FCSTD DOCUMENT  (FreeCAD 0.20R29177 (Git))
Label: assembly
Comment: LumenPnP
License: GPL-3.0 license
LicenseURL: https://github.com/opulo-inc/lumenpnp/blob/main/LICENSE
objects: Part::FeaturePython×378, App::FeaturePython×81, App::DocumentObjectGroup×34, Part::Feature×10, Part::Compound×2
note: 390 computed .brp shape members not serialized (recipe doc carries the construction recipe); baked Part::Feature solids carry a one-line shape summary decoded from their .brp

FEATURE [Part::FeaturePython] b_OTS_0009_20x20_v_slot_600mm1_001_003  label="vslot-extrusion-20mmx20mmx600mm005"  # a2plus imported part (geometry in sourceFile) (typed FeaturePython)
  Placement = pos=(-0.0573608,219.183,134.886) rot=(0.57735,-0.57735,-0.57735;2.0944rad)
  Visibility1 = true
  a2p_Version = V0.1
  fixedPosition = false
  objectType = a2pPart
  sourceFile = ./MISC/vslot-extrusion-20mmx20mmx600mm.step
  sourcePart = vslot-extrusion-20mmx20mmx600mm
  subassemblyImport = false
  timeLastImport = 1.66336e+09
  updateColors = true
FEATURE [Part::FeaturePython] Screw021  label="M5x40-Screw339"  # Fasteners workbench fastener (typed FeaturePython)
  Placement = pos=(634.23,194.1,163.97) rot=(0,0,1;1.5708rad)
  Visibility1 = true
  diameter = 6
  invert = false
  leftHanded = false
  length = 12
  lengthCustom = 40
  matchOuter = false
  offset = 0
  thread = false
  type = 33
FEATURE [Part::FeaturePython] Screw022  label="M5x10-Screw"  # Fasteners workbench fastener (typed FeaturePython)
  Placement = pos=(25.025,209.125,159.768) rot=(0,0,-1;1.5708rad)
  Visibility1 = true
  diameter = 6
  invert = false
  leftHanded = false
  length = 1
  lengthCustom = 10
  matchOuter = false
  offset = 0
  thread = false
  type = 33
FEATURE [Part::FeaturePython] b_M5_tslot_nut1_001_  label="M5-tslot-nut"  # a2plus imported part (geometry in sourceFile) (typed FeaturePython)
  Placement = pos=(25.0282,209.312,148.905) rot=(0,0,1;0rad)
  Visibility1 = true
  a2p_Version = V0.1
  fixedPosition = false
  objectType = a2pPart
  sourceFile = ./FST/M5-tslot-nut.step
  sourcePart = M5-tslot-nut
  subassemblyImport = false
  timeLastImport = 1.66336e+09
  updateColors = true
FEATURE [Part::FeaturePython] b_M5_tslot_nut1_001_001  label="M5-tslot-nut001"  # a2plus imported part (geometry in sourceFile) (typed FeaturePython)
  Placement = pos=(572.328,209.112,148.905) rot=(0,0,1;0rad)
  Visibility1 = true
  a2p_Version = V0.1
  fixedPosition = false
  objectType = a2pPart
  sourceFile = ./FST/M5-tslot-nut.step
  sourcePart = M5-tslot-nut
  subassemblyImport = false
  timeLastImport = 1.66336e+09
  updateColors = true
FEATURE [Part::FeaturePython] Screw023  label="M5x10-Screw321"  # Fasteners workbench fastener (typed FeaturePython)
  Placement = pos=(572.27,209.12,158.94) rot=(0,0,-1;1.5708rad)
  Visibility1 = true
  diameter = 6
  invert = false
  leftHanded = false
  length = 1
  lengthCustom = 10
  matchOuter = false
  offset = 0
  thread = false
  type = 33
FEATURE [Part::FeaturePython] b_FDM_0027_belt_clamp_001_  label="belt-clamp001"  # a2plus imported part (geometry in sourceFile) (typed FeaturePython)
  Placement = pos=(-11.975,236.125,99.7676) rot=(0.57735,-0.57735,-0.57735;2.0944rad)
  Visibility1 = true
  a2p_Version = V0.1
  fixedPosition = false
  objectType = a2pPart
  sourceFile = ./FDM/belt-clamp.FCStd
  sourcePart = Body
  subassemblyImport = false
  timeLastImport = 1.66336e+09
  updateColors = true
FEATURE [Part::FeaturePython] b_FDM_0027_belt_clamp_001_001  label="belt-clamp002"  # a2plus imported part (geometry in sourceFile) (typed FeaturePython)
  Placement = pos=(-11.975,182.125,99.7676) rot=(-0.57735,0.57735,0.57735;4.18879rad)
  Visibility1 = true
  a2p_Version = V0.1
  fixedPosition = false
  objectType = a2pPart
  sourceFile = ./FDM/belt-clamp.FCStd
  sourcePart = Body
  subassemblyImport = false
  timeLastImport = 1.66336e+09
  updateColors = true
FEATURE [Part::FeaturePython] Screw099  label="M3x8-Screw670"  # Fasteners workbench fastener (typed FeaturePython)
  Placement = pos=(-58.975,224.625,159.768) rot=(1,0,0;3.14159rad)
  Visibility1 = true
  diameter = 1
  invert = false
  leftHanded = false
  length = 1
  lengthCustom = 8
  matchOuter = false
  offset = 0
  thread = false
  type = 39
FEATURE [Part::FeaturePython] Screw097  label="M3x8-Screw671"  # Fasteners workbench fastener (typed FeaturePython)
  Placement = pos=(-27.975,224.625,159.768) rot=(1,0,0;3.14159rad)
  Visibility1 = true
  diameter = 1
  invert = false
  leftHanded = false
  length = 1
  lengthCustom = 8
  matchOuter = false
  offset = 0
  thread = false
  type = 39
FEATURE [Part::FeaturePython] Screw100  label="M3x8-Screw672"  # Fasteners workbench fastener (typed FeaturePython)
  Placement = pos=(-58.975,193.625,159.768) rot=(1,0,0;3.14159rad)
  Visibility1 = true
  diameter = 1
  invert = false
  leftHanded = false
  length = 1
  lengthCustom = 8
  matchOuter = false
  offset = 0
  thread = false
  type = 39
FEATURE [Part::FeaturePython] Screw098  label="M3x8-Screw673"  # Fasteners workbench fastener (typed FeaturePython)
  Placement = pos=(-27.975,193.625,159.768) rot=(1,0,0;3.14159rad)
  Visibility1 = true
  diameter = 1
  invert = false
  leftHanded = false
  length = 1
  lengthCustom = 8
  matchOuter = false
  offset = 0
  thread = false
  type = 39
FEATURE [Part::FeaturePython] Screw059  label="M5x25-Screw122"  # Fasteners workbench fastener (typed FeaturePython)
  Placement = pos=(634.17,209.27,154.08) rot=(0,0,1;1.5708rad)
  Visibility1 = true
  diameter = 6
  invert = false
  leftHanded = false
  length = 6
  lengthCustom = 25
  matchOuter = false
  offset = 0
  thread = false
  type = 33
FEATURE [Part::FeaturePython] Screw060  label="M3x16-Screw084"  # Fasteners workbench fastener (typed FeaturePython)
  Placement = pos=(638.25,224.21,144.08) rot=(0.57735,-0.57735,0.57735;4.18879rad)
  Visibility1 = true
  diameter = 4
  invert = false
  leftHanded = false
  length = 6
  lengthCustom = 16
  matchOuter = false
  offset = 0
  thread = false
  type = 33
FEATURE [Part::FeaturePython] Screw058  label="M5x10-Screw326"  # Fasteners workbench fastener (typed FeaturePython)
  Placement = pos=(615.37,236.11,106.53) rot=(0.57735,0.57735,0.57735;2.0944rad)
  Visibility1 = true
  diameter = 6
  invert = false
  leftHanded = false
  length = 1
  lengthCustom = 10
  matchOuter = false
  offset = 0
  thread = false
  type = 33
FEATURE [Part::FeaturePython] Screw057  label="M5x10-Screw366"  # Fasteners workbench fastener (typed FeaturePython)
  Placement = pos=(615.37,236.11,91.54) rot=(0.57735,0.57735,0.57735;2.0944rad)
  Visibility1 = true
  diameter = 6
  invert = false
  leftHanded = false
  length = 1
  lengthCustom = 10
  matchOuter = false
  offset = 0
  thread = false
  type = 33
FEATURE [Part::FeaturePython] Screw056  label="M5x10-Screw328"  # Fasteners workbench fastener (typed FeaturePython)
  Placement = pos=(615.37,182.19,91.54) rot=(0.57735,0.57735,0.57735;2.0944rad)
  Visibility1 = true
  diameter = 6
  invert = false
  leftHanded = false
  length = 1
  lengthCustom = 10
  matchOuter = false
  offset = 0
  thread = false
  type = 33
FEATURE [Part::FeaturePython] b_FDM_0027_belt_clamp_001_005  label="belt-clamp003"  # a2plus imported part (geometry in sourceFile) (typed FeaturePython)
  Placement = pos=(612.402,182.156,98.9408) rot=(0.57735,0.57735,0.57735;2.0944rad)
  Visibility1 = true
  a2p_Version = V0.1
  fixedPosition = false
  objectType = a2pPart
  sourceFile = ./FDM/belt-clamp.FCStd
  sourcePart = Body
  subassemblyImport = false
  timeLastImport = 1.66336e+09
  updateColors = true
FEATURE [Part::FeaturePython] b_FDM_0027_belt_clamp_001_004  label="belt-clamp004"  # a2plus imported part (geometry in sourceFile) (typed FeaturePython)
  Placement = pos=(612.402,236.126,99.0108) rot=(0.57735,0.57735,0.57735;2.0944rad)
  Visibility1 = true
  a2p_Version = V0.1
  fixedPosition = false
  objectType = a2pPart
  sourceFile = ./FDM/belt-clamp.FCStd
  sourcePart = Body
  subassemblyImport = false
  timeLastImport = 1.66336e+09
  updateColors = true
FEATURE [Part::FeaturePython] b_Nema_17_42A02C_v21_001_001  label="NEMA17-stepper"  # a2plus imported part (geometry in sourceFile) (typed FeaturePython)
  Placement = pos=(-43.475,209.125,154.768) rot=(1,0,0;3.14159rad)
  Visibility1 = true
  a2p_Version = V0.1
  fixedPosition = false
  objectType = a2pPart
  sourceFile = ./MISC/NEMA17-stepper.step 
  sourcePart = NEMA17-stepper
  subassemblyImport = false
  timeLastImport = 1.64563e+09
  updateColors = true
FEATURE [Part::FeaturePython] Nut043  label="M5-Nut604"  # Fasteners workbench fastener (typed FeaturePython)
  Placement = pos=(634.166,209.269,134.219) rot=(0.707107,-0.707107,0;3.14159rad)
  Visibility1 = true
  diameter = 3
  invert = false
  leftHanded = false
  matchOuter = false
  offset = 0
  thread = false
  type = 5
FEATURE [Part::FeaturePython] Nut042  label="M5-Nut605"  # Fasteners workbench fastener (typed FeaturePython)
  Placement = pos=(634.224,194.15,128.957) rot=(0.866025,0.5,0;3.14159rad)
  Visibility1 = true
  diameter = 3
  invert = false
  leftHanded = false
  matchOuter = false
  offset = 0
  thread = false
  type = 5
FEATURE [Part::FeaturePython] b_Gates_2GT_20T_Toothed_Pulley1_001_001  label="GT2-pulley"  # a2plus imported part (geometry in sourceFile) (typed FeaturePython)
  Placement = pos=(-43.475,209.125,156.168) rot=(0.57735,0.57735,-0.57735;4.18879rad)
  Visibility1 = true
  a2p_Version = V0.1
  fixedPosition = false
  objectType = a2pPart
  sourceFile = ./cad/MISC/GT2-pulley.STEP
  sourcePart = GT2-pulley
  subassemblyImport = false
  timeLastImport = 1.64563e+09
  updateColors = true
FEATURE [Part::FeaturePython] b_Gates_2GT_20T_Toothed_Idler1_001_002  label="GT2-idler"  # a2plus imported part (geometry in sourceFile) (typed FeaturePython)
  Placement = pos=(634.179,209.286,138.99) rot=(0.57735,-0.57735,-0.57735;2.0944rad)
  Visibility1 = true
  a2p_Version = V0.1
  fixedPosition = false
  objectType = a2pPart
  sourceFile = ./cad/MISC/GT2-idler.STEP
  sourcePart = GT2-idler
  subassemblyImport = false
  timeLastImport = 1.64563e+09
  updateColors = true
FEATURE [Part::FeaturePython] Screw055  label="M5x10-Screw329"  # Fasteners workbench fastener (typed FeaturePython)
  Placement = pos=(615.37,182.19,106.47) rot=(0.57735,0.57735,0.57735;2.0944rad)
  Visibility1 = true
  diameter = 6
  invert = false
  leftHanded = false
  length = 1
  lengthCustom = 10
  matchOuter = false
  offset = 0
  thread = false
  type = 33
FEATURE [Part::FeaturePython] Nut041  label="M5-Nut608"  # Fasteners workbench fastener (typed FeaturePython)
  Placement = pos=(605.676,236.093,106.547) rot=(0.447214,0.774597,0.447214;1.82348rad)
  Visibility1 = true
  diameter = 7
  invert = false
  leftHanded = false
  matchOuter = false
  offset = 0
  thread = false
  type = 7
FEATURE [Part::FeaturePython] Nut040  label="M5-Nut609"  # Fasteners workbench fastener (typed FeaturePython)
  Placement = pos=(605.676,236.072,91.571) rot=(0.447214,0.774597,0.447214;1.82348rad)
  Visibility1 = true
  diameter = 7
  invert = false
  leftHanded = false
  matchOuter = false
  offset = 0
  thread = false
  type = 7
FEATURE [Part::FeaturePython] Nut039  label="M5-Nut612"  # Fasteners workbench fastener (typed FeaturePython)
  Placement = pos=(605.676,182.149,106.514) rot=(0.447214,0.774597,0.447214;1.82348rad)
  Visibility1 = true
  diameter = 7
  invert = false
  leftHanded = false
  matchOuter = false
  offset = 0
  thread = false
  type = 7
FEATURE [Part::FeaturePython] Nut038  label="M5-Nut613"  # Fasteners workbench fastener (typed FeaturePython)
  Placement = pos=(605.676,182.168,91.527) rot=(0.447214,0.774597,0.447214;1.82348rad)
  Visibility1 = true
  diameter = 7
  invert = false
  leftHanded = false
  matchOuter = false
  offset = 0
  thread = false
  type = 7
FEATURE [Part::FeaturePython] Nut044  label="M3-Nut451"  # Fasteners workbench fastener (typed FeaturePython)
  Placement = pos=(632.154,224.209,144.071) rot=(0.447214,-0.774597,-0.447214;1.82348rad)
  Visibility1 = true
  diameter = 4
  invert = false
  leftHanded = false
  matchOuter = false
  offset = 0
  thread = false
  type = 7
FEATURE [Part::FeaturePython] b_OTS_0002_00_usb_webcam_001_  label="usb-camera"  # a2plus imported part (geometry in sourceFile) (typed FeaturePython)
  Placement = pos=(444.284,221.423,101.39) rot=(1,0,0;3.14159rad)
  Visibility1 = true
  a2p_Version = V0.1
  fixedPosition = false
  objectType = a2pPart
  sourceFile = ./MISC/usb-camera.FCStd
  sourcePart = Body
  subassemblyImport = false
  timeLastImport = 1.66336e+09
  updateColors = true
FEATURE [Part::FeaturePython] b_FDM_0011_x_gantry_front_001_  label="x-gantry-front"  # a2plus imported part (geometry in sourceFile) (typed FeaturePython)
  Placement = pos=(443.775,194.2,123.4) rot=(1,0,0;1.5708rad)
  Visibility1 = true
  a2p_Version = V0.1
  fixedPosition = false
  objectType = a2pPart
  sourceFile = ./FDM/x-gantry-front.FCStd
  sourcePart = Body
  subassemblyImport = false
  timeLastImport = 1.66336e+09
  updateColors = true
FEATURE [Part::FeaturePython] b_FDM_0014_down_camera_mount_001_  label="top-camera-mount"  # a2plus imported part (geometry in sourceFile) (typed FeaturePython)
  Placement = pos=(443.775,224.45,104.9) rot=(0,0,1;3.14159rad)
  Visibility1 = true
  a2p_Version = V0.1
  fixedPosition = false
  objectType = a2pPart
  sourceFile = ./FDM/top-camera-mount.FCStd
  sourcePart = Body
  subassemblyImport = false
  timeLastImport = 1.66336e+09
  updateColors = true
FEATURE [Part::FeaturePython] b_FDM_0015_down_light_mount_001_  label="top-light-mount"  # a2plus imported part (geometry in sourceFile) (typed FeaturePython)
  Placement = pos=(443.775,224.45,81.4) rot=(-0.223515,0.973178,-0.054468;0rad)
  Visibility1 = true
  a2p_Version = V0.1
  fixedPosition = false
  objectType = a2pPart
  sourceFile = ./FDM/top-light-mount.FCStd
  sourcePart = Body
  subassemblyImport = false
  timeLastImport = 1.66336e+09
  updateColors = true
FEATURE [Part::FeaturePython] b_FDM_0027_belt_clamp_001_002  label="belt-clamp005"  # a2plus imported part (geometry in sourceFile) (typed FeaturePython)
  Placement = pos=(422.775,234.2,144.9) rot=(-1,0,0;1.5708rad)
  Visibility1 = true
  a2p_Version = V0.1
  fixedPosition = false
  objectType = a2pPart
  sourceFile = ./FDM/belt-clamp.FCStd
  sourcePart = Body
  subassemblyImport = false
  timeLastImport = 1.66336e+09
  updateColors = true
FEATURE [Part::FeaturePython] Nut021  label="M5-Nut919"  # Fasteners workbench fastener (typed FeaturePython)
  Placement = pos=(464.775,228.2,152.4) rot=(-0.186157,0.694747,0.694747;2.77349rad)
  Visibility1 = true
  diameter = 7
  invert = false
  leftHanded = false
  matchOuter = false
  offset = 0
  thread = false
  type = 7
FEATURE [Part::FeaturePython] Nut022  label="M5-Nut920"  # Fasteners workbench fastener (typed FeaturePython)
  Placement = pos=(464.775,228.2,137.4) rot=(-0.186157,0.694747,0.694747;2.77349rad)
  Visibility1 = true
  diameter = 7
  invert = false
  leftHanded = false
  matchOuter = false
  offset = 0
  thread = false
  type = 7
FEATURE [Part::FeaturePython] Screw038  label="M5x10-Screw483"  # Fasteners workbench fastener (typed FeaturePython)
  Placement = pos=(464.775,237.2,137.4) rot=(0.57735,0.57735,0.57735;4.18879rad)
  Visibility1 = true
  diameter = 6
  invert = false
  leftHanded = false
  length = 1
  lengthCustom = 10
  matchOuter = false
  offset = 0
  thread = false
  type = 33
FEATURE [Part::FeaturePython] Screw039  label="M5x10-Screw484"  # Fasteners workbench fastener (typed FeaturePython)
  Placement = pos=(464.775,237.2,152.4) rot=(-0.57735,-0.57735,-0.57735;2.0944rad)
  Visibility1 = true
  diameter = 6
  invert = false
  leftHanded = false
  length = 1
  lengthCustom = 10
  matchOuter = false
  offset = 0
  thread = false
  type = 33
FEATURE [Part::FeaturePython] Nut023  label="M5-Nut921"  # Fasteners workbench fastener (typed FeaturePython)
  Placement = pos=(422.775,228.417,137.4) rot=(-0.186157,0.694747,0.694747;2.77349rad)
  Visibility1 = true
  diameter = 7
  invert = false
  leftHanded = false
  matchOuter = false
  offset = 0
  thread = false
  type = 7
FEATURE [Part::FeaturePython] Nut024  label="M5-Nut922"  # Fasteners workbench fastener (typed FeaturePython)
  Placement = pos=(422.775,228.2,152.4) rot=(-0.186157,0.694747,0.694747;2.77349rad)
  Visibility1 = true
  diameter = 7
  invert = false
  leftHanded = false
  matchOuter = false
  offset = 0
  thread = false
  type = 7
FEATURE [Part::FeaturePython] Screw040  label="M5x10-Screw485"  # Fasteners workbench fastener (typed FeaturePython)
  Placement = pos=(422.775,237.2,152.4) rot=(0.57735,0.57735,0.57735;4.18879rad)
  Visibility1 = true
  diameter = 6
  invert = false
  leftHanded = false
  length = 1
  lengthCustom = 10
  matchOuter = false
  offset = 0
  thread = false
  type = 33
FEATURE [Part::FeaturePython] b_FDM_0027_belt_clamp_001_003  label="belt-clamp006"  # a2plus imported part (geometry in sourceFile) (typed FeaturePython)
  Placement = pos=(464.775,234.2,144.9) rot=(0,0.707107,0.707107;3.14159rad)
  Visibility1 = true
  a2p_Version = V0.1
  fixedPosition = false
  objectType = a2pPart
  sourceFile = ./FDM/belt-clamp.FCStd
  sourcePart = Body
  subassemblyImport = false
  timeLastImport = 1.66336e+09
  updateColors = true
FEATURE [Part::FeaturePython] b_Nema_17_42A02C_v21_001_  label="NEMA17-stepper001"  # a2plus imported part (geometry in sourceFile) (typed FeaturePython)
  Placement = pos=(443.776,187.252,212.248) rot=(-0.268444,0.681153,-0.681153;3.66612rad)
  Visibility1 = true
  a2p_Version = V0.1
  fixedPosition = false
  objectType = a2pPart
  sourceFile = ./MISC/NEMA17-stepper.step 
  sourcePart = NEMA17-stepper
  subassemblyImport = false
  timeLastImport = 1.64563e+09
  updateColors = true
FEATURE [Part::FeaturePython] b_Gates_2GT_20T_Toothed_Idler1_001_  label="GT2-idler001"  # a2plus imported part (geometry in sourceFile) (typed FeaturePython)
  Placement = pos=(443.78,185.1,99.0503) rot=(-0.707107,0,0.707107;3.14159rad)
  Visibility1 = true
  a2p_Version = V0.1
  fixedPosition = false
  objectType = a2pPart
  sourceFile = ./cad/MISC/GT2-idler.STEP
  sourcePart = GT2-idler
  subassemblyImport = false
  timeLastImport = 1.64563e+09
  updateColors = true
FEATURE [Part::FeaturePython] Screw086  label="M3x8-Screw507"  # Fasteners workbench fastener (typed FeaturePython)
  Placement = pos=(443.74,191.38,190.34) rot=(1,0,0;1.5708rad)
  Visibility1 = true
  diameter = 1
  invert = false
  leftHanded = false
  length = 1
  lengthCustom = 8
  matchOuter = false
  offset = 0
  thread = false
  type = 39
FEATURE [Part::FeaturePython] Screw087  label="M3x8-Screw508"  # Fasteners workbench fastener (typed FeaturePython)
  Placement = pos=(465.75,191.38,212.29) rot=(1,0,0;1.5708rad)
  Visibility1 = true
  diameter = 1
  invert = false
  leftHanded = false
  length = 1
  lengthCustom = 8
  matchOuter = false
  offset = 0
  thread = false
  type = 39
FEATURE [Part::FeaturePython] Screw088  label="M3x8-Screw509"  # Fasteners workbench fastener (typed FeaturePython)
  Placement = pos=(421.83,191.38,212.25) rot=(1,0,0;1.5708rad)
  Visibility1 = true
  diameter = 1
  invert = false
  leftHanded = false
  length = 1
  lengthCustom = 8
  matchOuter = false
  offset = 0
  thread = false
  type = 39
FEATURE [Part::FeaturePython] Nut032  label="M3-Nut520"  # Fasteners workbench fastener (typed FeaturePython)
  Placement = pos=(423.74,196.87,104.003) rot=(0.935113,0.250563,-0.250563;1.63783rad)
  Visibility1 = true
  diameter = 4
  invert = false
  leftHanded = false
  matchOuter = false
  offset = 0
  thread = false
  type = 7
FEATURE [Part::FeaturePython] Nut028  label="M3-Nut521"  # Fasteners workbench fastener (typed FeaturePython)
  Placement = pos=(423.738,196.87,143.899) rot=(0.935113,0.250563,-0.250563;1.63783rad)
  Visibility1 = true
  diameter = 4
  invert = false
  leftHanded = false
  matchOuter = false
  offset = 0
  thread = false
  type = 7
FEATURE [Part::FeaturePython] Nut027  label="M3-Nut522"  # Fasteners workbench fastener (typed FeaturePython)
  Placement = pos=(423.75,196.87,183.96) rot=(0.935113,0.250563,-0.250563;1.63783rad)
  Visibility1 = true
  diameter = 4
  invert = false
  leftHanded = false
  matchOuter = false
  offset = 0
  thread = false
  type = 7
FEATURE [Part::FeaturePython] Nut031  label="M3-Nut523"  # Fasteners workbench fastener (typed FeaturePython)
  Placement = pos=(463.628,196.87,184.111) rot=(0.935113,0.250563,-0.250563;1.63783rad)
  Visibility1 = true
  diameter = 4
  invert = false
  leftHanded = false
  matchOuter = false
  offset = 0
  thread = false
  type = 7
FEATURE [Part::FeaturePython] Nut029  label="M3-Nut524"  # Fasteners workbench fastener (typed FeaturePython)
  Placement = pos=(463.702,196.87,104.059) rot=(0.935113,0.250563,-0.250563;1.63783rad)
  Visibility1 = true
  diameter = 4
  invert = false
  leftHanded = false
  matchOuter = false
  offset = 0
  thread = false
  type = 7
FEATURE [Part::FeaturePython] Nut030  label="M3-Nut525"  # Fasteners workbench fastener (typed FeaturePython)
  Placement = pos=(463.67,196.87,144.204) rot=(0.935113,0.250563,-0.250563;1.63783rad)
  Visibility1 = true
  diameter = 4
  invert = false
  leftHanded = false
  matchOuter = false
  offset = 0
  thread = false
  type = 7
FEATURE [Part::FeaturePython] Screw044  label="M5x25-Screw135"  # Fasteners workbench fastener (typed FeaturePython)
  Placement = pos=(443.743,175.103,98.994) rot=(0,0.707107,-0.707107;3.14159rad)
  Visibility1 = true
  diameter = 6
  invert = false
  leftHanded = false
  length = 6
  lengthCustom = 25
  matchOuter = false
  offset = 10.5
  thread = false
  type = 33
FEATURE [Part::FeaturePython] Screw041  label="M5x10-Screw486"  # Fasteners workbench fastener (typed FeaturePython)
  Placement = pos=(422.775,237.2,137.4) rot=(0.57735,0.57735,0.57735;4.18879rad)
  Visibility1 = true
  diameter = 6
  invert = false
  leftHanded = false
  length = 1
  lengthCustom = 10
  matchOuter = false
  offset = 0
  thread = false
  type = 33
FEATURE [Part::FeaturePython] b_Gates_2GT_20T_Toothed_Pulley1_001_  label="GT2-pulley001"  # a2plus imported part (geometry in sourceFile) (typed FeaturePython)
  Placement = pos=(443.79,192,212.28) rot=(-0.707107,0,0.707107;3.14159rad)
  Visibility1 = true
  a2p_Version = V0.1
  fixedPosition = false
  objectType = a2pPart
  sourceFile = ./cad/MISC/GT2-pulley.STEP
  sourcePart = GT2-pulley
  subassemblyImport = false
  timeLastImport = 1.64563e+09
  updateColors = true
FEATURE [Part::FeaturePython] b_FDM_0040_z_gantry_backplate_left_001_  label="z-gantry-backplate-left"  # a2plus imported part (geometry in sourceFile) (typed FeaturePython)
  Placement = pos=(405.5,177.8,112.56) rot=(1,0,0;1.5708rad)
  a2p_Version = V0.1
  fixedPosition = false
  objectType = a2pPart
  sourceFile = .\FDM\z-gantry-backplate-left.FCStd
  subassemblyImport = false
  timeLastImport = 1.65531e+09
  updateColors = true
FEATURE [Part::FeaturePython] Screw144  label="M3x8-Screw531"  # Fasteners workbench fastener (typed FeaturePython)
  Placement = pos=(416.22,171.94,150.64) rot=(1,0,0;1.5708rad)
  Visibility1 = true
  diameter = 1
  invert = false
  leftHanded = false
  length = 1
  lengthCustom = 8
  matchOuter = false
  offset = 0
  thread = false
  type = 39
FEATURE [Part::FeaturePython] Screw146  label="M3x8-Screw532"  # Fasteners workbench fastener (typed FeaturePython)
  Placement = pos=(431.25,171.94,150.53) rot=(1,0,0;1.5708rad)
  Visibility1 = true
  diameter = 1
  invert = false
  leftHanded = false
  length = 1
  lengthCustom = 8
  matchOuter = false
  offset = 0
  thread = false
  type = 39
FEATURE [Part::FeaturePython] b_OTS_0001_00_CP40_nozzle_holder_001_  label="CP40-holder"  # a2plus imported part (geometry in sourceFile) (typed FeaturePython)
  Placement = pos=(420.048,155.79,87.7845) rot=(0.57735,-0.57735,-0.57735;2.0944rad)
  Visibility1 = true
  a2p_Version = V0.1
  fixedPosition = false
  objectType = a2pPart
  sourceFile = ./MISC/cp40-holder.FCStd
  sourcePart = Body
  subassemblyImport = false
  timeLastImport = 1.65531e+09
  updateColors = true
FEATURE [Part::FeaturePython] b_MS4M_M51_001_  label="pneumatic-adapter-MS4M-M5"  # a2plus imported part (geometry in sourceFile) (typed FeaturePython)
  Placement = pos=(420.152,155.83,162.512) rot=(0.57735,-0.57735,-0.57735;2.0944rad)
  Visibility1 = true
  a2p_Version = V0.1
  fixedPosition = false
  objectType = a2pPart
  sourceFile = ./MISC/pneumatic-adapter-MS4M-M5.STEP
  sourcePart = MS4M-M5
  subassemblyImport = false
  timeLastImport = 1.65531e+09
  updateColors = true
FEATURE [Part::FeaturePython] Screw148  label="M3x8-Screw523"  # Fasteners workbench fastener (typed FeaturePython)
  Placement = pos=(456.42,171.94,150.5) rot=(1,0,0;1.5708rad)
  Visibility1 = true
  diameter = 1
  invert = false
  leftHanded = false
  length = 1
  lengthCustom = 8
  matchOuter = false
  offset = 0
  thread = false
  type = 39
FEATURE [Part::FeaturePython] Screw149  label="M3x8-Screw524"  # Fasteners workbench fastener (typed FeaturePython)
  Placement = pos=(471.41,171.94,150.5) rot=(1,0,0;1.5708rad)
  Visibility1 = true
  diameter = 1
  invert = false
  leftHanded = false
  length = 1
  lengthCustom = 8
  matchOuter = false
  offset = 0
  thread = false
  type = 39
FEATURE [Part::FeaturePython] b_FDM_0041_z_gantry_backplate_right_001_  label="z-gantry-backplate-right"  # a2plus imported part (geometry in sourceFile) (typed FeaturePython)
  Placement = pos=(482.233,178.019,112.536) rot=(1,0,0;1.5708rad)
  a2p_Version = V0.1
  fixedPosition = false
  objectType = a2pPart
  sourceFile = ./FDM/z-gantry-backplate-right.FCStd
  sourcePart = Body
  subassemblyImport = false
  timeLastImport = 1.65531e+09
  updateColors = true
FEATURE [Part::FeaturePython] Screw085  label="M3x8-Screw518"  # Fasteners workbench fastener (typed FeaturePython)
  Placement = pos=(443.74,191.38,234.2) rot=(1,0,0;1.5708rad)
  Visibility1 = true
  diameter = 1
  invert = false
  leftHanded = false
  length = 1
  lengthCustom = 8
  matchOuter = false
  offset = 0
  thread = false
  type = 39
FEATURE [Part::FeaturePython] Screw171  label="M3x14-Screw191"  # Fasteners workbench fastener (typed FeaturePython)
  Placement = pos=(466.574,236.252,118.069) rot=(0,0.707107,0.707107;3.14159rad)
  baseObject = -> b_FDM_0014_down_camera_mount_001_ [Edge38]
  diameter = 1
  invert = false
  leftHanded = false
  length = 9
  lengthCustom = 14
  matchOuter = false
  offset = 0
  thread = false
  type = 39
FEATURE [Part::FeaturePython] Nut077  label="M3-Nut"  # Fasteners workbench fastener (typed FeaturePython)
  Placement = pos=(421.275,229.3,118.4) rot=(0,0.707107,0.707107;3.14159rad)
  diameter = 4
  invert = false
  leftHanded = false
  matchOuter = false
  offset = 0
  thread = false
  type = 7
FEATURE [Part::FeaturePython] Nut079  label="M3-Nut543"  # Fasteners workbench fastener (typed FeaturePython)
  Placement = pos=(466.275,229.3,118.4) rot=(0.186157,0.694747,0.694747;3.50969rad)
  diameter = 4
  invert = false
  leftHanded = false
  matchOuter = false
  offset = 0
  thread = false
  type = 7
FEATURE [Part::FeaturePython] b_M5_tslot_nut1_001_008  label="M5-tslot-nut002"  # a2plus imported part (geometry in sourceFile) (typed FeaturePython)
  Placement = pos=(9.94821,-70.1584,105.165) rot=(0,0,1;1.5708rad)
  Visibility1 = true
  a2p_Version = V0.1
  fixedPosition = false
  objectType = a2pPart
  sourceFile = ./FST/M5-tslot-nut.step
  sourcePart = M5-tslot-nut
  subassemblyImport = false
  timeLastImport = 1.66336e+09
  updateColors = true
FEATURE [Part::FeaturePython] Nut048  label="M3-Nut464"  # Fasteners workbench fastener (typed FeaturePython)
  Placement = pos=(24.9656,-93.169,99.99) rot=(0.57735,-0.57735,0.57735;2.0944rad)
  Visibility1 = true
  diameter = 4
  invert = false
  leftHanded = false
  matchOuter = false
  offset = 0
  thread = false
  type = 7
FEATURE [Part::FeaturePython] Nut045  label="M5-Nut625"  # Fasteners workbench fastener (typed FeaturePython)
  Placement = pos=(-5.03877,-97.4915,83.9035) rot=(0.866025,0.5,0;3.14159rad)
  Visibility1 = true
  diameter = 3
  invert = false
  leftHanded = false
  matchOuter = false
  offset = 0
  thread = false
  type = 5
FEATURE [Part::FeaturePython] b_Gates_2GT_20T_Toothed_Idler1_001_001  label="GT2-idler002"  # a2plus imported part (geometry in sourceFile) (typed FeaturePython)
  Placement = pos=(10.0586,-97.7236,95.0003) rot=(0.57735,-0.57735,-0.57735;2.0944rad)
  Visibility1 = true
  a2p_Version = V0.1
  fixedPosition = false
  objectType = a2pPart
  sourceFile = ./cad/MISC/GT2-idler.STEP
  sourcePart = GT2-idler
  subassemblyImport = false
  timeLastImport = 1.64563e+09
  updateColors = true
FEATURE [Part::FeaturePython] Nut033  label="M5-Nut626"  # Fasteners workbench fastener (typed FeaturePython)
  Placement = pos=(9.97594,-97.5692,89.9635) rot=(0.707107,0.707107,0;3.14159rad)
  Visibility1 = true
  diameter = 3
  invert = false
  leftHanded = false
  matchOuter = false
  offset = 0
  thread = false
  type = 5
FEATURE [Part::FeaturePython] Screw052  label="M3x16-Screw085"  # Fasteners workbench fastener (typed FeaturePython)
  Placement = pos=(24.99,-102.16,100) rot=(0.57735,-0.57735,0.57735;2.0944rad)
  Visibility1 = true
  diameter = 4
  invert = false
  leftHanded = false
  length = 6
  lengthCustom = 16
  matchOuter = false
  offset = 0
  thread = false
  type = 33
FEATURE [Part::FeaturePython] Screw053  label="M5x10-Screw334"  # Fasteners workbench fastener (typed FeaturePython)
  Placement = pos=(9.89,-70.16,114.96) rot=(0,0,-1;1.5708rad)
  Visibility1 = true
  diameter = 6
  invert = false
  leftHanded = false
  length = 1
  lengthCustom = 10
  matchOuter = false
  offset = 0
  thread = false
  type = 33
FEATURE [Part::FeaturePython] Screw054  label="M5x25-Screw127"  # Fasteners workbench fastener (typed FeaturePython)
  Placement = pos=(9.99,-97.57,109.98) rot=(0,0,-1;1.5708rad)
  Visibility1 = true
  diameter = 6
  invert = false
  leftHanded = false
  length = 6
  lengthCustom = 25
  matchOuter = false
  offset = 0
  thread = false
  type = 33
FEATURE [Part::FeaturePython] Screw035  label="M5x10-Screw335"  # Fasteners workbench fastener (typed FeaturePython)
  Placement = pos=(-4.92,-45.15,30.1) rot=(0.57735,-0.57735,-0.57735;2.0944rad)
  Visibility1 = true
  diameter = 6
  invert = false
  leftHanded = false
  length = 1
  lengthCustom = 10
  matchOuter = false
  offset = 0
  thread = false
  type = 33
FEATURE [Part::FeaturePython] Screw036  label="M5x10-Screw336"  # Fasteners workbench fastener (typed FeaturePython)
  Placement = pos=(-4.92,-70.14,30.1) rot=(0.57735,-0.57735,-0.57735;2.0944rad)
  Visibility1 = true
  diameter = 6
  invert = false
  leftHanded = false
  length = 1
  lengthCustom = 10
  matchOuter = false
  offset = 0
  thread = false
  type = 33
FEATURE [Part::FeaturePython] Screw037  label="M5x10-Screw337"  # Fasteners workbench fastener (typed FeaturePython)
  Placement = pos=(9.96,-25.33,9.99) rot=(1,0,0;1.5708rad)
  Visibility1 = true
  diameter = 6
  invert = false
  leftHanded = false
  length = 1
  lengthCustom = 10
  matchOuter = false
  offset = 0
  thread = false
  type = 33
FEATURE [Part::FeaturePython] Screw051  label="M5x40-Screw344"  # Fasteners workbench fastener (typed FeaturePython)
  Placement = pos=(-4.98,-97.58,119.74) rot=(0,0,-1;1.5708rad)
  Visibility1 = true
  diameter = 6
  invert = false
  leftHanded = false
  length = 12
  lengthCustom = 40
  matchOuter = false
  offset = 0
  thread = false
  type = 33
FEATURE [Part::FeaturePython] b_M5_tslot_nut1_001_009  label="M5-tslot-nut003"  # a2plus imported part (geometry in sourceFile) (typed FeaturePython)
  Placement = pos=(4.76821,-70.1584,30.1746) rot=(0.57735,0.57735,-0.57735;4.18879rad)
  Visibility1 = true
  a2p_Version = V0.1
  fixedPosition = false
  objectType = a2pPart
  sourceFile = ./FST/M5-tslot-nut.step
  sourcePart = M5-tslot-nut
  subassemblyImport = false
  timeLastImport = 1.66336e+09
  updateColors = true
FEATURE [Part::FeaturePython] b_M5_tslot_nut1_001_010  label="M5-tslot-nut004"  # a2plus imported part (geometry in sourceFile) (typed FeaturePython)
  Placement = pos=(4.76821,-45.2084,30.1746) rot=(0.57735,0.57735,-0.57735;4.18879rad)
  Visibility1 = true
  a2p_Version = V0.1
  fixedPosition = false
  objectType = a2pPart
  sourceFile = ./FST/M5-tslot-nut.step
  sourcePart = M5-tslot-nut
  subassemblyImport = false
  timeLastImport = 1.66336e+09
  updateColors = true
FEATURE [Part::FeaturePython] b_M5_tslot_nut1_001_011  label="M5-tslot-nut005"  # a2plus imported part (geometry in sourceFile) (typed FeaturePython)
  Placement = pos=(9.85821,-15.0384,9.95457) rot=(0,0.707107,-0.707107;3.14159rad)
  Visibility1 = true
  a2p_Version = V0.1
  fixedPosition = false
  objectType = a2pPart
  sourceFile = ./FST/M5-tslot-nut.step
  sourcePart = M5-tslot-nut
  subassemblyImport = false
  timeLastImport = 1.66336e+09
  updateColors = true
FEATURE [Part::FeaturePython] b_FDM_0001_front_left_leg_001_  label="front-left-leg"  # a2plus imported part (geometry in sourceFile) (typed FeaturePython)
  Placement = pos=(19.9755,-0.0519684,19.9889) rot=(0.57735,-0.57735,-0.57735;2.0944rad)
  Visibility1 = true
  a2p_Version = V0.1
  fixedPosition = false
  objectType = a2pPart
  sourceFile = ./FDM/front-left-leg.FCStd
  sourcePart = Body
  subassemblyImport = false
  timeLastImport = 1.66336e+09
  updateColors = true
FEATURE [Part::FeaturePython] Screw061  label="M5x40-Screw345"  # Fasteners workbench fastener (typed FeaturePython)
  Placement = pos=(605.12,-97.58,119.74) rot=(0,0,-1;1.5708rad)
  Visibility1 = true
  diameter = 6
  invert = false
  leftHanded = false
  length = 12
  lengthCustom = 40
  matchOuter = false
  offset = 0
  thread = false
  type = 33
FEATURE [Part::FeaturePython] b_Gates_2GT_20T_Toothed_Idler1_001_003  label="GT2-idler003"  # a2plus imported part (geometry in sourceFile) (typed FeaturePython)
  Placement = pos=(590.059,-97.7236,95.0003) rot=(0.57735,-0.57735,-0.57735;2.0944rad)
  Visibility1 = true
  a2p_Version = V0.1
  fixedPosition = false
  objectType = a2pPart
  sourceFile = ./cad/MISC/GT2-idler.STEP
  sourcePart = GT2-idler
  subassemblyImport = false
  timeLastImport = 1.64563e+09
  updateColors = true
FEATURE [Part::FeaturePython] Nut046  label="M5-Nut627"  # Fasteners workbench fastener (typed FeaturePython)
  Placement = pos=(605.043,-97.4581,83.9035) rot=(0.866025,0.5,0;3.14159rad)
  Visibility1 = true
  diameter = 3
  invert = false
  leftHanded = false
  matchOuter = false
  offset = 0
  thread = false
  type = 5
FEATURE [Part::FeaturePython] Screw062  label="M5x25-Screw128"  # Fasteners workbench fastener (typed FeaturePython)
  Placement = pos=(590.06,-97.57,109.98) rot=(0,0,-1;1.5708rad)
  Visibility1 = true
  diameter = 6
  invert = false
  leftHanded = false
  length = 6
  lengthCustom = 25
  matchOuter = false
  offset = 0
  thread = false
  type = 33
FEATURE [Part::FeaturePython] Nut047  label="M5-Nut628"  # Fasteners workbench fastener (typed FeaturePython)
  Placement = pos=(590.046,-97.5092,89.9635) rot=(0.707107,0.707107,0;3.14159rad)
  Visibility1 = true
  diameter = 3
  invert = false
  leftHanded = false
  matchOuter = false
  offset = 0
  thread = false
  type = 5
FEATURE [Part::FeaturePython] Screw063  label="M3x16-Screw086"  # Fasteners workbench fastener (typed FeaturePython)
  Placement = pos=(574.97,-101,100) rot=(0.57735,-0.57735,0.57735;2.0944rad)
  Visibility1 = true
  diameter = 4
  invert = false
  leftHanded = false
  length = 6
  lengthCustom = 16
  matchOuter = false
  offset = 0
  thread = false
  type = 33
FEATURE [Part::FeaturePython] Nut049  label="M3-Nut465"  # Fasteners workbench fastener (typed FeaturePython)
  Placement = pos=(575.026,-93.169,99.99) rot=(0.57735,-0.57735,0.57735;2.0944rad)
  Visibility1 = true
  diameter = 4
  invert = false
  leftHanded = false
  matchOuter = false
  offset = 0
  thread = false
  type = 7
FEATURE [Part::FeaturePython] Screw064  label="M5x10-Screw338"  # Fasteners workbench fastener (typed FeaturePython)
  Placement = pos=(590.19,-70.16,114.96) rot=(0,0,-1;1.5708rad)
  Visibility1 = true
  diameter = 6
  invert = false
  leftHanded = false
  length = 1
  lengthCustom = 10
  matchOuter = false
  offset = 0
  thread = false
  type = 33
FEATURE [Part::FeaturePython] Screw070  label="M5x10-Screw339"  # Fasteners workbench fastener (typed FeaturePython)
  Placement = pos=(605,-70,29.99) rot=(0.57735,-0.57735,0.57735;4.18879rad)
  Visibility1 = true
  diameter = 6
  invert = false
  leftHanded = false
  length = 1
  lengthCustom = 10
  matchOuter = false
  offset = 0
  thread = false
  type = 33
FEATURE [Part::FeaturePython] Screw071  label="M5x10-Screw340"  # Fasteners workbench fastener (typed FeaturePython)
  Placement = pos=(605,-44.99,29.99) rot=(0.57735,-0.57735,0.57735;4.18879rad)
  Visibility1 = true
  diameter = 6
  invert = false
  leftHanded = false
  length = 1
  lengthCustom = 10
  matchOuter = false
  offset = 0
  thread = false
  type = 33
FEATURE [Part::FeaturePython] Screw072  label="M5x10-Screw341"  # Fasteners workbench fastener (typed FeaturePython)
  Placement = pos=(589.91,-24.98,10.2) rot=(0,0.707107,-0.707107;3.14159rad)
  Visibility1 = true
  diameter = 6
  invert = false
  leftHanded = false
  length = 1
  lengthCustom = 10
  matchOuter = false
  offset = 0
  thread = false
  type = 33
FEATURE [Part::FeaturePython] b_M5_tslot_nut1_001_012  label="M5-tslot-nut006"  # a2plus imported part (geometry in sourceFile) (typed FeaturePython)
  Placement = pos=(590.068,-15.0384,10.1446) rot=(0,0.707107,-0.707107;3.14159rad)
  Visibility1 = true
  a2p_Version = V0.1
  fixedPosition = false
  objectType = a2pPart
  sourceFile = ./FST/M5-tslot-nut.step
  sourcePart = M5-tslot-nut
  subassemblyImport = false
  timeLastImport = 1.66336e+09
  updateColors = true
FEATURE [Part::FeaturePython] b_M5_tslot_nut1_001_013  label="M5-tslot-nut007"  # a2plus imported part (geometry in sourceFile) (typed FeaturePython)
  Placement = pos=(595.208,-70.0184,30.1846) rot=(0.57735,-0.57735,0.57735;4.18879rad)
  Visibility1 = true
  a2p_Version = V0.1
  fixedPosition = false
  objectType = a2pPart
  sourceFile = ./FST/M5-tslot-nut.step
  sourcePart = M5-tslot-nut
  subassemblyImport = false
  timeLastImport = 1.66336e+09
  updateColors = true
FEATURE [Part::FeaturePython] b_M5_tslot_nut1_001_014  label="M5-tslot-nut008"  # a2plus imported part (geometry in sourceFile) (typed FeaturePython)
  Placement = pos=(595.208,-44.9784,30.1846) rot=(0.57735,-0.57735,0.57735;4.18879rad)
  Visibility1 = true
  a2p_Version = V0.1
  fixedPosition = false
  objectType = a2pPart
  sourceFile = ./FST/M5-tslot-nut.step
  sourcePart = M5-tslot-nut
  subassemblyImport = false
  timeLastImport = 1.66336e+09
  updateColors = true
FEATURE [Part::FeaturePython] b_M5_tslot_nut1_001_015  label="M5-tslot-nut009"  # a2plus imported part (geometry in sourceFile) (typed FeaturePython)
  Placement = pos=(589.988,-70.0484,105.085) rot=(0,0,-1;1.5708rad)
  Visibility1 = true
  a2p_Version = V0.1
  fixedPosition = false
  objectType = a2pPart
  sourceFile = ./FST/M5-tslot-nut.step
  sourcePart = M5-tslot-nut
  subassemblyImport = false
  timeLastImport = 1.66336e+09
  updateColors = true
FEATURE [Part::FeaturePython] Screw089  label="M3x8-Screw462"  # Fasteners workbench fastener (typed FeaturePython)
  Placement = pos=(-5.54,531.08,85.24) rot=(0,0,-1;1.5708rad)
  Visibility1 = true
  diameter = 1
  invert = false
  leftHanded = false
  length = 1
  lengthCustom = 8
  matchOuter = false
  offset = 0
  thread = false
  type = 39
FEATURE [Part::FeaturePython] Screw090  label="M3x8-Screw463"  # Fasteners workbench fastener (typed FeaturePython)
  Placement = pos=(-5.54,562.08,85.24) rot=(0,0,1;0rad)
  Visibility1 = true
  diameter = 1
  invert = false
  leftHanded = false
  length = 1
  lengthCustom = 8
  matchOuter = false
  offset = 0
  thread = false
  type = 39
FEATURE [Part::FeaturePython] Screw091  label="M3x8-Screw464"  # Fasteners workbench fastener (typed FeaturePython)
  Placement = pos=(25.34,562.08,85.14) rot=(0,0,1;3.14159rad)
  Visibility1 = true
  diameter = 1
  invert = false
  leftHanded = false
  length = 1
  lengthCustom = 8
  matchOuter = false
  offset = 0
  thread = false
  type = 39
FEATURE [Part::FeaturePython] Screw092  label="M3x8-Screw465"  # Fasteners workbench fastener (typed FeaturePython)
  Placement = pos=(25.34,531.13,85.19) rot=(0,0,-1;1.5708rad)
  Visibility1 = true
  diameter = 1
  invert = false
  leftHanded = false
  length = 1
  lengthCustom = 8
  matchOuter = false
  offset = 0
  thread = false
  type = 39
FEATURE [Part::FeaturePython] b_Nema_17_42A02C_v21_001_002  label="NEMA17-stepper003"  # a2plus imported part (geometry in sourceFile) (typed FeaturePython)
  Placement = pos=(9.84,546.54,90.25) rot=(0,0,1;0rad)
  Visibility1 = true
  a2p_Version = V0.1
  fixedPosition = false
  objectType = a2pPart
  sourceFile = ./MISC/NEMA17-stepper.step 
  sourcePart = NEMA17-stepper
  subassemblyImport = false
  timeLastImport = 1.64563e+09
  updateColors = true
FEATURE [Part::FeaturePython] b_Gates_2GT_20T_Toothed_Pulley1_001_002  label="GT2-pulley002"  # a2plus imported part (geometry in sourceFile) (typed FeaturePython)
  Placement = pos=(9.82,546.52,88.82) rot=(0.57735,0.57735,0.57735;2.0944rad)
  Visibility1 = true
  a2p_Version = V0.1
  fixedPosition = false
  objectType = a2pPart
  sourceFile = ./cad/MISC/GT2-pulley.STEP
  sourcePart = GT2-pulley
  subassemblyImport = false
  timeLastImport = 1.64563e+09
  updateColors = true
FEATURE [Part::FeaturePython] Screw029  label="M5x10-Screw342"  # Fasteners workbench fastener (typed FeaturePython)
  Placement = pos=(9.89,510.06,115.05) rot=(0,0,-1;1.5708rad)
  Visibility1 = true
  diameter = 6
  invert = false
  leftHanded = false
  length = 1
  lengthCustom = 10
  matchOuter = false
  offset = 0
  thread = false
  type = 33
FEATURE [Part::FeaturePython] Screw030  label="M5x10-Screw343"  # Fasteners workbench fastener (typed FeaturePython)
  Placement = pos=(-6.57,510.06,30.11) rot=(0.57735,-0.57735,-0.57735;2.0944rad)
  Visibility1 = true
  diameter = 6
  invert = false
  leftHanded = false
  length = 1
  lengthCustom = 10
  matchOuter = false
  offset = 0
  thread = false
  type = 33
FEATURE [Part::FeaturePython] Screw031  label="M5x10-Screw344"  # Fasteners workbench fastener (typed FeaturePython)
  Placement = pos=(26.33,510.06,30.11) rot=(0.57735,-0.57735,0.57735;4.18879rad)
  Visibility1 = true
  diameter = 6
  invert = false
  leftHanded = false
  length = 1
  lengthCustom = 10
  matchOuter = false
  offset = 0
  thread = false
  type = 33
FEATURE [Part::FeaturePython] b_M5_tslot_nut1_001_002  label="M5-tslot-nut010"  # a2plus imported part (geometry in sourceFile) (typed FeaturePython)
  Placement = pos=(9.95821,510.062,105.175) rot=(0,0,-1;1.5708rad)
  Visibility1 = true
  a2p_Version = V0.1
  fixedPosition = false
  objectType = a2pPart
  sourceFile = ./FST/M5-tslot-nut.step
  sourcePart = M5-tslot-nut
  subassemblyImport = false
  timeLastImport = 1.66336e+09
  updateColors = true
FEATURE [Part::FeaturePython] b_M5_tslot_nut1_001_003  label="M5-tslot-nut011"  # a2plus imported part (geometry in sourceFile) (typed FeaturePython)
  Placement = pos=(4.86821,510.062,30.0846) rot=(0.57735,-0.57735,-0.57735;2.0944rad)
  Visibility1 = true
  a2p_Version = V0.1
  fixedPosition = false
  objectType = a2pPart
  sourceFile = ./FST/M5-tslot-nut.step
  sourcePart = M5-tslot-nut
  subassemblyImport = false
  timeLastImport = 1.66336e+09
  updateColors = true
FEATURE [Part::FeaturePython] b_M5_tslot_nut1_001_004  label="M5-tslot-nut012"  # a2plus imported part (geometry in sourceFile) (typed FeaturePython)
  Placement = pos=(14.8982,510.062,30.0846) rot=(0.57735,-0.57735,0.57735;4.18879rad)
  Visibility1 = true
  a2p_Version = V0.1
  fixedPosition = false
  objectType = a2pPart
  sourceFile = ./FST/M5-tslot-nut.step
  sourcePart = M5-tslot-nut
  subassemblyImport = false
  timeLastImport = 1.66336e+09
  updateColors = true
FEATURE [Part::FeaturePython] b_Gates_2GT_20T_Toothed_Pulley1_001_003  label="GT2-pulley003"  # a2plus imported part (geometry in sourceFile) (typed FeaturePython)
  Placement = pos=(590.02,546.519,111.281) rot=(0.57735,0.57735,-0.57735;4.18879rad)
  Visibility1 = true
  a2p_Version = V0.1
  fixedPosition = false
  objectType = a2pPart
  sourceFile = ./cad/MISC/GT2-pulley.STEP
  sourcePart = GT2-pulley
  subassemblyImport = false
  timeLastImport = 1.64563e+09
  updateColors = true
FEATURE [Part::FeaturePython] Screw096  label="M3x8-Screw466"  # Fasteners workbench fastener (typed FeaturePython)
  Placement = pos=(574.58,531.04,85.25) rot=(0,0,-1;1.5708rad)
  Visibility1 = true
  diameter = 1
  invert = false
  leftHanded = false
  length = 1
  lengthCustom = 8
  matchOuter = false
  offset = 0
  thread = false
  type = 39
FEATURE [Part::FeaturePython] Screw093  label="M3x8-Screw467"  # Fasteners workbench fastener (typed FeaturePython)
  Placement = pos=(574.58,562.04,85.25) rot=(0,0,-1;1.5708rad)
  Visibility1 = true
  diameter = 1
  invert = false
  leftHanded = false
  length = 1
  lengthCustom = 8
  matchOuter = false
  offset = 0
  thread = false
  type = 39
FEATURE [Part::FeaturePython] Screw094  label="M3x8-Screw468"  # Fasteners workbench fastener (typed FeaturePython)
  Placement = pos=(605.58,562.04,85.25) rot=(0,0,-1;1.5708rad)
  Visibility1 = true
  diameter = 1
  invert = false
  leftHanded = false
  length = 1
  lengthCustom = 8
  matchOuter = false
  offset = 0
  thread = false
  type = 39
FEATURE [Part::FeaturePython] Screw095  label="M3x8-Screw469"  # Fasteners workbench fastener (typed FeaturePython)
  Placement = pos=(605.58,531.04,85.25) rot=(0,0,-1;1.5708rad)
  Visibility1 = true
  diameter = 1
  invert = false
  leftHanded = false
  length = 1
  lengthCustom = 8
  matchOuter = false
  offset = 0
  thread = false
  type = 39
FEATURE [Part::FeaturePython] Screw032  label="M5x10-Screw345"  # Fasteners workbench fastener (typed FeaturePython)
  Placement = pos=(606.44,510.06,30.11) rot=(0.57735,-0.57735,0.57735;4.18879rad)
  Visibility1 = true
  diameter = 6
  invert = false
  leftHanded = false
  length = 1
  lengthCustom = 10
  matchOuter = false
  offset = 0
  thread = false
  type = 33
FEATURE [Part::FeaturePython] Screw033  label="M5x10-Screw346"  # Fasteners workbench fastener (typed FeaturePython)
  Placement = pos=(573.54,510.06,30.11) rot=(0.57735,-0.57735,-0.57735;2.0944rad)
  Visibility1 = true
  diameter = 6
  invert = false
  leftHanded = false
  length = 1
  lengthCustom = 10
  matchOuter = false
  offset = 0
  thread = false
  type = 33
FEATURE [Part::FeaturePython] Screw034  label="M5x10-Screw347"  # Fasteners workbench fastener (typed FeaturePython)
  Placement = pos=(589.94,510.06,115.05) rot=(0,0,-1;1.5708rad)
  Visibility1 = true
  diameter = 6
  invert = false
  leftHanded = false
  length = 1
  lengthCustom = 10
  matchOuter = false
  offset = 0
  thread = false
  type = 33
FEATURE [Part::FeaturePython] b_M5_tslot_nut1_001_007  label="M5-tslot-nut013"  # a2plus imported part (geometry in sourceFile) (typed FeaturePython)
  Placement = pos=(595.338,510.062,30.0846) rot=(0.57735,-0.57735,0.57735;4.18879rad)
  Visibility1 = true
  a2p_Version = V0.1
  fixedPosition = false
  objectType = a2pPart
  sourceFile = ./FST/M5-tslot-nut.step
  sourcePart = M5-tslot-nut
  subassemblyImport = false
  timeLastImport = 1.66336e+09
  updateColors = true
FEATURE [Part::FeaturePython] b_M5_tslot_nut1_001_006  label="M5-tslot-nut014"  # a2plus imported part (geometry in sourceFile) (typed FeaturePython)
  Placement = pos=(585.028,510.062,30.0846) rot=(0.57735,-0.57735,-0.57735;2.0944rad)
  Visibility1 = true
  a2p_Version = V0.1
  fixedPosition = false
  objectType = a2pPart
  sourceFile = ./FST/M5-tslot-nut.step
  sourcePart = M5-tslot-nut
  subassemblyImport = false
  timeLastImport = 1.66336e+09
  updateColors = true
FEATURE [Part::FeaturePython] b_M5_tslot_nut1_001_005  label="M5-tslot-nut015"  # a2plus imported part (geometry in sourceFile) (typed FeaturePython)
  Placement = pos=(590.098,510.062,105.175) rot=(0,0,-1;1.5708rad)
  Visibility1 = true
  a2p_Version = V0.1
  fixedPosition = false
  objectType = a2pPart
  sourceFile = ./FST/M5-tslot-nut.step
  sourcePart = M5-tslot-nut
  subassemblyImport = false
  timeLastImport = 1.66336e+09
  updateColors = true
FEATURE [Part::FeaturePython] b_M5_tslot_nut1_001_024  label="M5-tslot-nut018"  # a2plus imported part (geometry in sourceFile) (typed FeaturePython)
  Placement = pos=(589.918,441.862,24.9746) rot=(0.707107,-0.707107,0;3.14159rad)
  Visibility1 = true
  a2p_Version = V0.1
  fixedPosition = false
  objectType = a2pPart
  sourceFile = ./FST/M5-tslot-nut.step
  sourcePart = M5-tslot-nut
  subassemblyImport = false
  timeLastImport = 1.66336e+09
  updateColors = true
FEATURE [Part::FeaturePython] b_M5_tslot_nut1_001_025  label="M5-tslot-nut019"  # a2plus imported part (geometry in sourceFile) (typed FeaturePython)
  Placement = pos=(589.918,456.992,9.95457) rot=(0,0.707107,-0.707107;3.14159rad)
  Visibility1 = true
  a2p_Version = V0.1
  fixedPosition = false
  objectType = a2pPart
  sourceFile = ./FST/M5-tslot-nut.step
  sourcePart = M5-tslot-nut
  subassemblyImport = false
  timeLastImport = 1.66336e+09
  updateColors = true
FEATURE [Part::FeaturePython] b_M5_tslot_nut1_001_026  label="M5-tslot-nut020"  # a2plus imported part (geometry in sourceFile) (typed FeaturePython)
  Placement = pos=(589.918,466.842,9.95457) rot=(0,0.707107,0.707107;3.14159rad)
  Visibility1 = true
  a2p_Version = V0.1
  fixedPosition = false
  objectType = a2pPart
  sourceFile = ./FST/M5-tslot-nut.step
  sourcePart = M5-tslot-nut
  subassemblyImport = false
  timeLastImport = 1.66336e+09
  updateColors = true
FEATURE [Part::FeaturePython] b_M5_tslot_nut1_001_027  label="M5-tslot-nut021"  # a2plus imported part (geometry in sourceFile) (typed FeaturePython)
  Placement = pos=(589.918,481.962,25.0246) rot=(0.707107,0.707107,0;3.14159rad)
  Visibility1 = true
  a2p_Version = V0.1
  fixedPosition = false
  objectType = a2pPart
  sourceFile = ./FST/M5-tslot-nut.step
  sourcePart = M5-tslot-nut
  subassemblyImport = false
  timeLastImport = 1.66336e+09
  updateColors = true
FEATURE [Part::FeaturePython] Screw081  label="M5x8-Screw177"  # Fasteners workbench fastener (typed FeaturePython)
  Placement = pos=(589.97,474.99,9.91) rot=(0,0.707107,0.707107;3.14159rad)
  Visibility1 = true
  diameter = 3
  invert = false
  leftHanded = false
  length = 0
  lengthCustom = 8
  matchOuter = false
  offset = 0
  thread = false
  type = 39
FEATURE [Part::FeaturePython] Screw082  label="M5x8-Screw178"  # Fasteners workbench fastener (typed FeaturePython)
  Placement = pos=(589.97,448.83,9.91) rot=(0,0.707107,-0.707107;3.14159rad)
  Visibility1 = true
  diameter = 3
  invert = false
  leftHanded = false
  length = 0
  lengthCustom = 8
  matchOuter = false
  offset = 0
  thread = false
  type = 39
FEATURE [Part::FeaturePython] Screw083  label="M5x8-Screw179"  # Fasteners workbench fastener (typed FeaturePython)
  Placement = pos=(589.88,441.8,16.93) rot=(0,1,0;3.14159rad)
  Visibility1 = true
  diameter = 3
  invert = false
  leftHanded = false
  length = 0
  lengthCustom = 8
  matchOuter = false
  offset = 0
  thread = false
  type = 39
FEATURE [Part::FeaturePython] Screw084  label="M5x8-Screw180"  # Fasteners workbench fastener (typed FeaturePython)
  Placement = pos=(589.88,481.98,16.93) rot=(0,1,0;3.14159rad)
  Visibility1 = true
  diameter = 3
  invert = false
  leftHanded = false
  length = 0
  lengthCustom = 8
  matchOuter = false
  offset = 0
  thread = false
  type = 39
FEATURE [Part::FeaturePython] Screw077  label="M5x8-Screw181"  # Fasteners workbench fastener (typed FeaturePython)
  Placement = pos=(10.02,474.99,9.97) rot=(0,0.707107,0.707107;3.14159rad)
  Visibility1 = true
  diameter = 3
  invert = false
  leftHanded = false
  length = 0
  lengthCustom = 8
  matchOuter = false
  offset = 0
  thread = false
  type = 39
FEATURE [Part::FeaturePython] Screw078  label="M5x8-Screw182"  # Fasteners workbench fastener (typed FeaturePython)
  Placement = pos=(10.02,482.04,16.85) rot=(0,1,0;3.14159rad)
  Visibility1 = true
  diameter = 3
  invert = false
  leftHanded = false
  length = 0
  lengthCustom = 8
  matchOuter = false
  offset = 0
  thread = false
  type = 39
FEATURE [Part::FeaturePython] Screw079  label="M5x8-Screw183"  # Fasteners workbench fastener (typed FeaturePython)
  Placement = pos=(10.02,442,16.85) rot=(0,1,0;3.14159rad)
  Visibility1 = true
  diameter = 3
  invert = false
  leftHanded = false
  length = 0
  lengthCustom = 8
  matchOuter = false
  offset = 0
  thread = false
  type = 39
FEATURE [Part::FeaturePython] Screw080  label="M5x8-Screw184"  # Fasteners workbench fastener (typed FeaturePython)
  Placement = pos=(10.02,448.9,9.98) rot=(0,0.707107,-0.707107;3.14159rad)
  Visibility1 = true
  diameter = 3
  invert = false
  leftHanded = false
  length = 0
  lengthCustom = 8
  matchOuter = false
  offset = 0
  thread = false
  type = 39
FEATURE [Part::FeaturePython] b_M5_tslot_nut1_001_020  label="M5-tslot-nut022"  # a2plus imported part (geometry in sourceFile) (typed FeaturePython)
  Placement = pos=(9.70821,456.952,9.95457) rot=(1,0,0;1.5708rad)
  Visibility1 = true
  a2p_Version = V0.1
  fixedPosition = false
  objectType = a2pPart
  sourceFile = ./FST/M5-tslot-nut.step
  sourcePart = M5-tslot-nut
  subassemblyImport = false
  timeLastImport = 1.66336e+09
  updateColors = true
FEATURE [Part::FeaturePython] b_M5_tslot_nut1_001_021  label="M5-tslot-nut023"  # a2plus imported part (geometry in sourceFile) (typed FeaturePython)
  Placement = pos=(9.70821,466.872,9.95457) rot=(-1,0,0;1.5708rad)
  Visibility1 = true
  a2p_Version = V0.1
  fixedPosition = false
  objectType = a2pPart
  sourceFile = ./FST/M5-tslot-nut.step
  sourcePart = M5-tslot-nut
  subassemblyImport = false
  timeLastImport = 1.66336e+09
  updateColors = true
FEATURE [Part::FeaturePython] b_M5_tslot_nut1_001_022  label="M5-tslot-nut024"  # a2plus imported part (geometry in sourceFile) (typed FeaturePython)
  Placement = pos=(9.70821,482.042,25.1246) rot=(0.707107,-0.707107,0;3.14159rad)
  Visibility1 = true
  a2p_Version = V0.1
  fixedPosition = false
  objectType = a2pPart
  sourceFile = ./FST/M5-tslot-nut.step
  sourcePart = M5-tslot-nut
  subassemblyImport = false
  timeLastImport = 1.66336e+09
  updateColors = true
FEATURE [Part::FeaturePython] b_M5_tslot_nut1_001_023  label="M5-tslot-nut025"  # a2plus imported part (geometry in sourceFile) (typed FeaturePython)
  Placement = pos=(9.70821,441.942,25.1246) rot=(0.707107,-0.707107,0;3.14159rad)
  Visibility1 = true
  a2p_Version = V0.1
  fixedPosition = false
  objectType = a2pPart
  sourceFile = ./FST/M5-tslot-nut.step
  sourcePart = M5-tslot-nut
  subassemblyImport = false
  timeLastImport = 1.66336e+09
  updateColors = true
FEATURE [Part::FeaturePython] b_2020CornerBracket1_001_002  label="corner-bracket"  # a2plus imported part (geometry in sourceFile) (typed FeaturePython)
  Placement = pos=(580.008,472.055,19.9154) rot=(0,1,0;3.14159rad)
  Visibility1 = true
  a2p_Version = V0.1
  fixedPosition = false
  objectType = a2pPart
  sourceFile = ./MISC/corner-bracket.step
  sourcePart = corner-bracket
  subassemblyImport = false
  timeLastImport = 1.66336e+09
  updateColors = true
FEATURE [Part::FeaturePython] b_2020CornerBracket1_001_003  label="corner-bracket001"  # a2plus imported part (geometry in sourceFile) (typed FeaturePython)
  Placement = pos=(599.918,451.845,19.9154) rot=(1,0,0;3.14159rad)
  Visibility1 = true
  a2p_Version = V0.1
  fixedPosition = false
  objectType = a2pPart
  sourceFile = ./MISC/corner-bracket.step
  sourcePart = corner-bracket
  subassemblyImport = false
  timeLastImport = 1.66336e+09
  updateColors = true
FEATURE [Part::FeaturePython] b_2020CornerBracket1_001_004  label="corner-bracket002"  # a2plus imported part (geometry in sourceFile) (typed FeaturePython)
  Placement = pos=(20.0179,451.845,19.9154) rot=(1,0,0;3.14159rad)
  Visibility1 = true
  a2p_Version = V0.1
  fixedPosition = false
  objectType = a2pPart
  sourceFile = ./MISC/corner-bracket.step
  sourcePart = corner-bracket
  subassemblyImport = false
  timeLastImport = 1.66336e+09
  updateColors = true
FEATURE [Part::FeaturePython] b_2020CornerBracket1_001_005  label="corner-bracket003"  # a2plus imported part (geometry in sourceFile) (typed FeaturePython)
  Placement = pos=(0.00786224,472.055,19.9154) rot=(0,1,0;3.14159rad)
  Visibility1 = true
  a2p_Version = V0.1
  fixedPosition = false
  objectType = a2pPart
  sourceFile = ./MISC/corner-bracket.step
  sourcePart = corner-bracket
  subassemblyImport = false
  timeLastImport = 1.66336e+09
  updateColors = true
FEATURE [Part::FeaturePython] b_OTS_0009_20x20_v_slot_600mm1_001_006  label="vslot-extrusion-20mmx20mmx600mm006"  # a2plus imported part (geometry in sourceFile) (typed FeaturePython)
  Placement = pos=(1.05e-13,471.91,0) rot=(0.57735,-0.57735,-0.57735;2.0944rad)
  Visibility1 = true
  a2p_Version = V0.1
  fixedPosition = true
  objectType = a2pPart
  sourceFile = ./MISC/vslot-extrusion-20mmx20mmx600mm.step
  sourcePart = vslot-extrusion-20mmx20mmx600mm
  subassemblyImport = false
  timeLastImport = 1.66336e+09
  updateColors = true
FEATURE [Part::FeaturePython] b_2020CornerBracket1_001_001  label="corner-bracket004"  # a2plus imported part (geometry in sourceFile) (typed FeaturePython)
  Placement = pos=(580.008,0.0247107,19.9154) rot=(0,1,0;3.14159rad)
  Visibility1 = true
  a2p_Version = V0.1
  fixedPosition = false
  objectType = a2pPart
  sourceFile = ./MISC/corner-bracket.step
  sourcePart = corner-bracket
  subassemblyImport = false
  timeLastImport = 1.66336e+09
  updateColors = true
FEATURE [Part::FeaturePython] Screw073  label="M5x8-Screw185"  # Fasteners workbench fastener (typed FeaturePython)
  Placement = pos=(10.02,3.07,9.97) rot=(0,0.707107,0.707107;3.14159rad)
  Visibility1 = true
  diameter = 3
  invert = false
  leftHanded = false
  length = 0
  lengthCustom = 8
  matchOuter = false
  offset = 0
  thread = false
  type = 39
FEATURE [Part::FeaturePython] Screw074  label="M5x8-Screw"  # Fasteners workbench fastener (typed FeaturePython)
  Placement = pos=(10.02,10.13,17.05) rot=(0,1,0;3.14159rad)
  Visibility1 = true
  diameter = 3
  invert = false
  leftHanded = false
  length = 0
  lengthCustom = 8
  matchOuter = false
  offset = 0
  thread = false
  type = 39
FEATURE [Part::FeaturePython] b_2020CornerBracket1_001_  label="corner-bracket005"  # a2plus imported part (geometry in sourceFile) (typed FeaturePython)
  Placement = pos=(-0.0521378,0.0247107,20.0654) rot=(0,1,0;3.14159rad)
  Visibility1 = true
  a2p_Version = V0.1
  fixedPosition = false
  objectType = a2pPart
  sourceFile = ./MISC/corner-bracket.step
  sourcePart = corner-bracket
  subassemblyImport = false
  timeLastImport = 1.66336e+09
  updateColors = true
FEATURE [Part::FeaturePython] b_M5_tslot_nut1_001_016  label="M5-tslot-nut026"  # a2plus imported part (geometry in sourceFile) (typed FeaturePython)
  Placement = pos=(9.85821,-4.9684,9.95457) rot=(-1,0,0;1.5708rad)
  Visibility1 = true
  a2p_Version = V0.1
  fixedPosition = false
  objectType = a2pPart
  sourceFile = ./FST/M5-tslot-nut.step
  sourcePart = M5-tslot-nut
  subassemblyImport = false
  timeLastImport = 1.66336e+09
  updateColors = true
FEATURE [Part::FeaturePython] b_M5_tslot_nut1_001_017  label="M5-tslot-nut027"  # a2plus imported part (geometry in sourceFile) (typed FeaturePython)
  Placement = pos=(10.0282,10.1416,24.9946) rot=(0.707107,0.707107,0;3.14159rad)
  Visibility1 = true
  a2p_Version = V0.1
  fixedPosition = false
  objectType = a2pPart
  sourceFile = ./FST/M5-tslot-nut.step
  sourcePart = M5-tslot-nut
  subassemblyImport = false
  timeLastImport = 1.66336e+09
  updateColors = true
FEATURE [Part::FeaturePython] Screw075  label="M5x8-Screw186"  # Fasteners workbench fastener (typed FeaturePython)
  Placement = pos=(589.77,3.07,9.97) rot=(0,0.707107,0.707107;3.14159rad)
  Visibility1 = true
  diameter = 3
  invert = false
  leftHanded = false
  length = 0
  lengthCustom = 8
  matchOuter = false
  offset = 0
  thread = false
  type = 39
FEATURE [Part::FeaturePython] Screw076  label="M5x8-Screw187"  # Fasteners workbench fastener (typed FeaturePython)
  Placement = pos=(589.89,9.87,16.9) rot=(0,1,0;3.14159rad)
  Visibility1 = true
  diameter = 3
  invert = false
  leftHanded = false
  length = 0
  lengthCustom = 8
  matchOuter = false
  offset = 0
  thread = false
  type = 39
FEATURE [Part::FeaturePython] b_M5_tslot_nut1_001_018  label="M5-tslot-nut028"  # a2plus imported part (geometry in sourceFile) (typed FeaturePython)
  Placement = pos=(589.718,-4.9684,9.95457) rot=(-1,0,0;1.5708rad)
  Visibility1 = true
  a2p_Version = V0.1
  fixedPosition = false
  objectType = a2pPart
  sourceFile = ./FST/M5-tslot-nut.step
  sourcePart = M5-tslot-nut
  subassemblyImport = false
  timeLastImport = 1.66336e+09
  updateColors = true
FEATURE [Part::FeaturePython] b_M5_tslot_nut1_001_019  label="M5-tslot-nut029"  # a2plus imported part (geometry in sourceFile) (typed FeaturePython)
  Placement = pos=(589.718,10.0016,24.5446) rot=(0.707107,0.707107,0;3.14159rad)
  Visibility1 = true
  a2p_Version = V0.1
  fixedPosition = false
  objectType = a2pPart
  sourceFile = ./FST/M5-tslot-nut.step
  sourcePart = M5-tslot-nut
  subassemblyImport = false
  timeLastImport = 1.66336e+09
  updateColors = true
FEATURE [Part::FeaturePython] b_OTS_0009_20x20_v_slot_600mm1_001_002  label="vslot-extrusion-20mmx20mmx600mm"  # a2plus imported part (geometry in sourceFile) (typed FeaturePython)
  Placement = pos=(-0.00959473,-79.9716,90.0176) rot=(1,0,0;1.5708rad)
  Visibility1 = true
  a2p_Version = V0.1
  fixedPosition = true
  objectType = a2pPart
  sourceFile = ./MISC/vslot-extrusion-20mmx20mmx600mm.step
  sourcePart = vslot-extrusion-20mmx20mmx600mm
  subassemblyImport = false
  timeLastImport = 1.66336e+09
  updateColors = true
FEATURE [Part::FeaturePython] b_OTS_0009_20x20_v_slot_600mm1_001_004  label="vslot-extrusion-20mmx20mmx600mm001"  # a2plus imported part (geometry in sourceFile) (typed FeaturePython)
  Placement = pos=(580.068,-79.9849,20.0043) rot=(1,0,0;1.5708rad)
  Visibility1 = true
  a2p_Version = V0.1
  fixedPosition = false
  objectType = a2pPart
  sourceFile = ./MISC/vslot-extrusion-20mmx20mmx600mm.step
  sourcePart = vslot-extrusion-20mmx20mmx600mm
  subassemblyImport = false
  timeLastImport = 1.66336e+09
  updateColors = true
FEATURE [Part::FeaturePython] b_OTS_0009_20x20_v_slot_600mm1_001_005  label="vslot-extrusion-20mmx20mmx600mm002"  # a2plus imported part (geometry in sourceFile) (typed FeaturePython)
  Placement = pos=(580.088,-79.9481,90.0477) rot=(1,0,0;1.5708rad)
  Visibility1 = true
  a2p_Version = V0.1
  fixedPosition = false
  objectType = a2pPart
  sourceFile = ./MISC/vslot-extrusion-20mmx20mmx600mm.step
  sourcePart = vslot-extrusion-20mmx20mmx600mm
  subassemblyImport = false
  timeLastImport = 1.66336e+09
  updateColors = true
FEATURE [Part::FeaturePython] b_OTS_0009_20x20_v_slot_600mm1_001_001  label="vslot-extrusion-20mmx20mmx600mm003"  # a2plus imported part (geometry in sourceFile) (typed FeaturePython)
  Placement = pos=(-0.0637482,-80.0926,20.0674) rot=(1,0,0;1.5708rad)
  Visibility1 = true
  a2p_Version = V0.1
  fixedPosition = false
  objectType = a2pPart
  sourceFile = ./MISC/vslot-extrusion-20mmx20mmx600mm.step
  sourcePart = vslot-extrusion-20mmx20mmx600mm
  subassemblyImport = false
  timeLastImport = 1.66336e+09
  updateColors = true
FEATURE [Part::FeaturePython] b_OTS_0009_20x20_v_slot_600mm1_001_  label="vslot-extrusion-20mmx20mmx600mm004"  # a2plus imported part (geometry in sourceFile) (typed FeaturePython)
  Placement = pos=(0,0,0) rot=(0.57735,-0.57735,-0.57735;2.0944rad)
  Visibility1 = true
  a2p_Version = V0.1
  fixedPosition = true
  objectType = a2pPart
  sourceFile = ./MISC/vslot-extrusion-20mmx20mmx600mm.step
  sourcePart = vslot-extrusion-20mmx20mmx600mm
  subassemblyImport = false
  timeLastImport = 1.66336e+09
  updateColors = true
FEATURE [Part::FeaturePython] Screw174  label="M3x16-Screw091"  # Fasteners workbench fastener (typed FeaturePython)
  Placement = pos=(300.41,74.04,43.1) rot=(0,0,-1;1.5708rad)
  Visibility1 = true
  diameter = 4
  invert = false
  leftHanded = false
  length = 10
  lengthCustom = 16
  matchOuter = false
  offset = 0
  thread = false
  type = 33
FEATURE [Part::FeaturePython] Screw175  label="M3x16-Screw092"  # Fasteners workbench fastener (typed FeaturePython)
  Placement = pos=(300.41,134.05,43.1) rot=(0,0,-1;1.5708rad)
  Visibility1 = true
  diameter = 4
  invert = false
  leftHanded = false
  length = 10
  lengthCustom = 16
  matchOuter = false
  offset = 0
  thread = false
  type = 33
FEATURE [Part::FeaturePython] Screw176  label="M3x16-Screw093"  # Fasteners workbench fastener (typed FeaturePython)
  Placement = pos=(330.33,104.04,43.1) rot=(0,0,-1;1.5708rad)
  Visibility1 = true
  diameter = 4
  invert = false
  leftHanded = false
  length = 10
  lengthCustom = 16
  matchOuter = false
  offset = 0
  thread = false
  type = 33
FEATURE [Part::FeaturePython] Screw177  label="M3x16-Screw094"  # Fasteners workbench fastener (typed FeaturePython)
  Placement = pos=(270.39,104,43.1) rot=(0,0,-1;1.5708rad)
  Visibility1 = true
  diameter = 4
  invert = false
  leftHanded = false
  length = 10
  lengthCustom = 16
  matchOuter = false
  offset = 0
  thread = false
  type = 33
FEATURE [Part::FeaturePython] Nut052  label="M3-Nut497"  # Fasteners workbench fastener (typed FeaturePython)
  Placement = pos=(300.387,74.0612,29.47) rot=(0.707107,-0.707107,0;3.14159rad)
  Visibility1 = true
  diameter = 4
  invert = false
  leftHanded = false
  matchOuter = false
  offset = 0
  thread = false
  type = 7
FEATURE [Part::FeaturePython] Nut053  label="M3-Nut498"  # Fasteners workbench fastener (typed FeaturePython)
  Placement = pos=(270.417,104.031,29.77) rot=(1,0,0;3.14159rad)
  Visibility1 = true
  diameter = 4
  invert = false
  leftHanded = false
  matchOuter = false
  offset = 0
  thread = false
  type = 7
FEATURE [Part::FeaturePython] Nut054  label="M3-Nut499"  # Fasteners workbench fastener (typed FeaturePython)
  Placement = pos=(330.287,104.031,29.7) rot=(1,0,0;3.14159rad)
  Visibility1 = true
  diameter = 4
  invert = false
  leftHanded = false
  matchOuter = false
  offset = 0
  thread = false
  type = 7
FEATURE [Part::FeaturePython] Nut055  label="M3-Nut500"  # Fasteners workbench fastener (typed FeaturePython)
  Placement = pos=(300.387,134.051,29.55) rot=(0.707107,-0.707107,0;3.14159rad)
  Visibility1 = true
  diameter = 4
  invert = false
  leftHanded = false
  matchOuter = false
  offset = 0
  thread = false
  type = 7
FEATURE [Part::FeaturePython] Screw139  label="M3x10-Screw"  # Fasteners workbench fastener (typed FeaturePython)
  Placement = pos=(465.5,148.95,42.98) rot=(0,0,1;0rad)
  Visibility1 = true
  diameter = 1
  invert = false
  leftHanded = false
  length = 2
  lengthCustom = 10
  matchOuter = false
  offset = 0
  thread = false
  type = 39
FEATURE [Part::FeaturePython] Screw142  label="M3x10-Screw092"  # Fasteners workbench fastener (typed FeaturePython)
  Placement = pos=(495.4,148.95,42.98) rot=(0,0,1;0rad)
  Visibility1 = true
  diameter = 1
  invert = false
  leftHanded = false
  length = 2
  lengthCustom = 10
  matchOuter = false
  offset = 0
  thread = false
  type = 39
FEATURE [Part::FeaturePython] Nut057  label="M3-Nut470"  # Fasteners workbench fastener (typed FeaturePython)
  Placement = pos=(495.5,148.95,35.75) rot=(1,0,0;3.14159rad)
  Visibility1 = true
  diameter = 4
  invert = false
  leftHanded = false
  matchOuter = false
  offset = 0
  thread = false
  type = 7
FEATURE [Part::FeaturePython] Nut058  label="M3-Nut471"  # Fasteners workbench fastener (typed FeaturePython)
  Placement = pos=(465.6,148.95,35.75) rot=(1,0,0;3.14159rad)
  Visibility1 = true
  diameter = 4
  invert = false
  leftHanded = false
  matchOuter = false
  offset = 0
  thread = false
  type = 7
FEATURE [Part::FeaturePython] Screw178  label="M5x8-Screw188"  # Fasteners workbench fastener (typed FeaturePython)
  Placement = pos=(10.02,54.33,43.32) rot=(0,0,1;3.14159rad)
  Visibility1 = true
  diameter = 3
  invert = false
  leftHanded = false
  length = 0
  lengthCustom = 8
  matchOuter = false
  offset = 0
  thread = false
  type = 39
FEATURE [Part::FeaturePython] Screw179  label="M5x8-Screw189"  # Fasteners workbench fastener (typed FeaturePython)
  Placement = pos=(10.14,153.93,43.19) rot=(0,0,1;3.14159rad)
  Visibility1 = true
  diameter = 3
  invert = false
  leftHanded = false
  length = 0
  lengthCustom = 8
  matchOuter = false
  offset = 0
  thread = false
  type = 39
FEATURE [Part::FeaturePython] Screw180  label="M5x8-Screw190"  # Fasteners workbench fastener (typed FeaturePython)
  Placement = pos=(590.11,153.93,43.19) rot=(0,0,1;3.14159rad)
  Visibility1 = true
  diameter = 3
  invert = false
  leftHanded = false
  length = 0
  lengthCustom = 8
  matchOuter = false
  offset = 0
  thread = false
  type = 39
FEATURE [Part::FeaturePython] Screw134  label="M5x8-Screw191"  # Fasteners workbench fastener (typed FeaturePython)
  Placement = pos=(590.11,54.35,43.19) rot=(0,0,1;3.14159rad)
  Visibility1 = true
  diameter = 3
  invert = false
  leftHanded = false
  length = 0
  lengthCustom = 8
  matchOuter = false
  offset = 0
  thread = false
  type = 39
FEATURE [Part::FeaturePython] b_FDM_0024_nozzle_holder_001_  label="nozzle-rack"  # a2plus imported part (geometry in sourceFile) (typed FeaturePython)
  Placement = pos=(115.152,141.953,42.9477) rot=(1,0,0;1.5708rad)
  a2p_Version = V0.1
  fixedPosition = false
  objectType = a2pPart
  sourceFile = ./FDM/nozzle-rack.FCStd
  sourcePart = Body
  subassemblyImport = false
  timeLastImport = 1.66336e+09
  updateColors = true
FEATURE [Part::FeaturePython] Nut064  label="M3-Nut541"  # Fasteners workbench fastener (typed FeaturePython)
  Placement = pos=(120.424,73.9492,47.93) rot=(1,0,0;3.14159rad)
  Visibility1 = true
  diameter = 4
  invert = false
  leftHanded = false
  matchOuter = false
  offset = 0
  thread = false
  type = 7
FEATURE [Part::FeaturePython] Nut066  label="M3-Nut542"  # Fasteners workbench fastener (typed FeaturePython)
  Placement = pos=(120.424,133.989,47.93) rot=(1,0,0;3.14159rad)
  Visibility1 = true
  diameter = 4
  invert = false
  leftHanded = false
  matchOuter = false
  offset = 0
  thread = false
  type = 7
FEATURE [Part::FeaturePython] Screw156  label="M3x8-Screw537"  # Fasteners workbench fastener (typed FeaturePython)
  Placement = pos=(120.424,73.958,39.94) rot=(0,1,0;3.14159rad)
  Visibility1 = true
  diameter = 1
  invert = false
  leftHanded = false
  length = 1
  lengthCustom = 8
  matchOuter = false
  offset = 0
  thread = false
  type = 39
FEATURE [Part::FeaturePython] Screw158  label="M3x8-Screw538"  # Fasteners workbench fastener (typed FeaturePython)
  Placement = pos=(120.424,133.998,39.94) rot=(0,1,0;3.14159rad)
  Visibility1 = true
  diameter = 1
  invert = false
  leftHanded = false
  length = 1
  lengthCustom = 8
  matchOuter = false
  offset = 0
  thread = false
  type = 39
FEATURE [Part::FeaturePython] Screw159  label="M2.5x8-Screw152"  # Fasteners workbench fastener (typed FeaturePython)
  Placement = pos=(314.37,118.05,-11.44) rot=(0.707107,0.707107,0;3.14159rad)
  Visibility1 = true
  diameter = 3
  invert = false
  leftHanded = false
  length = 3
  lengthCustom = 8
  matchOuter = false
  offset = 0
  thread = false
  type = 33
FEATURE [Part::FeaturePython] Screw160  label="M2.5x8-Screw153"  # Fasteners workbench fastener (typed FeaturePython)
  Placement = pos=(286.39,118.05,-11.44) rot=(0.707107,0.707107,0;3.14159rad)
  Visibility1 = true
  diameter = 3
  invert = false
  leftHanded = false
  length = 3
  lengthCustom = 8
  matchOuter = false
  offset = 0
  thread = false
  type = 33
FEATURE [Part::FeaturePython] Screw161  label="M2.5x8-Screw154"  # Fasteners workbench fastener (typed FeaturePython)
  Placement = pos=(286.39,90.04,-11.44) rot=(0.707107,0.707107,0;3.14159rad)
  Visibility1 = true
  diameter = 3
  invert = false
  leftHanded = false
  length = 3
  lengthCustom = 8
  matchOuter = false
  offset = 0
  thread = false
  type = 33
FEATURE [Part::FeaturePython] Screw162  label="M2.5x8-Screw155"  # Fasteners workbench fastener (typed FeaturePython)
  Placement = pos=(314.37,90.04,-11.44) rot=(0.707107,0.707107,0;3.14159rad)
  Visibility1 = true
  diameter = 3
  invert = false
  leftHanded = false
  length = 3
  lengthCustom = 8
  matchOuter = false
  offset = 0
  thread = false
  type = 33
FEATURE [Part::FeaturePython] b_CSM_0001_staging_plate_001_  label="staging-plate"  # a2plus imported part (geometry in sourceFile) (typed FeaturePython)
  Placement = pos=(0.410743,163.951,42.9729) rot=(1,0,0;3.14159rad)
  Visibility1 = true
  a2p_Version = V0.1
  fixedPosition = false
  objectType = a2pPart
  sourceFile = ./cad/PCB/staging-plate.FCStd
  sourcePart = Body
  subassemblyImport = false
  timeLastImport = 1.65531e+09
  updateColors = true
FEATURE [Part::FeaturePython] b_M5_tslot_nut1_001_030  label="M5-tslot-nut030"  # a2plus imported part (geometry in sourceFile) (typed FeaturePython)
  Placement = pos=(589.718,54.2216,34.9746) rot=(0,0,1;1.5708rad)
  Visibility1 = true
  a2p_Version = V0.1
  fixedPosition = false
  objectType = a2pPart
  sourceFile = ./FST/M5-tslot-nut.step
  sourcePart = M5-tslot-nut
  subassemblyImport = false
  timeLastImport = 1.66336e+09
  updateColors = true
FEATURE [Part::FeaturePython] b_M5_tslot_nut1_001_031  label="M5-tslot-nut031"  # a2plus imported part (geometry in sourceFile) (typed FeaturePython)
  Placement = pos=(589.718,153.872,34.9746) rot=(0,0,1;1.5708rad)
  Visibility1 = true
  a2p_Version = V0.1
  fixedPosition = false
  objectType = a2pPart
  sourceFile = ./FST/M5-tslot-nut.step
  sourcePart = M5-tslot-nut
  subassemblyImport = false
  timeLastImport = 1.66336e+09
  updateColors = true
FEATURE [Part::FeaturePython] b_M5_tslot_nut1_001_032  label="M5-tslot-nut032"  # a2plus imported part (geometry in sourceFile) (typed FeaturePython)
  Placement = pos=(9.85821,153.872,34.9746) rot=(0,0,1;1.5708rad)
  Visibility1 = true
  a2p_Version = V0.1
  fixedPosition = false
  objectType = a2pPart
  sourceFile = ./FST/M5-tslot-nut.step
  sourcePart = M5-tslot-nut
  subassemblyImport = false
  timeLastImport = 1.66336e+09
  updateColors = true
FEATURE [Part::FeaturePython] b_M5_tslot_nut1_001_033  label="M5-tslot-nut033"  # a2plus imported part (geometry in sourceFile) (typed FeaturePython)
  Placement = pos=(9.85821,54.2716,34.9746) rot=(0,0,1;1.5708rad)
  Visibility1 = true
  a2p_Version = V0.1
  fixedPosition = false
  objectType = a2pPart
  sourceFile = ./FST/M5-tslot-nut.step
  sourcePart = M5-tslot-nut
  subassemblyImport = false
  timeLastImport = 1.66336e+09
  updateColors = true
FEATURE [Part::FeaturePython] b_OTS_0003_00_vacuum_pump_001_001  label="vacuum-pump"  # a2plus imported part (geometry in sourceFile) (typed FeaturePython)
  Placement = pos=(481.281,133.936,10.2256) rot=(-0.707107,0,0.707107;3.14159rad)
  Visibility1 = true
  a2p_Version = V0.1
  fixedPosition = false
  objectType = a2pPart
  sourceFile = ./MISC/vacuum-pump.FCStd
  sourcePart = Body
  subassemblyImport = false
  timeLastImport = 1.65531e+09
  updateColors = true
FEATURE [Part::FeaturePython] b_FDM_0025_pump_mount_001_001  label="pump-mount"  # a2plus imported part (geometry in sourceFile) (typed FeaturePython)
  Placement = pos=(452.615,163.524,-15.2591) rot=(0,0,-1;1.5708rad)
  Visibility1 = true
  a2p_Version = V0.1
  fixedPosition = false
  objectType = a2pPart
  sourceFile = ./FDM/pump-mount.FCStd
  sourcePart = Body
  subassemblyImport = false
  timeLastImport = 1.66336e+09
  updateColors = true
FEATURE [Part::FeaturePython] Nut  label="M5-Nut687"  # Fasteners workbench fastener (typed FeaturePython)
  Placement = pos=(443.743,194.103,98.994) rot=(-1,0,0;1.5708rad)
  baseObject = -> Screw044 [Edge16]
  diameter = 3
  invert = true
  leftHanded = false
  matchOuter = false
  offset = -6
  thread = false
  type = 5
FEATURE [Part::FeaturePython] Screw185  label="M2.5x20-Screw"  # Fasteners workbench fastener (typed FeaturePython)
  Placement = pos=(427.074,238.502,103.069) rot=(0,0,-1;1.5708rad)
  baseObject = -> b_FDM_0014_down_camera_mount_001_ [Edge333]
  diameter = 3
  invert = false
  leftHanded = false
  length = 8
  lengthCustom = 20
  matchOuter = true
  offset = 2
  thread = false
  type = 34
FEATURE [Part::FeaturePython] Screw186  label="M2.5x20-Screw076"  # Fasteners workbench fastener (typed FeaturePython)
  Placement = pos=(461.074,238.502,103.069) rot=(0,0,-1;1.5708rad)
  baseObject = -> b_FDM_0014_down_camera_mount_001_ [Edge337]
  diameter = 3
  invert = false
  leftHanded = false
  length = 8
  lengthCustom = 20
  matchOuter = true
  offset = 2
  thread = false
  type = 34
FEATURE [Part::FeaturePython] Screw187  label="M2.5x20-Screw077"  # Fasteners workbench fastener (typed FeaturePython)
  Placement = pos=(461.074,204.502,103.069) rot=(0,0,-1;1.5708rad)
  baseObject = -> b_FDM_0014_down_camera_mount_001_ [Edge107]
  diameter = 3
  invert = false
  leftHanded = false
  length = 8
  lengthCustom = 20
  matchOuter = true
  offset = 2
  thread = false
  type = 34
FEATURE [Part::FeaturePython] Screw188  label="M2.5x20-Screw078"  # Fasteners workbench fastener (typed FeaturePython)
  Placement = pos=(427.074,204.502,103.069) rot=(0,0,-1;1.5708rad)
  baseObject = -> b_FDM_0014_down_camera_mount_001_ [Edge343]
  diameter = 3
  invert = false
  leftHanded = false
  length = 8
  lengthCustom = 20
  matchOuter = true
  offset = 2
  thread = false
  type = 34
FEATURE [Part::FeaturePython] Screw189  label="M3x14-Screw192"  # Fasteners workbench fastener (typed FeaturePython)
  Placement = pos=(421.574,236.252,118.069) rot=(0,0.707107,0.707107;3.14159rad)
  baseObject = -> b_FDM_0014_down_camera_mount_001_ [Edge355]
  diameter = 1
  invert = false
  leftHanded = false
  length = 4
  lengthCustom = 14
  matchOuter = true
  offset = 0
  thread = false
  type = 40
FEATURE [App::DocumentObjectGroup] Group013  label="GT2BeltClamp"
  Group = -> [b_FDM_0027_belt_clamp_001_003,b_FDM_0027_belt_clamp_001_002,Screw040,Screw041,Screw038,Screw039,Nut023,Nut024,Nut022,Nut021]
FEATURE [App::DocumentObjectGroup] Group014  label="Z-Motor"
  Group = -> [b_Nema_17_42A02C_v21_001_,b_Gates_2GT_20T_Toothed_Pulley1_001_,Screw085,Screw086,Screw087,Screw088]
FEATURE [Part::FeaturePython] Screw155  label="M3x10-Screw096"  # Fasteners workbench fastener (typed FeaturePython)
  Placement = pos=(135.31,58.83,42.98) rot=(0,0,1;0rad)
  Visibility1 = true
  diameter = 1
  invert = false
  leftHanded = false
  length = 9
  lengthCustom = 10
  matchOuter = false
  offset = 0
  thread = false
  type = 39
FEATURE [Part::FeaturePython] Screw154  label="M3x10-Screw095"  # Fasteners workbench fastener (typed FeaturePython)
  Placement = pos=(135.31,148.75,42.98) rot=(0,0,1;0rad)
  Visibility1 = true
  diameter = 1
  invert = false
  leftHanded = false
  length = 9
  lengthCustom = 10
  matchOuter = false
  offset = 0
  thread = false
  type = 39
FEATURE [Part::FeaturePython] Screw153  label="M3x10-Screw094"  # Fasteners workbench fastener (typed FeaturePython)
  Placement = pos=(45.39,148.75,42.98) rot=(0,0,1;0rad)
  Visibility1 = true
  diameter = 1
  invert = false
  leftHanded = false
  length = 9
  lengthCustom = 10
  matchOuter = false
  offset = 0
  thread = false
  type = 39
FEATURE [Part::FeaturePython] Screw152  label="M3x10-Screw093"  # Fasteners workbench fastener (typed FeaturePython)
  Placement = pos=(45.39,58.83,42.98) rot=(0,0,1;0rad)
  Visibility1 = true
  diameter = 1
  invert = false
  leftHanded = false
  length = 9
  lengthCustom = 10
  matchOuter = false
  offset = 0
  thread = false
  type = 39
FEATURE [Part::FeaturePython] Screw191  label="M3x30-Screw164"  # Fasteners workbench fastener (typed FeaturePython)
  Placement = pos=(45.39,58.97,-8.5) rot=(0.707107,-0.707107,0;3.14159rad)
  diameter = 4
  invert = false
  leftHanded = false
  length = 9
  lengthCustom = 30
  matchOuter = false
  offset = 0
  thread = false
  type = 34
FEATURE [Part::FeaturePython] Screw192  label="M3x10-Screw109"  # Fasteners workbench fastener (typed FeaturePython)
  Placement = pos=(45.39,148.6,9.5) rot=(0.707107,-0.707107,0;3.14159rad)
  diameter = 1
  invert = false
  leftHanded = false
  length = 2
  lengthCustom = 10
  matchOuter = false
  offset = 0
  thread = false
  type = 40
  expr: .Placement.Base.y = 148.6
FEATURE [Part::FeaturePython] Screw193  label="M3x30-Screw165"  # Fasteners workbench fastener (typed FeaturePython)
  Placement = pos=(135.29,148.62,-8.5) rot=(0.707107,-0.707107,0;3.14159rad)
  diameter = 4
  invert = false
  leftHanded = false
  length = 9
  lengthCustom = 30
  matchOuter = false
  offset = 0
  thread = false
  type = 34
FEATURE [Part::FeaturePython] Screw194  label="M3x10-Screw111"  # Fasteners workbench fastener (typed FeaturePython)
  Placement = pos=(135.29,58.77,9.5) rot=(0.707107,-0.707107,0;3.14159rad)
  diameter = 1
  invert = false
  leftHanded = false
  length = 2
  lengthCustom = 10
  matchOuter = false
  offset = 0
  thread = false
  type = 40
FEATURE [Part::FeaturePython] PcbSpacer  label="M3x5.5x25-Spacer"  # Fasteners workbench fastener (typed FeaturePython)
  Placement = pos=(45.39,148.92,40) rot=(0.707107,-0.707107,0;3.14159rad)
  diameter = 2
  invert = false
  leftHanded = false
  length = 19
  lengthCustom = 5
  matchOuter = false
  offset = 0
  thread = false
  type = 0
  width = 1
FEATURE [Part::FeaturePython] PcbSpacer001  label="M3x5.5x25-Spacer001"  # Fasteners workbench fastener (typed FeaturePython)
  Placement = pos=(135.34,148.92,40) rot=(0.707107,-0.707107,0;3.14159rad)
  diameter = 2
  invert = false
  leftHanded = false
  length = 19
  lengthCustom = 5
  matchOuter = false
  offset = 0
  thread = false
  type = 0
  width = 1
FEATURE [Part::FeaturePython] PcbSpacer002  label="M3x5.5x25-Spacer002"  # Fasteners workbench fastener (typed FeaturePython)
  Placement = pos=(45.39,58.97,40) rot=(0.707107,-0.707107,0;3.14159rad)
  diameter = 2
  invert = false
  leftHanded = false
  length = 19
  lengthCustom = 5
  matchOuter = false
  offset = 0
  thread = false
  type = 0
  width = 1
FEATURE [Part::FeaturePython] PcbSpacer003  label="M3x5.5x25-Spacer003"  # Fasteners workbench fastener (typed FeaturePython)
  Placement = pos=(135.34,58.77,40) rot=(0.707107,-0.707107,0;3.14159rad)
  diameter = 2
  invert = false
  leftHanded = false
  length = 19
  lengthCustom = 5
  matchOuter = false
  offset = 0
  thread = false
  type = 0
  width = 1
FEATURE [Part::FeaturePython] b_FDM_0055_datum_board_mount_001_  label="datum-board-mount"  # a2plus imported part (geometry in sourceFile) (typed FeaturePython)
  Placement = pos=(270.391,133.979,42.9044) rot=(0,0,1;0rad)
  a2p_Version = V0.1
  fixedPosition = false
  objectType = a2pPart
  sourceFile = ./FDM/datum-board-mount.FCStd
  sourcePart = Body
  subassemblyImport = false
  timeLastImport = 1.65531e+09
  updateColors = true
FEATURE [Part::FeaturePython] Screw195  label="M3x16-Screw087"  # Fasteners workbench fastener (typed FeaturePython)
  Placement = pos=(330.39,133.94,52.9) rot=(0,0,1;1.5708rad)
  Visibility1 = true
  diameter = 4
  invert = false
  leftHanded = false
  length = 6
  lengthCustom = 16
  matchOuter = false
  offset = 0
  thread = false
  type = 33
FEATURE [Part::FeaturePython] Nut088  label="M3-Nut475"  # Fasteners workbench fastener (typed FeaturePython)
  Placement = pos=(330.41,133.951,37.57) rot=(0,0,-1;1.5708rad)
  diameter = 4
  invert = false
  leftHanded = false
  matchOuter = false
  offset = -2
  thread = false
  type = 7
FEATURE [Part::FeaturePython] Screw196  label="M3x16-Screw088"  # Fasteners workbench fastener (typed FeaturePython)
  Placement = pos=(270.39,133.94,52.9) rot=(0,0,1;1.5708rad)
  Visibility1 = true
  diameter = 4
  invert = false
  leftHanded = false
  length = 6
  lengthCustom = 16
  matchOuter = false
  offset = 0
  thread = false
  type = 33
FEATURE [Part::FeaturePython] Screw197  label="M3x16-Screw089"  # Fasteners workbench fastener (typed FeaturePython)
  Placement = pos=(315.39,148.94,52.9) rot=(0,0,1;1.5708rad)
  Visibility1 = true
  diameter = 4
  invert = false
  leftHanded = false
  length = 6
  lengthCustom = 16
  matchOuter = false
  offset = 0
  thread = false
  type = 33
FEATURE [Part::FeaturePython] Screw198  label="M3x16-Screw090"  # Fasteners workbench fastener (typed FeaturePython)
  Placement = pos=(285.39,148.94,52.9) rot=(0,0,1;1.5708rad)
  Visibility1 = true
  diameter = 4
  invert = false
  leftHanded = false
  length = 6
  lengthCustom = 16
  matchOuter = false
  offset = 0
  thread = false
  type = 33
FEATURE [Part::FeaturePython] Nut089  label="M3-Nut476"  # Fasteners workbench fastener (typed FeaturePython)
  Placement = pos=(270.41,133.951,37.57) rot=(0,0,-1;1.5708rad)
  diameter = 4
  invert = false
  leftHanded = false
  matchOuter = false
  offset = -2
  thread = false
  type = 7
FEATURE [Part::FeaturePython] Nut090  label="M3-Nut477"  # Fasteners workbench fastener (typed FeaturePython)
  Placement = pos=(315.41,148.951,37.57) rot=(0,0,-1;1.5708rad)
  diameter = 4
  invert = false
  leftHanded = false
  matchOuter = false
  offset = -2
  thread = false
  type = 7
FEATURE [Part::FeaturePython] Nut091  label="M3-Nut478"  # Fasteners workbench fastener (typed FeaturePython)
  Placement = pos=(285.41,148.951,37.57) rot=(0,0,-1;1.5708rad)
  diameter = 4
  invert = false
  leftHanded = false
  matchOuter = false
  offset = -2
  thread = false
  type = 7
FEATURE [Part::FeaturePython] Screw199  label="M3x8-Screw525"  # Fasteners workbench fastener (typed FeaturePython)
  Placement = pos=(456.42,171.94,140.5) rot=(1,0,0;1.5708rad)
  Visibility1 = true
  diameter = 1
  invert = false
  leftHanded = false
  length = 1
  lengthCustom = 8
  matchOuter = false
  offset = 0
  thread = false
  type = 39
FEATURE [Part::FeaturePython] Screw200  label="M3x8-Screw526"  # Fasteners workbench fastener (typed FeaturePython)
  Placement = pos=(471.41,171.94,140.5) rot=(1,0,0;1.5708rad)
  Visibility1 = true
  diameter = 1
  invert = false
  leftHanded = false
  length = 1
  lengthCustom = 8
  matchOuter = false
  offset = 0
  thread = false
  type = 39
FEATURE [Part::FeaturePython] Screw201  label="M3x8-Screw533"  # Fasteners workbench fastener (typed FeaturePython)
  Placement = pos=(431.25,171.94,140.83) rot=(1,0,0;1.5708rad)
  Visibility1 = true
  diameter = 1
  invert = false
  leftHanded = false
  length = 1
  lengthCustom = 8
  matchOuter = false
  offset = 0
  thread = false
  type = 39
FEATURE [Part::FeaturePython] Screw202  label="M3x8-Screw534"  # Fasteners workbench fastener (typed FeaturePython)
  Placement = pos=(416.15,171.94,140.83) rot=(1,0,0;1.5708rad)
  Visibility1 = true
  diameter = 1
  invert = false
  leftHanded = false
  length = 1
  lengthCustom = 8
  matchOuter = false
  offset = 0
  thread = false
  type = 39
FEATURE [Part::FeaturePython] Screw203  label="M3x8-Screw481"  # Fasteners workbench fastener (typed FeaturePython)
  Placement = pos=(347.7,142.59,29.84) rot=(-1,0,0;1.5708rad)
  Visibility1 = true
  diameter = 1
  invert = false
  leftHanded = false
  length = 1
  lengthCustom = 8
  matchOuter = false
  offset = 0
  thread = false
  type = 39
FEATURE [Part::FeaturePython] Screw204  label="M3x8-Screw482"  # Fasteners workbench fastener (typed FeaturePython)
  Placement = pos=(362.4,142.79,19.44) rot=(-1,0,0;1.5708rad)
  Visibility1 = true
  diameter = 1
  invert = false
  leftHanded = false
  length = 1
  lengthCustom = 8
  matchOuter = false
  offset = 0
  thread = false
  type = 39
FEATURE [Part::FeaturePython] Screw205  label="M3x8-Screw475"  # Fasteners workbench fastener (typed FeaturePython)
  Placement = pos=(375.7,148.49,43.04) rot=(0,0,1;3.14159rad)
  Visibility1 = true
  diameter = 1
  invert = false
  leftHanded = false
  length = 1
  lengthCustom = 8
  matchOuter = false
  offset = 0
  thread = false
  type = 39
FEATURE [Part::FeaturePython] Nut092  label="M3-Nut479"  # Fasteners workbench fastener (typed FeaturePython)
  Placement = pos=(375.61,148.551,35.97) rot=(0,0,-1;1.5708rad)
  diameter = 4
  invert = false
  leftHanded = false
  matchOuter = false
  offset = -2
  thread = false
  type = 7
FEATURE [Part::FeaturePython] Screw207  label="M3x10-Screw112"  # Fasteners workbench fastener (typed FeaturePython)
  Placement = pos=(180.31,74.04,43.1) rot=(0,0,-1;1.5708rad)
  Visibility1 = true
  diameter = 1
  invert = false
  leftHanded = false
  length = 2
  lengthCustom = 10
  matchOuter = false
  offset = 0
  thread = false
  type = 39
FEATURE [Part::FeaturePython] Screw208  label="M3x8-Screw477"  # Fasteners workbench fastener (typed FeaturePython)
  Placement = pos=(345.6,148.49,43.04) rot=(0,0,1;3.14159rad)
  Visibility1 = true
  diameter = 1
  invert = false
  leftHanded = false
  length = 1
  lengthCustom = 8
  matchOuter = false
  offset = 0
  thread = false
  type = 39
FEATURE [Part::FeaturePython] Nut094  label="M3-Nut481"  # Fasteners workbench fastener (typed FeaturePython)
  Placement = pos=(345.51,148.351,35.97) rot=(0,0,-1;1.5708rad)
  diameter = 4
  invert = false
  leftHanded = false
  matchOuter = false
  offset = -2
  thread = false
  type = 7
FEATURE [Part::FeaturePython] Nut096  label="M3-Nut536"  # Fasteners workbench fastener (typed FeaturePython)
  Placement = pos=(180.317,74.0312,39.07) rot=(0.965926,-0.258819,0;3.14159rad)
  Visibility1 = true
  diameter = 4
  invert = false
  leftHanded = false
  matchOuter = false
  offset = 0
  thread = false
  type = 7
FEATURE [Part::FeaturePython] b_FDM_0023_peek_cable_guide_001_  label="peek-cable-clamp"  # a2plus imported part (geometry in sourceFile) (typed FeaturePython)
  Placement = pos=(555.348,58.8938,36.6196) rot=(0.57735,-0.57735,0.57735;4.18879rad)
  a2p_Version = V0.1
  fixedPosition = false
  objectType = a2pPart
  sourceFile = ./FDM/peek-cable-clamp.FCStd
  subassemblyImport = false
  timeLastImport = 1.66336e+09
  updateColors = true
FEATURE [Part::FeaturePython] b_FDM_0023_peek_cable_guide_001_001  label="peek-cable-clamp001"  # a2plus imported part (geometry in sourceFile) (typed FeaturePython)
  Placement = pos=(435.248,58.8938,36.6196) rot=(0.57735,-0.57735,0.57735;4.18879rad)
  a2p_Version = V0.1
  fixedPosition = false
  objectType = a2pPart
  sourceFile = ./FDM/peek-cable-clamp.FCStd
  subassemblyImport = false
  timeLastImport = 1.66336e+09
  updateColors = true
FEATURE [Part::FeaturePython] b_FDM_0023_peek_cable_guide_001_002  label="peek-cable-clamp002"  # a2plus imported part (geometry in sourceFile) (typed FeaturePython)
  Placement = pos=(255.048,58.8938,36.6196) rot=(0.57735,-0.57735,0.57735;4.18879rad)
  a2p_Version = V0.1
  fixedPosition = false
  objectType = a2pPart
  sourceFile = ./FDM/peek-cable-clamp.FCStd
  subassemblyImport = false
  timeLastImport = 1.66336e+09
  updateColors = true
FEATURE [Part::FeaturePython] b_FDM_0023_peek_cable_guide_001_003  label="peek-cable-clamp003"  # a2plus imported part (geometry in sourceFile) (typed FeaturePython)
  Placement = pos=(405.948,148.894,36.6196) rot=(0.57735,0.57735,-0.57735;4.18879rad)
  a2p_Version = V0.1
  fixedPosition = false
  objectType = a2pPart
  sourceFile = ./FDM/peek-cable-clamp.FCStd
  subassemblyImport = false
  timeLastImport = 1.66336e+09
  updateColors = true
FEATURE [Part::FeaturePython] b_FDM_0023_peek_cable_guide_001_004  label="peek-cable-clamp004"  # a2plus imported part (geometry in sourceFile) (typed FeaturePython)
  Placement = pos=(195.448,148.894,36.6196) rot=(0.57735,0.57735,-0.57735;4.18879rad)
  a2p_Version = V0.1
  fixedPosition = false
  objectType = a2pPart
  sourceFile = ./FDM/peek-cable-clamp.FCStd
  subassemblyImport = false
  timeLastImport = 1.66336e+09
  updateColors = true
FEATURE [Part::FeaturePython] b_FDM_0023_peek_cable_guide_001_005  label="peek-cable-clamp005"  # a2plus imported part (geometry in sourceFile) (typed FeaturePython)
  Placement = pos=(435.348,118.894,36.6196) rot=(0.57735,0.57735,-0.57735;4.18879rad)
  a2p_Version = V0.1
  fixedPosition = false
  objectType = a2pPart
  sourceFile = ./FDM/peek-cable-clamp.FCStd
  subassemblyImport = false
  timeLastImport = 1.66336e+09
  updateColors = true
FEATURE [Part::FeaturePython] Nut101  label="M3-Nut484"  # Fasteners workbench fastener (typed FeaturePython)
  Placement = pos=(195.487,148.651,32.8) rot=(0.707107,-0.707107,0;3.14159rad)
  Visibility1 = true
  diameter = 4
  invert = false
  leftHanded = false
  matchOuter = false
  offset = 0
  thread = false
  type = 7
FEATURE [Part::FeaturePython] Screw210  label="M3x14-Screw159"  # Fasteners workbench fastener (typed FeaturePython)
  Placement = pos=(195.39,148.94,42.8) rot=(0,0,1;1.5708rad)
  Visibility1 = true
  diameter = 1
  invert = false
  leftHanded = false
  length = 4
  lengthCustom = 14
  matchOuter = false
  offset = 0
  thread = false
  type = 39
FEATURE [Part::FeaturePython] Screw211  label="M3x14-Screw160"  # Fasteners workbench fastener (typed FeaturePython)
  Placement = pos=(406.19,148.94,42.8) rot=(0,0,1;1.5708rad)
  Visibility1 = true
  diameter = 1
  invert = false
  leftHanded = false
  length = 4
  lengthCustom = 14
  matchOuter = false
  offset = 0
  thread = false
  type = 39
FEATURE [Part::FeaturePython] Screw212  label="M3x14-Screw161"  # Fasteners workbench fastener (typed FeaturePython)
  Placement = pos=(255.39,58.64,42.8) rot=(0,0,1;1.5708rad)
  Visibility1 = true
  diameter = 1
  invert = false
  leftHanded = false
  length = 4
  lengthCustom = 14
  matchOuter = false
  offset = 0
  thread = false
  type = 39
FEATURE [Part::FeaturePython] Screw213  label="M3x14-Screw162"  # Fasteners workbench fastener (typed FeaturePython)
  Placement = pos=(435.39,118.74,42.8) rot=(0,0,1;1.5708rad)
  Visibility1 = true
  diameter = 1
  invert = false
  leftHanded = false
  length = 4
  lengthCustom = 14
  matchOuter = false
  offset = 0
  thread = false
  type = 39
FEATURE [Part::FeaturePython] Screw214  label="M3x14-Screw163"  # Fasteners workbench fastener (typed FeaturePython)
  Placement = pos=(555.39,58.84,42.8) rot=(0,0,1;1.5708rad)
  Visibility1 = true
  diameter = 1
  invert = false
  leftHanded = false
  length = 4
  lengthCustom = 14
  matchOuter = false
  offset = 0
  thread = false
  type = 39
FEATURE [Part::FeaturePython] Screw215  label="M3x14-Screw164"  # Fasteners workbench fastener (typed FeaturePython)
  Placement = pos=(435.19,58.84,42.8) rot=(0,0,1;1.5708rad)
  Visibility1 = true
  diameter = 1
  invert = false
  leftHanded = false
  length = 4
  lengthCustom = 14
  matchOuter = false
  offset = 0
  thread = false
  type = 39
FEATURE [Part::FeaturePython] Nut102  label="M3-Nut485"  # Fasteners workbench fastener (typed FeaturePython)
  Placement = pos=(406.087,148.651,32.8) rot=(0.707107,-0.707107,0;3.14159rad)
  Visibility1 = true
  diameter = 4
  invert = false
  leftHanded = false
  matchOuter = false
  offset = 0
  thread = false
  type = 7
FEATURE [Part::FeaturePython] Nut103  label="M3-Nut489"  # Fasteners workbench fastener (typed FeaturePython)
  Placement = pos=(255.347,58.65,32.8) rot=(0.707107,-0.707107,0;3.14159rad)
  Visibility1 = true
  diameter = 4
  invert = false
  leftHanded = false
  matchOuter = false
  offset = 0
  thread = false
  type = 7
FEATURE [Part::FeaturePython] Nut104  label="M3-Nut486"  # Fasteners workbench fastener (typed FeaturePython)
  Placement = pos=(435.487,118.851,32.8) rot=(0.707107,-0.707107,0;3.14159rad)
  Visibility1 = true
  diameter = 4
  invert = false
  leftHanded = false
  matchOuter = false
  offset = 0
  thread = false
  type = 7
FEATURE [Part::FeaturePython] Nut105  label="M3-Nut488"  # Fasteners workbench fastener (typed FeaturePython)
  Placement = pos=(435.187,58.8512,32.8) rot=(0.707107,-0.707107,0;3.14159rad)
  Visibility1 = true
  diameter = 4
  invert = false
  leftHanded = false
  matchOuter = false
  offset = 0
  thread = false
  type = 7
FEATURE [Part::FeaturePython] Nut106  label="M3-Nut487"  # Fasteners workbench fastener (typed FeaturePython)
  Placement = pos=(555.387,58.8512,31.45) rot=(0.707107,-0.707107,0;3.14159rad)
  Visibility1 = true
  diameter = 4
  invert = false
  leftHanded = false
  matchOuter = false
  offset = 0
  thread = false
  type = 7
FEATURE [Part::FeaturePython] b_PCB_0002_00_Datum_OpenPNPcalibration1_001_  label="datum-board"  # a2plus imported part (geometry in sourceFile) (typed FeaturePython)
  Placement = pos=(260.466,124.331,51.3924) rot=(0,0,1;0rad)
  a2p_Version = V0.1
  fixedPosition = false
  objectType = a2pPart
  sourceFile = ./PCB/datum-board.step
  subassemblyImport = false
  timeLastImport = 1.65531e+09
  updateColors = true
FEATURE [Part::FeaturePython] b_PCB_0003_00_RingLight1_001_  label="bottom-ring-light"  # a2plus imported part (geometry in sourceFile) (typed FeaturePython)
  Placement = pos=(300.339,104.466,32.5) rot=(0,0,1;0.802851rad)
  a2p_Version = V0.1
  fixedPosition = false
  objectType = a2pPart
  sourceFile = ./PCB/bottom-ring-light.FCStd
  subassemblyImport = false
  timeLastImport = 1.66336e+09
  updateColors = true
FEATURE [Part::FeaturePython] b_PCB_0003_00_RingLight1_001_001  label="top-ring-light"  # a2plus imported part (geometry in sourceFile) (typed FeaturePython)
  Placement = pos=(444.287,221.73,90.9615) rot=(0,1,0;3.14159rad)
  a2p_Version = V0.1
  fixedPosition = false
  objectType = a2pPart
  sourceFile = ./PCB/top-ring-light.FCStd
  subassemblyImport = false
  timeLastImport = 1.66336e+09
  updateColors = true
FEATURE [App::DocumentObjectGroup] Group012  label="CameraAndLight"
  Group = -> [b_FDM_0014_down_camera_mount_001_,b_FDM_0015_down_light_mount_001_,Screw171,Screw185,Screw186,Screw187,Screw188,Screw189,b_OTS_0002_00_usb_webcam_001_,b_PCB_0003_00_RingLight1_001_001]
FEATURE [Part::FeaturePython] Screw216  label="M2.5x8-Screw194"  # Fasteners workbench fastener (typed FeaturePython)
  Placement = pos=(408.6,144.4,120.66) rot=(0.707107,-0.707107,0;3.14159rad)
  diameter = 3
  invert = false
  leftHanded = false
  length = 3
  lengthCustom = 8
  matchOuter = false
  offset = 0
  thread = false
  type = 34
FEATURE [Part::FeaturePython] Screw217  label="M2.5x8-Screw195"  # Fasteners workbench fastener (typed FeaturePython)
  Placement = pos=(431.5,144.4,120.66) rot=(0.707107,-0.707107,0;3.14159rad)
  diameter = 3
  invert = false
  leftHanded = false
  length = 3
  lengthCustom = 8
  matchOuter = false
  offset = 0
  thread = false
  type = 34
FEATURE [Part::FeaturePython] Screw218  label="M2.5x8-Screw"  # Fasteners workbench fastener (typed FeaturePython)
  Placement = pos=(408.5,167.3,120.66) rot=(0.707107,-0.707107,0;3.14159rad)
  diameter = 3
  invert = false
  leftHanded = false
  length = 3
  lengthCustom = 8
  matchOuter = false
  offset = 0
  thread = false
  type = 34
FEATURE [Part::FeaturePython] Screw219  label="M2.5x8-Screw196"  # Fasteners workbench fastener (typed FeaturePython)
  Placement = pos=(431.5,167.3,120.66) rot=(0.707107,-0.707107,0;3.14159rad)
  diameter = 3
  invert = false
  leftHanded = false
  length = 3
  lengthCustom = 8
  matchOuter = false
  offset = 0
  thread = false
  type = 34
FEATURE [Part::FeaturePython] b_FST_0017_M3_cap_nut1_001_  label="M3-cap-nut"  # a2plus imported part (geometry in sourceFile) (typed FeaturePython)
  Placement = pos=(575.135,-89.5237,100.422) rot=(1,0,0;1.5708rad)
  a2p_Version = V0.1
  fixedPosition = false
  objectType = a2pPart
  sourceFile = ./FST/M3-cap-nut.STEP
  subassemblyImport = false
  timeLastImport = 1.65531e+09
  updateColors = true
FEATURE [Part::FeaturePython] b_FST_0017_M3_cap_nut1_001_001  label="M3-cap-nut001"  # a2plus imported part (geometry in sourceFile) (typed FeaturePython)
  Placement = pos=(626.288,224.192,144.277) rot=(0.57735,0.57735,0.57735;2.0944rad)
  a2p_Version = V0.1
  fixedPosition = false
  objectType = a2pPart
  sourceFile = ./FST/M3-cap-nut.STEP
  subassemblyImport = false
  timeLastImport = 1.65531e+09
  updateColors = true
FEATURE [Part::FeaturePython] b_FST_0017_M3_cap_nut1_001_002  label="M3-cap-nut002"  # a2plus imported part (geometry in sourceFile) (typed FeaturePython)
  Placement = pos=(25.0268,-89.3507,100.008) rot=(1,0,0;1.5708rad)
  a2p_Version = V0.1
  fixedPosition = false
  objectType = a2pPart
  sourceFile = ./FST/M3-cap-nut.STEP
  subassemblyImport = false
  timeLastImport = 1.65531e+09
  updateColors = true
FEATURE [Part::FeaturePython] b_NEMA11_hollow_shaft_stepper1_001_  label="NEMA11-hollow-shaft-stepper"  # a2plus imported part (geometry in sourceFile) (typed FeaturePython)
  Placement = pos=(420.01,155.83,142.55) rot=(0.707107,-0.707107,0;3.14159rad)
  a2p_Version = V0.1
  fixedPosition = false
  objectType = a2pPart
  sourceFile = ./MISC/NEMA11-hollow-shaft-stepper.step
  subassemblyImport = false
  timeLastImport = 1.66336e+09
  updateColors = true
FEATURE [Part::FeaturePython] b_x_idler_mount_001_  label="x-idler-mount_001"  # a2plus imported part (geometry in sourceFile) (typed FeaturePython)
  Placement = pos=(622.24,209.11,124.04) rot=(0.57735,-0.57735,-0.57735;2.0944rad)
  a2p_Version = V0.1
  fixedPosition = false
  objectType = a2pPart
  sourceFile = ./FDM/x-idler-mount.FCStd
  subassemblyImport = false
  timeLastImport = 1.66336e+09
  updateColors = true
FEATURE [Part::FeaturePython] b_x_motor_mount_001_  label="x-motor-mount"  # a2plus imported part (geometry in sourceFile) (typed FeaturePython)
  Placement = pos=(-21.975,209.125,134.768) rot=(0.57735,0.57735,0.57735;2.0944rad)
  a2p_Version = V0.1
  fixedPosition = false
  objectType = a2pPart
  sourceFile = ./FDM/x-motor-mount.FCStd
  subassemblyImport = false
  timeLastImport = 1.66336e+09
  updateColors = true
FEATURE [Part::FeaturePython] b_M5_tslot_nut1_001_034  label="M5-tslot-nut034"  # a2plus imported part (geometry in sourceFile) (typed FeaturePython)
  Placement = pos=(594.328,209.112,148.905) rot=(0,0,1;0rad)
  Visibility1 = true
  a2p_Version = V0.1
  fixedPosition = false
  objectType = a2pPart
  sourceFile = ./FST/M5-tslot-nut.step
  sourcePart = M5-tslot-nut
  subassemblyImport = false
  timeLastImport = 1.66336e+09
  updateColors = true
FEATURE [Part::FeaturePython] Screw220  label="M5x10-Screw350"  # Fasteners workbench fastener (typed FeaturePython)
  Placement = pos=(594.27,209.12,158.94) rot=(0,0,-1;1.5708rad)
  Visibility1 = true
  diameter = 6
  invert = false
  leftHanded = false
  length = 1
  lengthCustom = 10
  matchOuter = false
  offset = 0
  thread = false
  type = 33
FEATURE [Part::FeaturePython] b_M5_tslot_nut1_001_035  label="M5-tslot-nut035"  # a2plus imported part (geometry in sourceFile) (typed FeaturePython)
  Placement = pos=(6.12821,209.212,148.905) rot=(0,0,1;0rad)
  Visibility1 = true
  a2p_Version = V0.1
  fixedPosition = false
  objectType = a2pPart
  sourceFile = ./FST/M5-tslot-nut.step
  sourcePart = M5-tslot-nut
  subassemblyImport = false
  timeLastImport = 1.66336e+09
  updateColors = true
FEATURE [Part::FeaturePython] Screw221  label="M5x10-Screw487"  # Fasteners workbench fastener (typed FeaturePython)
  Placement = pos=(6.025,209.125,159.768) rot=(0,0,-1;1.5708rad)
  Visibility1 = true
  diameter = 6
  invert = false
  leftHanded = false
  length = 1
  lengthCustom = 10
  matchOuter = false
  offset = 0
  thread = false
  type = 33
FEATURE [Part::FeaturePython] Nut107  label="M5-Nut924"  # Fasteners workbench fastener (typed FeaturePython)
  Placement = pos=(473.049,216.7,195.65) rot=(0.654654,0.377965,0.654654;2.41886rad)
  Visibility1 = true
  diameter = 7
  invert = false
  leftHanded = false
  matchOuter = false
  offset = 0
  thread = false
  type = 7
FEATURE [Part::FeaturePython] Nut108  label="M5-Nut923"  # Fasteners workbench fastener (typed FeaturePython)
  Placement = pos=(473.049,216.7,210.65) rot=(0.654654,0.377965,0.654654;2.41886rad)
  Visibility1 = true
  diameter = 7
  invert = false
  leftHanded = false
  matchOuter = false
  offset = 0
  thread = false
  type = 7
FEATURE [Part::FeaturePython] Screw222  label="M5x16-Screw179"  # Fasteners workbench fastener (typed FeaturePython)
  Placement = pos=(488.775,216.7,210.65) rot=(0.654654,0.377964,0.654654;2.41886rad)
  Visibility1 = true
  diameter = 6
  invert = false
  leftHanded = false
  length = 12
  lengthCustom = 16
  matchOuter = false
  offset = 0
  thread = false
  type = 33
FEATURE [Part::FeaturePython] Screw223  label="M5x16-Screw178"  # Fasteners workbench fastener (typed FeaturePython)
  Placement = pos=(488.775,216.7,195.65) rot=(0.654654,0.377964,0.654654;2.41886rad)
  Visibility1 = true
  diameter = 6
  invert = false
  leftHanded = false
  length = 12
  lengthCustom = 16
  matchOuter = false
  offset = 0
  thread = false
  type = 33
FEATURE [Part::FeaturePython] Nut015  label="M5-Nut675"  # Fasteners workbench fastener (typed FeaturePython)
  Placement = pos=(603.67,209.1,98.11) rot=(0.57735,0.57735,0.57735;2.0944rad)
  Visibility1 = true
  diameter = 7
  invert = false
  leftHanded = false
  matchOuter = false
  offset = 0
  thread = false
  type = 7
FEATURE [Part::FeaturePython] Screw013  label="M5x25-Screw142"  # Fasteners workbench fastener (typed FeaturePython)
  Placement = pos=(625.18,209.1,98.11) rot=(0.57735,0.57735,0.57735;2.0944rad)
  Visibility1 = true
  diameter = 6
  invert = false
  leftHanded = false
  length = 12
  lengthCustom = 25
  matchOuter = false
  offset = 0
  thread = false
  type = 33
FEATURE [Part::FeaturePython] Nut014  label="M5-Nut674"  # Fasteners workbench fastener (typed FeaturePython)
  Placement = pos=(603.67,209.66,121.52) rot=(0.447214,0.774597,0.447214;1.82348rad)
  Visibility1 = true
  diameter = 7
  invert = false
  leftHanded = false
  matchOuter = false
  offset = 0
  thread = false
  type = 7
FEATURE [Part::FeaturePython] Screw012  label="M5x25-Screw143"  # Fasteners workbench fastener (typed FeaturePython)
  Placement = pos=(625.24,209.5,122.25) rot=(0.57735,0.57735,0.57735;2.0944rad)
  Visibility1 = true
  diameter = 6
  invert = false
  leftHanded = false
  length = 12
  lengthCustom = 25
  matchOuter = false
  offset = 0
  thread = false
  type = 33
FEATURE [App::DocumentObjectGroup] X_Motor  label="X-Motor"
  Group = -> [b_Gates_2GT_20T_Toothed_Pulley1_001_001,b_Nema_17_42A02C_v21_001_001,Screw098,Screw099,Screw097,Screw100]
FEATURE [App::DocumentObjectGroup] Y_Gantry_Slider_Right  label="Y-Gantry-Slider-Right"
  Group = -> [Screw057,Nut039,b_FDM_0027_belt_clamp_001_004,Nut040,Nut041,Nut038,Screw055,Screw056,b_FDM_0027_belt_clamp_001_005,Screw058,Nut014,Nut015]
FEATURE [App::DocumentObjectGroup] Front_Feeder_Rail  label="Front-Feeder-Rail"
  Group = -> [b_M5_tslot_nut1_001_018,b_OTS_0009_20x20_v_slot_600mm1_001_,Screw075,b_M5_tslot_nut1_001_016,Screw074,Screw073,b_2020CornerBracket1_001_001,b_2020CornerBracket1_001_,Screw076,b_M5_tslot_nut1_001_017,b_M5_tslot_nut1_001_019,b_M5_tslot_nut1_001_012,b_M5_tslot_nut1_001_011,Screw037,Screw072]
FEATURE [App::DocumentObjectGroup] Rear_Feeder_Rail  label="Rear-Feeder-Rail"
  Group = -> [Screw080,Screw084,b_M5_tslot_nut1_001_025,Screw078,b_2020CornerBracket1_001_005,b_2020CornerBracket1_001_003,b_2020CornerBracket1_001_002,b_M5_tslot_nut1_001_022,b_M5_tslot_nut1_001_020,Screw079,Screw083,Screw082,b_M5_tslot_nut1_001_023,b_M5_tslot_nut1_001_026,b_M5_tslot_nut1_001_024,b_2020CornerBracket1_001_004,Screw077,Screw081,b_M5_tslot_nut1_001_027,b_M5_tslot_nut1_001_021,+1 more]
FEATURE [App::DocumentObjectGroup] Group  label="Feeder-Rails"
  Group = -> [Rear_Feeder_Rail,Front_Feeder_Rail]
FEATURE [App::DocumentObjectGroup] Extrusion  label="Y-Left-Extrusion"
  Group = -> [b_OTS_0009_20x20_v_slot_600mm1_001_002,b_OTS_0009_20x20_v_slot_600mm1_001_001]
FEATURE [App::DocumentObjectGroup] Extrusion001  label="Y-Right-Extrusion"
  Group = -> [b_OTS_0009_20x20_v_slot_600mm1_001_004,b_OTS_0009_20x20_v_slot_600mm1_001_005]
FEATURE [Part::FeaturePython] b_belt_tension_arm_001_  label="x-belt-tension-arm"  # a2plus imported part (geometry in sourceFile) (typed FeaturePython)
  Placement = pos=(627.16,189.23,134.07) rot=(0.57735,0.57735,0.57735;2.0944rad)
  a2p_Version = V0.1
  fixedPosition = false
  objectType = a2pPart
  sourceFile = ./FDM/belt-tension-arm.FCStd
  subassemblyImport = false
  timeLastImport = 1.66336e+09
  updateColors = true
FEATURE [Part::FeaturePython] b_belt_tension_arm_001_001  label="y2-belt-tension-arm"  # a2plus imported part (geometry in sourceFile) (typed FeaturePython)
  Placement = pos=(610.04,-90.5,110.07) rot=(0,0.707107,-0.707107;3.14159rad)
  a2p_Version = V0.1
  fixedPosition = false
  objectType = a2pPart
  sourceFile = ./FDM/belt-tension-arm.FCStd
  subassemblyImport = false
  timeLastImport = 1.66336e+09
  updateColors = true
FEATURE [Part::FeaturePython] b_belt_tension_arm_001_002  label="y1-belt-tension-arm"  # a2plus imported part (geometry in sourceFile) (typed FeaturePython)
  Placement = pos=(-10.04,-90.59,89.98) rot=(1,0,0;1.5708rad)
  a2p_Version = V0.1
  fixedPosition = false
  objectType = a2pPart
  sourceFile = ./FDM/belt-tension-arm.FCStd
  subassemblyImport = false
  timeLastImport = 1.66336e+09
  updateColors = true
FEATURE [Part::FeaturePython] Screw228  label="M5x10-Screw364"  # Fasteners workbench fastener (typed FeaturePython)
  Placement = pos=(-6.72,-85.5,195.3) rot=(0.654654,0.377964,0.654654;2.41886rad)
  Visibility1 = true
  diameter = 6
  invert = false
  leftHanded = false
  length = 12
  lengthCustom = 10
  matchOuter = false
  offset = 0
  thread = false
  type = 33
FEATURE [Part::FeaturePython] Nut111  label="M5-Nut660"  # Fasteners workbench fastener (typed FeaturePython)
  Placement = pos=(-17.52,-86.865,210.3) rot=(0.654654,0.377964,0.654654;2.41886rad)
  Visibility1 = true
  diameter = 7
  invert = false
  leftHanded = false
  matchOuter = false
  offset = 0
  thread = false
  type = 7
FEATURE [Part::FeaturePython] Screw229  label="M5x10-Screw365"  # Fasteners workbench fastener (typed FeaturePython)
  Placement = pos=(-6.72,-86.865,210.3) rot=(0.654654,0.377964,0.654654;2.41886rad)
  Visibility1 = true
  diameter = 6
  invert = false
  leftHanded = false
  length = 12
  lengthCustom = 10
  matchOuter = false
  offset = 0
  thread = false
  type = 33
FEATURE [Part::FeaturePython] Nut112  label="M5-Nut661"  # Fasteners workbench fastener (typed FeaturePython)
  Placement = pos=(-17.52,-85.5,195.3) rot=(0.654654,0.377964,0.654654;2.41886rad)
  Visibility1 = true
  diameter = 7
  invert = false
  leftHanded = false
  matchOuter = false
  offset = 0
  thread = false
  type = 7
FEATURE [App::DocumentObjectGroup] Drag_Chain_Bolts  label="Drag_Chain_to_Drag_Chain_Mount_Attachment_Hardware"
  Group = -> [Screw228,Nut111,Screw229,Nut112]
FEATURE [Part::FeaturePython] b_NEMA11_hollow_shaft_stepper1_001_001  label="NEMA11-hollow-shaft-stepper001"  # a2plus imported part (geometry in sourceFile) (typed FeaturePython)
  Placement = pos=(467.62,155.88,142.54) rot=(0.707107,-0.707107,0;3.14159rad)
  a2p_Version = V0.1
  fixedPosition = false
  objectType = a2pPart
  sourceFile = ./MISC/NEMA11-hollow-shaft-stepper.step
  subassemblyImport = false
  timeLastImport = 1.66336e+09
  updateColors = true
FEATURE [Part::FeaturePython] b_OTS_0001_00_CP40_nozzle_holder_001_001  label="CP40-holder001"  # a2plus imported part (geometry in sourceFile) (typed FeaturePython)
  Placement = pos=(467.658,155.84,87.7745) rot=(0.57735,-0.57735,-0.57735;2.0944rad)
  Visibility1 = true
  a2p_Version = V0.1
  fixedPosition = false
  objectType = a2pPart
  sourceFile = ./MISC/cp40-holder.FCStd
  sourcePart = Body
  subassemblyImport = false
  timeLastImport = 1.65531e+09
  updateColors = true
FEATURE [Part::FeaturePython] b_MS4M_M51_001_001  label="pneumatic-adapter-MS4M-M006"  # a2plus imported part (geometry in sourceFile) (typed FeaturePython)
  Placement = pos=(467.662,155.88,162.502) rot=(0.57735,-0.57735,-0.57735;2.0944rad)
  Visibility1 = true
  a2p_Version = V0.1
  fixedPosition = false
  objectType = a2pPart
  sourceFile = ./MISC/pneumatic-adapter-MS4M-M5.STEP
  sourcePart = MS4M-M5
  subassemblyImport = false
  timeLastImport = 1.65531e+09
  updateColors = true
FEATURE [Part::FeaturePython] b_OTS_0009_pneumatic_splitter_URY6M_4M1_001_001  label="pneumatic-y-adapter001"  # a2plus imported part (geometry in sourceFile) (typed FeaturePython)
  Placement = pos=(202.73,95.5937,24.3499) rot=(0.57735,-0.57735,0.57735;2.0944rad)
  a2p_Version = V0.1
  fixedPosition = false
  objectType = a2pPart
  sourceFile = ./MISC/pneumatic-y-adapter.STEP
  subassemblyImport = false
  timeLastImport = 1.65531e+09
  updateColors = true
FEATURE [Part::FeaturePython] Nut113  label="M3-Nut537"  # Fasteners workbench fastener (typed FeaturePython)
  Placement = pos=(180.317,104.031,38.57) rot=(0.965926,0.258819,0;3.14159rad)
  Visibility1 = true
  diameter = 4
  invert = false
  leftHanded = false
  matchOuter = false
  offset = 0
  thread = false
  type = 7
FEATURE [Part::FeaturePython] Screw232  label="M3x30-Screw166"  # Fasteners workbench fastener (typed FeaturePython)
  Placement = pos=(180.56,102.04,24.35) rot=(0.57735,0.57735,0.57735;4.18879rad)
  Visibility1 = true
  diameter = 4
  invert = false
  leftHanded = false
  length = 9
  lengthCustom = 30
  matchOuter = false
  offset = 0
  thread = false
  type = 33
FEATURE [Part::FeaturePython] b_OTS_0003_00_vacuum_pump_001_002  label="vacuum-pump001"  # a2plus imported part (geometry in sourceFile) (typed FeaturePython)
  Placement = pos=(481.281,73.9358,10.2256) rot=(-0.707107,0,0.707107;3.14159rad)
  Visibility1 = true
  a2p_Version = V0.1
  fixedPosition = false
  objectType = a2pPart
  sourceFile = ./MISC/vacuum-pump.FCStd
  sourcePart = Body
  subassemblyImport = false
  timeLastImport = 1.65531e+09
  updateColors = true
FEATURE [Part::FeaturePython] b_FDM_0025_pump_mount_001_002  label="pump-mount001"  # a2plus imported part (geometry in sourceFile) (typed FeaturePython)
  Placement = pos=(452.615,103.524,-15.2591) rot=(0,0,-1;1.5708rad)
  Visibility1 = true
  a2p_Version = V0.1
  fixedPosition = false
  objectType = a2pPart
  sourceFile = ./FDM/pump-mount.FCStd
  sourcePart = Body
  subassemblyImport = false
  timeLastImport = 1.66336e+09
  updateColors = true
FEATURE [Part::FeaturePython] Screw233  label="M3x10-Screw101"  # Fasteners workbench fastener (typed FeaturePython)
  Placement = pos=(495.4,88.95,42.98) rot=(0,0,1;0rad)
  Visibility1 = true
  diameter = 1
  invert = false
  leftHanded = false
  length = 2
  lengthCustom = 10
  matchOuter = false
  offset = 0
  thread = false
  type = 39
FEATURE [Part::FeaturePython] Nut114  label="M3-Nut491"  # Fasteners workbench fastener (typed FeaturePython)
  Placement = pos=(495.5,88.95,35.75) rot=(1,0,0;3.14159rad)
  Visibility1 = true
  diameter = 4
  invert = false
  leftHanded = false
  matchOuter = false
  offset = 0
  thread = false
  type = 7
FEATURE [Part::FeaturePython] Screw234  label="M3x10-Screw102"  # Fasteners workbench fastener (typed FeaturePython)
  Placement = pos=(465.5,88.95,42.98) rot=(0,0,1;0rad)
  Visibility1 = true
  diameter = 1
  invert = false
  leftHanded = false
  length = 2
  lengthCustom = 10
  matchOuter = false
  offset = 0
  thread = false
  type = 39
FEATURE [Part::FeaturePython] Nut115  label="M3-Nut492"  # Fasteners workbench fastener (typed FeaturePython)
  Placement = pos=(465.6,88.95,35.75) rot=(1,0,0;3.14159rad)
  Visibility1 = true
  diameter = 4
  invert = false
  leftHanded = false
  matchOuter = false
  offset = 0
  thread = false
  type = 7
FEATURE [App::DocumentObjectGroup] _nd_Toolhead_Stuff  label="Right-Toolhead-Pnumatics-System"
  Group = -> [b_OTS_0009_pneumatic_splitter_URY6M_4M1_001_001,Nut113,Screw232,b_OTS_0003_00_vacuum_pump_001_002,b_FDM_0025_pump_mount_001_002,Screw233,Nut114,Screw234,Nut115]
FEATURE [Part::FeaturePython] b_staging_plate1_001_  label="staging-plate1"  # a2plus imported part (geometry in sourceFile) (typed FeaturePython)
  Placement = pos=(161.45,128,42.9729) rot=(1,0,0;3.14159rad)
  a2p_Version = V0.1
  fixedPosition = false
  objectType = a2pPart
  sourceFile = ./pcb/staging-plate/staging-plate.STEP
  subassemblyImport = false
  timeLastImport = 1.65775e+09
  updateColors = true
FEATURE [Part::FeaturePython] Screw235  label="M5x8-Screw192"  # Fasteners workbench fastener (typed FeaturePython)
  Placement = pos=(10.14,273.93,43.19) rot=(0,0,1;3.14159rad)
  Visibility1 = true
  diameter = 3
  invert = false
  leftHanded = false
  length = 0
  lengthCustom = 8
  matchOuter = false
  offset = 0
  thread = false
  type = 39
FEATURE [Part::FeaturePython] Screw236  label="M5x8-Screw193"  # Fasteners workbench fastener (typed FeaturePython)
  Placement = pos=(10.02,174.33,43.32) rot=(0,0,1;3.14159rad)
  Visibility1 = true
  diameter = 3
  invert = false
  leftHanded = false
  length = 0
  lengthCustom = 8
  matchOuter = false
  offset = 0
  thread = false
  type = 39
FEATURE [Part::FeaturePython] Screw237  label="M5x8-Screw194"  # Fasteners workbench fastener (typed FeaturePython)
  Placement = pos=(590.11,174.35,43.19) rot=(0,0,1;3.14159rad)
  Visibility1 = true
  diameter = 3
  invert = false
  leftHanded = false
  length = 0
  lengthCustom = 8
  matchOuter = false
  offset = 0
  thread = false
  type = 39
FEATURE [Part::FeaturePython] Screw238  label="M5x8-Screw195"  # Fasteners workbench fastener (typed FeaturePython)
  Placement = pos=(590.11,273.93,43.19) rot=(0,0,1;3.14159rad)
  Visibility1 = true
  diameter = 3
  invert = false
  leftHanded = false
  length = 0
  lengthCustom = 8
  matchOuter = false
  offset = 0
  thread = false
  type = 39
FEATURE [Part::FeaturePython] b_M5_tslot_nut1_001_036  label="M5-tslot-nut036"  # a2plus imported part (geometry in sourceFile) (typed FeaturePython)
  Placement = pos=(589.718,273.872,34.9746) rot=(0,0,1;1.5708rad)
  Visibility1 = true
  a2p_Version = V0.1
  fixedPosition = false
  objectType = a2pPart
  sourceFile = ./FST/M5-tslot-nut.step
  sourcePart = M5-tslot-nut
  subassemblyImport = false
  timeLastImport = 1.66336e+09
  updateColors = true
FEATURE [Part::FeaturePython] b_M5_tslot_nut1_001_037  label="M5-tslot-nut037"  # a2plus imported part (geometry in sourceFile) (typed FeaturePython)
  Placement = pos=(589.718,174.222,34.9746) rot=(0,0,1;1.5708rad)
  Visibility1 = true
  a2p_Version = V0.1
  fixedPosition = false
  objectType = a2pPart
  sourceFile = ./FST/M5-tslot-nut.step
  sourcePart = M5-tslot-nut
  subassemblyImport = false
  timeLastImport = 1.66336e+09
  updateColors = true
FEATURE [Part::FeaturePython] b_M5_tslot_nut1_001_038  label="M5-tslot-nut038"  # a2plus imported part (geometry in sourceFile) (typed FeaturePython)
  Placement = pos=(9.85821,273.872,34.9746) rot=(0,0,1;1.5708rad)
  Visibility1 = true
  a2p_Version = V0.1
  fixedPosition = false
  objectType = a2pPart
  sourceFile = ./FST/M5-tslot-nut.step
  sourcePart = M5-tslot-nut
  subassemblyImport = false
  timeLastImport = 1.66336e+09
  updateColors = true
FEATURE [Part::FeaturePython] b_M5_tslot_nut1_001_039  label="M5-tslot-nut039"  # a2plus imported part (geometry in sourceFile) (typed FeaturePython)
  Placement = pos=(9.85821,174.272,34.9746) rot=(0,0,1;1.5708rad)
  Visibility1 = true
  a2p_Version = V0.1
  fixedPosition = false
  objectType = a2pPart
  sourceFile = ./FST/M5-tslot-nut.step
  sourcePart = M5-tslot-nut
  subassemblyImport = false
  timeLastImport = 1.66336e+09
  updateColors = true
FEATURE [Part::FeaturePython] b_OTS_0020_index_motherboard1_001_001  label="motherboard"  # a2plus imported part (geometry in sourceFile) (typed FeaturePython)
  Placement = pos=(-28.7282,-11.8301,10.999) rot=(1,0,0;3.14159rad)
  a2p_Version = V0.1
  fixedPosition = false
  objectType = a2pPart
  sourceFile = ./PCB/motherboard.FCStd
  subassemblyImport = false
  timeLastImport = 1.66336e+09
  updateColors = true
FEATURE [Part::FeaturePython] b_FDM_0020_up_camera_mount_001_001  label="bottom-camera-mount"  # a2plus imported part (geometry in sourceFile) (typed FeaturePython)
  Placement = pos=(300.37,104.01,-11.25) rot=(0,0,1;0rad)
  Visibility1 = true
  a2p_Version = V0.1
  fixedPosition = false
  objectType = a2pPart
  sourceFile = ./FDM/bottom-camera-mount.FCStd
  sourcePart = Body
  subassemblyImport = false
  timeLastImport = 1.66336e+09
  updateColors = true
FEATURE [Part::FeaturePython] b_OTS_0002_00_usb_webcam_001_002  label="usb-camera-lower"  # a2plus imported part (geometry in sourceFile) (typed FeaturePython)
  Placement = pos=(300.231,104.1,-7.8) rot=(0,0,1;3.14159rad)
  Visibility1 = true
  a2p_Version = V0.1
  fixedPosition = false
  objectType = a2pPart
  sourceFile = ./MISC/usb-camera.FCStd
  sourcePart = Body
  subassemblyImport = false
  timeLastImport = 1.66336e+09
  updateColors = true
FEATURE [Part::FeaturePython] b_FDM_0019_up_light_mount_001_001  label="bottom-light-mount"  # a2plus imported part (geometry in sourceFile) (typed FeaturePython)
  Placement = pos=(300.398,103.979,32.2367) rot=(0,1,0;3.14159rad)
  Visibility1 = true
  a2p_Version = V0.1
  fixedPosition = false
  objectType = a2pPart
  sourceFile = ./FDM/bottom-light-mount.FCStd
  sourcePart = Body
  subassemblyImport = false
  timeLastImport = 1.66336e+09
  updateColors = true
FEATURE [Part::FeaturePython] b_valve_mount_2_up_001_  label="valve-mount"  # a2plus imported part (geometry in sourceFile) (typed FeaturePython)
  Placement = pos=(341.58,152.52,39.67) rot=(0.57735,-0.57735,0.57735;4.18879rad)
  a2p_Version = V0.1
  fixedPosition = false
  objectType = a2pPart
  sourceFile = ./FDM/valve-mount.FCStd
  subassemblyImport = false
  timeLastImport = 1.66336e+09
  updateColors = true
FEATURE [Part::FeaturePython] b_24v_3_Way_Solenoid_Valve_0526T_www_fspump_cn_001_002  label="solenoid-valve"  # a2plus imported part (geometry in sourceFile) (typed FeaturePython)
  Placement = pos=(366.181,137.41,23.5489) rot=(0,0,1;3.14159rad)
  a2p_Version = V0.1
  fixedPosition = false
  objectType = a2pPart
  sourceFile = ./MISC/solenoid-valve.FCStd
  subassemblyImport = false
  timeLastImport = 1.65531e+09
  updateColors = true
FEATURE [Part::FeaturePython] b_24v_3_Way_Solenoid_Valve_0526T_www_fspump_cn_001_003  label="solenoid-valve001"  # a2plus imported part (geometry in sourceFile) (typed FeaturePython)
  Placement = pos=(366.181,137.41,5.54892) rot=(0,0,1;3.14159rad)
  a2p_Version = V0.1
  fixedPosition = false
  objectType = a2pPart
  sourceFile = ./MISC/solenoid-valve.FCStd
  subassemblyImport = false
  timeLastImport = 1.65531e+09
  updateColors = true
FEATURE [Part::FeaturePython] Screw243  label="M3x8-Screw480"  # Fasteners workbench fastener (typed FeaturePython)
  Placement = pos=(360.4,133.59,43.04) rot=(0,0,1;3.14159rad)
  Visibility1 = true
  diameter = 1
  invert = false
  leftHanded = false
  length = 1
  lengthCustom = 8
  matchOuter = false
  offset = 0
  thread = false
  type = 39
FEATURE [Part::FeaturePython] Nut120  label="M3-Nut501"  # Fasteners workbench fastener (typed FeaturePython)
  Placement = pos=(360.41,133.551,35.97) rot=(0,0,-1;1.5708rad)
  diameter = 4
  invert = false
  leftHanded = false
  matchOuter = false
  offset = -2
  thread = false
  type = 7
FEATURE [Part::FeaturePython] Screw244  label="M3x8-Screw485"  # Fasteners workbench fastener (typed FeaturePython)
  Placement = pos=(347.7,142.59,9.84) rot=(-1,0,0;1.5708rad)
  Visibility1 = true
  diameter = 1
  invert = false
  leftHanded = false
  length = 1
  lengthCustom = 8
  matchOuter = false
  offset = 0
  thread = false
  type = 39
FEATURE [Part::FeaturePython] Screw245  label="M3x8-Screw486"  # Fasteners workbench fastener (typed FeaturePython)
  Placement = pos=(362.4,142.79,-0.56) rot=(-1,0,0;1.5708rad)
  Visibility1 = true
  diameter = 1
  invert = false
  leftHanded = false
  length = 1
  lengthCustom = 8
  matchOuter = false
  offset = 0
  thread = false
  type = 39
FEATURE [App::DocumentObjectGroup] Valves
  Group = -> [Screw245,Nut120,b_24v_3_Way_Solenoid_Valve_0526T_www_fspump_cn_001_003,b_24v_3_Way_Solenoid_Valve_0526T_www_fspump_cn_001_002,Screw243,b_valve_mount_2_up_001_,Nut094,Screw203,Screw204,Screw205,Nut092,Screw208,Screw244]
FEATURE [Part::FeaturePython] b_mobo_bottom_cover_001_  label="mobo-bottom-cover"  # a2plus imported part (geometry in sourceFile) (typed FeaturePython)
  Placement = pos=(40.32,154.2,14.11) rot=(1,0,0;3.14159rad)
  a2p_Version = V0.1
  fixedPosition = false
  objectType = a2pPart
  sourceFile = ./FDM/mobo-bottom-cover.FCStd
  subassemblyImport = false
  timeLastImport = 1.66336e+09
  updateColors = true
FEATURE [Part::FeaturePython] b_foot_2_001_001  label="static-camera-foot"  # a2plus imported part (geometry in sourceFile) (typed FeaturePython)
  a2p_Version = V0.1
  fixedPosition = false
  objectType = a2pPart
  sourceFile = ./FDM/static-camera-foot.FCStd
  subassemblyImport = false
  timeLastImport = 1.66336e+09
  updateColors = true
FEATURE [Part::FeaturePython] b_bottom_camera_cover_001_  label="bottom-camera-cover"  # a2plus imported part (geometry in sourceFile) (typed FeaturePython)
  a2p_Version = V0.1
  fixedPosition = false
  objectType = a2pPart
  sourceFile = ./FDM/bottom-camera-cover.FCStd
  subassemblyImport = false
  timeLastImport = 1.66336e+09
  updateColors = true
FEATURE [Part::FeaturePython] Screw246  label="M2.5x8-Screw188"  # Fasteners workbench fastener (typed FeaturePython)
  Placement = pos=(456.1,144.4,120.45) rot=(0.707107,-0.707107,0;3.14159rad)
  diameter = 3
  invert = false
  leftHanded = false
  length = 3
  lengthCustom = 8
  matchOuter = false
  offset = 0
  thread = false
  type = 34
FEATURE [Part::FeaturePython] Screw247  label="M2.5x8-Screw190"  # Fasteners workbench fastener (typed FeaturePython)
  Placement = pos=(479,144.4,120.45) rot=(0.707107,-0.707107,0;3.14159rad)
  diameter = 3
  invert = false
  leftHanded = false
  length = 3
  lengthCustom = 8
  matchOuter = false
  offset = 0
  thread = false
  type = 34
FEATURE [Part::FeaturePython] Screw248  label="M2.5x8-Screw187"  # Fasteners workbench fastener (typed FeaturePython)
  Placement = pos=(479,167.3,120.45) rot=(0.707107,-0.707107,0;3.14159rad)
  diameter = 3
  invert = false
  leftHanded = false
  length = 3
  lengthCustom = 8
  matchOuter = false
  offset = 0
  thread = false
  type = 34
FEATURE [Part::FeaturePython] Screw249  label="M2.5x8-Screw189"  # Fasteners workbench fastener (typed FeaturePython)
  Placement = pos=(456,167.3,120.45) rot=(0.707107,-0.707107,0;3.14159rad)
  diameter = 3
  invert = false
  leftHanded = false
  length = 3
  lengthCustom = 8
  matchOuter = false
  offset = 0
  thread = false
  type = 34
FEATURE [Part::FeaturePython] b_back_leg_cleaned_001_001  label="back-leg001"  # a2plus imported part (geometry in sourceFile) (typed FeaturePython)
  Placement = pos=(9.91,500.07,-49.89) rot=(0.57735,-0.57735,-0.57735;2.0944rad)
  a2p_Version = V0.1
  fixedPosition = false
  objectType = a2pPart
  sourceFile = ./FDM/back-leg.FCStd
  subassemblyImport = false
  timeLastImport = 1.66336e+09
  updateColors = true
FEATURE [App::DocumentObjectGroup] Group006  label="Back-Left-Leg"
  Group = -> [Screw089,Screw090,Screw091,Screw092,b_Nema_17_42A02C_v21_001_002,b_Gates_2GT_20T_Toothed_Pulley1_001_002,Screw029,Screw030,Screw031,b_M5_tslot_nut1_001_002,b_M5_tslot_nut1_001_003,b_M5_tslot_nut1_001_004,b_back_leg_cleaned_001_001]
FEATURE [Part::FeaturePython] b_front_drag_chain_mount_v3_001_  label="front-drag-chain-mount"  # a2plus imported part (geometry in sourceFile) (typed FeaturePython)
  Placement = pos=(-10.02,-60.05,73.2389) rot=(0.57735,-0.57735,-0.57735;2.0944rad)
  a2p_Version = V0.1
  fixedPosition = false
  objectType = a2pPart
  sourceFile = ./FDM/front-drag-chain-mount.FCStd
  subassemblyImport = false
  timeLastImport = 1.66336e+09
  updateColors = true
FEATURE [Part::FeaturePython] Screw250  label="M5x25-Screw"  # Fasteners workbench fastener (typed FeaturePython)
  Placement = pos=(-18.02,-72.55,79.99) rot=(0.57735,-0.57735,-0.57735;2.0944rad)
  diameter = 6
  invert = false
  leftHanded = false
  length = 12
  lengthCustom = 25
  matchOuter = false
  offset = 0
  thread = false
  type = 34
FEATURE [Part::FeaturePython] Screw251  label="M5x16-Screw"  # Fasteners workbench fastener (typed FeaturePython)
  Placement = pos=(-18.02,-72.55,99.99) rot=(0.57735,-0.57735,-0.57735;2.0944rad)
  diameter = 6
  invert = false
  leftHanded = false
  length = 4
  lengthCustom = 16
  matchOuter = false
  offset = 0
  thread = false
  type = 34
FEATURE [Part::FeaturePython] Nut121  label="M5-Nut664"  # Fasteners workbench fastener (typed FeaturePython)
  Placement = pos=(-2.12,-72.55,99.99) rot=(-0.654654,0.377964,0.654654;3.86433rad)
  Visibility1 = true
  diameter = 7
  invert = false
  leftHanded = false
  matchOuter = false
  offset = 0
  thread = false
  type = 7
FEATURE [Part::FeaturePython] Nut122  label="M5-Nut663"  # Fasteners workbench fastener (typed FeaturePython)
  Placement = pos=(4.98,-72.55,79.99) rot=(-0.654654,0.377964,0.654654;3.86433rad)
  Visibility1 = true
  diameter = 7
  invert = false
  leftHanded = false
  matchOuter = false
  offset = 0
  thread = false
  type = 7
FEATURE [App::DocumentObjectGroup] Group004  label="Front-Left-Leg"
  Group = -> [b_M5_tslot_nut1_001_008,Nut048,Nut045,b_Gates_2GT_20T_Toothed_Idler1_001_001,Nut033,Screw052,Screw053,Screw054,Screw035,Screw036,Screw051,b_M5_tslot_nut1_001_009,b_M5_tslot_nut1_001_010,b_FDM_0001_front_left_leg_001_,b_FST_0017_M3_cap_nut1_001_002,b_belt_tension_arm_001_002,Nut122,Nut121]
FEATURE [Part::FeaturePython] b_x_motor_cable_guide_001_  label="x-motor-cable-guide"  # a2plus imported part (geometry in sourceFile) (typed FeaturePython)
  Placement = pos=(-43.3306,230.625,146.923) rot=(0,0.707107,0.707107;3.14159rad)
  a2p_Version = V0.1
  fixedPosition = false
  objectType = a2pPart
  sourceFile = ./FDM/x-motor-cable-guide.FCStd
  subassemblyImport = false
  timeLastImport = 1.66336e+09
  updateColors = true
FEATURE [Part::FeaturePython] b_front_right_leg_001_  label="front-right-leg"  # a2plus imported part (geometry in sourceFile) (typed FeaturePython)
  Placement = pos=(640,0,20) rot=(0.57735,-0.57735,-0.57735;2.0944rad)
  a2p_Version = V0.1
  fixedPosition = false
  objectType = a2pPart
  sourceFile = ./FDM/front-right-leg.FCStd
  subassemblyImport = false
  timeLastImport = 1.66336e+09
  updateColors = true
FEATURE [App::DocumentObjectGroup] Group005  label="Front-Right-Leg"
  Group = -> [b_M5_tslot_nut1_001_014,b_Gates_2GT_20T_Toothed_Idler1_001_003,Nut046,Screw062,Nut047,Screw063,Nut049,Screw064,Screw070,Screw071,b_M5_tslot_nut1_001_013,b_FST_0017_M3_cap_nut1_001_,b_M5_tslot_nut1_001_015,Screw061,b_belt_tension_arm_001_001,b_front_right_leg_001_]
FEATURE [Part::FeaturePython] b_y_gantry_001_001  label="y-gantry_002"  # a2plus imported part (geometry in sourceFile) (typed FeaturePython)
  Placement = pos=(-11.975,209.125,134.768) rot=(0.57735,0.57735,0.57735;2.0944rad)
  a2p_Version = V0.1
  fixedPosition = false
  objectType = a2pPart
  sourceFile = ./FDM/y-gantry.FCStd
  subassemblyImport = false
  timeLastImport = 1.66338e+09
  updateColors = true
FEATURE [Part::FeaturePython] Screw253  label="M5x16-Screw180"  # Fasteners workbench fastener (typed FeaturePython)
  Placement = pos=(-35.8306,235.625,156.923) rot=(0,0.707107,0.707107;3.14159rad)
  Visibility1 = true
  diameter = 6
  invert = false
  leftHanded = false
  length = 4
  lengthCustom = 16
  matchOuter = false
  offset = 0
  thread = false
  type = 33
FEATURE [Part::FeaturePython] Screw254  label="M5x16-Screw181"  # Fasteners workbench fastener (typed FeaturePython)
  Placement = pos=(-50.8306,235.625,156.923) rot=(0,0.707107,0.707107;3.14159rad)
  Visibility1 = true
  diameter = 6
  invert = false
  leftHanded = false
  length = 4
  lengthCustom = 16
  matchOuter = false
  offset = 0
  thread = false
  type = 33
FEATURE [Part::FeaturePython] Nut124  label="M5-Nut"  # Fasteners workbench fastener (typed FeaturePython)
  Placement = pos=(-35.8306,223.125,156.923) rot=(0.186157,0.694747,0.694747;3.50969rad)
  Visibility1 = true
  diameter = 7
  invert = false
  leftHanded = false
  matchOuter = false
  offset = 0
  thread = false
  type = 7
FEATURE [Part::FeaturePython] Nut125  label="M5-Nut925"  # Fasteners workbench fastener (typed FeaturePython)
  Placement = pos=(-50.8306,223.125,156.923) rot=(0.186157,0.694747,0.694747;3.50969rad)
  Visibility1 = true
  diameter = 7
  invert = false
  leftHanded = false
  matchOuter = false
  offset = 0
  thread = false
  type = 7
FEATURE [App::DocumentObjectGroup] Drag_Chain_Mount_to_Front_Leg_Attachment_Hardware
  Group = -> [Screw251,Screw250]
FEATURE [App::DocumentObjectGroup] Drag_Chain  label="Drag-Chain-Assembly"
  Group = -> [Drag_Chain_Bolts,b_front_drag_chain_mount_v3_001_,Drag_Chain_Mount_to_Front_Leg_Attachment_Hardware]
FEATURE [Part::FeaturePython] b_aux_staging_plate_foot_001_  label="aux-staging-plate-foot_001"  # a2plus imported part (geometry in sourceFile) (typed FeaturePython)
  Placement = pos=(300.43,224,39.97) rot=(0.707107,0.707107,0;3.14159rad)
  a2p_Version = V0.1
  fixedPosition = false
  objectType = a2pPart
  sourceFile = ./FDM/aux-staging-plate-foot.FCStd
  subassemblyImport = false
  timeLastImport = 1.66336e+09
  updateColors = true
FEATURE [Part::FeaturePython] Nut126  label="M3-Nut535"  # Fasteners workbench fastener (typed FeaturePython)
  Placement = pos=(300.387,224.051,34.97) rot=(0.707107,-0.707107,0;3.14159rad)
  Visibility1 = true
  diameter = 4
  invert = false
  leftHanded = false
  matchOuter = false
  offset = 0
  thread = false
  type = 7
FEATURE [Part::FeaturePython] Screw257  label="M3x14-Screw184"  # Fasteners workbench fastener (typed FeaturePython)
  Placement = pos=(300.41,224.05,42.9) rot=(0,0,-1;1.5708rad)
  Visibility1 = true
  diameter = 1
  invert = false
  leftHanded = false
  length = 9
  lengthCustom = 14
  matchOuter = false
  offset = 0
  thread = false
  type = 39
FEATURE [App::DocumentObjectGroup] Support_Foot  label="Support-Foot"
  Group = -> [Screw257,b_aux_staging_plate_foot_001_,Nut126]
FEATURE [App::DocumentObjectGroup] Build_Plate  label="Auxiliary-Staging-Plate"
  Group = -> [b_staging_plate1_001_,Screw235,Screw236,Screw237,Screw238,b_M5_tslot_nut1_001_036,b_M5_tslot_nut1_001_037,b_M5_tslot_nut1_001_038,b_M5_tslot_nut1_001_039,Support_Foot]
FEATURE [Part::FeaturePython] b_mobo_cover_plate_001_  label="mobo-top-cover001"  # a2plus imported part (geometry in sourceFile) (typed FeaturePython)
  a2p_Version = V0.1
  fixedPosition = false
  objectType = a2pPart
  sourceFile = ./FDM/mobo-top-cover.FCStd
  subassemblyImport = false
  timeLastImport = 1.66336e+09
  updateColors = true
FEATURE [Part::FeaturePython] b_z_gantry_shorter_001_  label="z-gantry-right"  # a2plus imported part (geometry in sourceFile) (typed FeaturePython)
  Placement = pos=(453.15,174.98,125.54) rot=(1,0,0;1.5708rad)
  a2p_Version = V0.1
  fixedPosition = false
  objectType = a2pPart
  sourceFile = ./FDM/z-gantry.FCStd
  subassemblyImport = false
  timeLastImport = 1.66336e+09
  updateColors = true
FEATURE [App::DocumentObjectGroup] Group010  label="Right-Z-Gantry"
  Group = -> [Screw148,Screw149,b_FDM_0041_z_gantry_backplate_right_001_,Screw199,Screw200,b_NEMA11_hollow_shaft_stepper1_001_001,b_OTS_0001_00_CP40_nozzle_holder_001_001,b_MS4M_M51_001_001,Screw248,Screw246,Screw249,Screw247,b_z_gantry_shorter_001_]
FEATURE [Part::FeaturePython] b_z_gantry_shorter_001_001  label="z-gantry-left"  # a2plus imported part (geometry in sourceFile) (typed FeaturePython)
  Placement = pos=(405.49,174.9,125.57) rot=(1,0,0;1.5708rad)
  a2p_Version = V0.1
  fixedPosition = false
  objectType = a2pPart
  sourceFile = ./FDM/z-gantry.FCStd
  subassemblyImport = false
  timeLastImport = 1.66336e+09
  updateColors = true
FEATURE [App::DocumentObjectGroup] Group009  label="Left-Z-Gantry"
  Group = -> [b_FDM_0040_z_gantry_backplate_left_001_,Screw144,Screw146,b_OTS_0001_00_CP40_nozzle_holder_001_,b_MS4M_M51_001_,Screw201,Screw202,Screw216,Screw217,Screw218,Screw219,b_NEMA11_hollow_shaft_stepper1_001_,b_z_gantry_shorter_001_001]
FEATURE [Part::FeaturePython] b_y_coupler_bracket_001_  label="y-coupler-bracket_001"  # a2plus imported part (geometry in sourceFile) (typed FeaturePython)
  Placement = pos=(186.447,88.892,40.0011) rot=(0.57735,0.57735,-0.57735;4.18879rad)
  a2p_Version = V0.1
  fixedPosition = false
  objectType = a2pPart
  sourceFile = ./FDM/y-coupler-bracket.FCStd
  subassemblyImport = false
  timeLastImport = 1.66336e+09
  updateColors = true
FEATURE [Part::FeaturePython] Screw258  label="M3x10-Screw113"  # Fasteners workbench fastener (typed FeaturePython)
  Placement = pos=(180.31,104.04,43.1) rot=(0,0,-1;1.5708rad)
  Visibility1 = true
  diameter = 1
  invert = false
  leftHanded = false
  length = 2
  lengthCustom = 10
  matchOuter = false
  offset = 0
  thread = false
  type = 39
FEATURE [Part::FeaturePython] b_OTS_0009_pneumatic_splitter_URY6M_4M1_001_002  label="pneumatic-y-adapter002"  # a2plus imported part (geometry in sourceFile) (typed FeaturePython)
  Placement = pos=(202.73,81.5937,24.3499) rot=(0.57735,-0.57735,0.57735;2.0944rad)
  a2p_Version = V0.1
  fixedPosition = false
  objectType = a2pPart
  sourceFile = ./MISC/pneumatic-y-adapter.STEP
  subassemblyImport = false
  timeLastImport = 1.65531e+09
  updateColors = true
FEATURE [Part::FeaturePython] Nut127  label="M3-Nut538"  # Fasteners workbench fastener (typed FeaturePython)
  Placement = pos=(180.56,72.64,24.35) rot=(0.57735,0.57735,0.57735;4.18879rad)
  Visibility1 = true
  diameter = 4
  invert = false
  leftHanded = false
  matchOuter = false
  offset = 0
  thread = false
  type = 7
FEATURE [App::DocumentObjectGroup] Staging_Plate  label="Primary-Staging-Plate"
  Group = -> [Screw174,Screw175,Screw176,Screw177,Nut052,Nut053,Nut054,Nut055,Screw139,Screw142,Nut057,Nut058,Screw178,Screw179,Screw180,Screw134,Screw152,Screw153,Screw154,Screw155,b_FDM_0024_nozzle_holder_001_,Nut064,Nut066,Screw156,Screw158,Screw159,Screw160,Screw161,Screw162,b_CSM_0001_staging_plate_001_,b_M5_tslot_nut1_001_030,b_M5_tslot_nut1_001_031,b_M5_tslot_nut1_001_032,b_M5_tslot_nut1_001_033,+55 more]
FEATURE [App::DocumentObjectGroup] Group003  label="Staging-Plates"
  Group = -> [Staging_Plate,Build_Plate]
FEATURE [App::DocumentObjectGroup] Measurements
FEATURE [Part::Feature] Part__Feature  label="PRODUCT_NAME_1"
  shape: bbox 32.4 x 27 x 10 mm, 90 faces (baked)
FEATURE [Part::Feature] Part__Feature001  label="PRODUCT_NAME_2"
  shape: bbox 5 x 26.4 x 9.6 mm, 46 faces (baked)
FEATURE [Part::Feature] Part__Feature002  label="PRODUCT_NAME_3"
  shape: bbox 5 x 26.4 x 9.6 mm, 46 faces (baked)
FEATURE [Part::Feature] Part__Feature003  label="PRODUCT_NAME_4"
  shape: bbox 1.5 x 26.4 x 9.6 mm, 44 faces (baked)
FEATURE [Part::Feature] Part__Feature004  label="PRODUCT_NAME_5"
  shape: bbox 1.5 x 26.4 x 9.6 mm, 44 faces (baked)
FEATURE [Part::Feature] Part__Feature005  label="PRODUCT_NAME_6"
  shape: bbox 1.6 x 4 x 4 mm, 18 faces (baked)
FEATURE [Part::Feature] Part__Feature006  label="PRODUCT_NAME_7"
  shape: bbox 1.6 x 4 x 4 mm, 18 faces (baked)
FEATURE [Part::Feature] Part__Feature007  label="PRODUCT_NAME_8"
  shape: bbox 1.6 x 4 x 4 mm, 18 faces (baked)
FEATURE [Part::Feature] Part__Feature008  label="PRODUCT_NAME_9"
  shape: bbox 1.6 x 4 x 4 mm, 18 faces (baked)
FEATURE [Part::Feature] Part__Feature009  label="PRODUCT_NAME_10"
  shape: bbox 46 x 12 x 8 mm, 46 faces (baked)
FEATURE [Part::Compound] Compound  label="MGN12H"
  Links = -> [Part__Feature009,Part__Feature,Part__Feature001,Part__Feature002,Part__Feature003,Part__Feature004,Part__Feature005,Part__Feature006,Part__Feature007,Part__Feature008]
  Placement = pos=(9.9,196.125,110.018) rot=(0,0,1;1.5708rad)
FEATURE [Part::FeaturePython] Screw259  label="M3x8-Screw"  # Fasteners workbench fastener (typed FeaturePython)
  Placement = pos=(-0.065,219.13,128.69) rot=(0,0,1;0rad)
  baseObject = -> b_y_gantry_001_001 [Edge386]
  diameter = 4
  invert = false
  leftHanded = false
  length = 2
  lengthCustom = 8
  matchOuter = false
  offset = 0
  thread = false
  type = 36
FEATURE [App::FeaturePython] pointIdentity_001_mirror  label="pointIdentity_001__M5-Nut689"  # a2plus constraint (typed FeaturePython)
  Object1 = Nut037
  Object2 = b_y_gantry_001_001
  ParentTreeObject = -> b_y_gantry_001_001
  SubElement1 = Edge4
  SubElement2 = Edge288
  Suppressed = false
  Type = pointIdentity
FEATURE [App::FeaturePython] circularEdge_004_mirror  label="circularEdge_004__M5-Nut"  # a2plus constraint (typed FeaturePython)
  Object1 = Nut110
  Object2 = b_y_gantry_001_001
  ParentTreeObject = -> b_y_gantry_001_001
  SubElement1 = Edge13
  SubElement2 = Edge34
  Suppressed = false
  Type = circularEdge
  directionConstraint = 0
  lockRotation = false
  offset = 0
FEATURE [App::FeaturePython] circularEdge_007_mirror  label="circularEdge_007__M5-Nut688"  # a2plus constraint (typed FeaturePython)
  Object1 = Nut036
  Object2 = b_y_gantry_001_001
  ParentTreeObject = -> b_y_gantry_001_001
  SubElement1 = Edge13
  SubElement2 = Edge290
  Suppressed = false
  Type = circularEdge
  directionConstraint = 1
  lockRotation = false
  offset = 0
FEATURE [Part::Compound] Compound001  label="MGN12H001"
  Links = -> [Part__Feature009,Part__Feature,Part__Feature001,Part__Feature002,Part__Feature003,Part__Feature004,Part__Feature005,Part__Feature006,Part__Feature007,Part__Feature008]
FEATURE [Part::FeaturePython] b_x_gantry_block_mount_001_  label="x-gantry-block-mount_001"  # a2plus imported part (geometry in sourceFile) (typed FeaturePython)
  Placement = pos=(443.775,209.2,166.9) rot=(0,0.707107,0.707107;3.14159rad)
  a2p_Version = V0.1
  fixedPosition = false
  objectType = a2pPart
  sourceFile = ./x-gantry-block-mount.FCStd
  subassemblyImport = false
  timeLastImport = 1.66362e+09
  updateColors = true
FEATURE [Part::FeaturePython] MGN12H001_001  # a2plus imported part (geometry in sourceFile) (typed FeaturePython)
  Placement = pos=(430.775,209.2,154.9) rot=(0,0,1;0rad)
  a2p_Version = V0.1
  fixedPosition = true
  localSourceObject = Compound001
  objectType = a2pPart
  sourceFile = converted
  subassemblyImport = false
  timeLastImport = 1.66343e+09
  updateColors = true
FEATURE [Part::FeaturePython] b_x_gantry_back_001_001  label="x-gantry-back"  # a2plus imported part (geometry in sourceFile) (typed FeaturePython)
  Placement = pos=(443.775,234.2,123.4) rot=(1,0,0;1.5708rad)
  a2p_Version = V0.1
  fixedPosition = false
  objectType = a2pPart
  sourceFile = ./FDM/x-gantry-back.FCStd
  subassemblyImport = false
  timeLastImport = 1.66344e+09
  updateColors = true
FEATURE [App::FeaturePython] circularEdge_008  label="circularEdge_008__x-gantry-back_001"  # a2plus constraint (typed FeaturePython)
  Object1 = b_FDM_0014_down_camera_mount_001_
  Object2 = b_x_gantry_back_001_001
  ParentTreeObject = -> b_FDM_0014_down_camera_mount_001_
  SubElement1 = Edge246
  SubElement2 = Edge157
  Suppressed = false
  Type = circularEdge
  directionConstraint = 1
  lockRotation = false
  offset = 0
FEATURE [App::FeaturePython] circularEdge_008_mirror  label="circularEdge_008__top-camera-mount"  # a2plus constraint (typed FeaturePython)
  Object1 = b_FDM_0014_down_camera_mount_001_
  Object2 = b_x_gantry_back_001_001
  ParentTreeObject = -> b_x_gantry_back_001_001
  SubElement1 = Edge246
  SubElement2 = Edge157
  Suppressed = false
  Type = circularEdge
  directionConstraint = 1
  lockRotation = false
  offset = 0
FEATURE [App::FeaturePython] circularEdge_009  label="circularEdge_009__top-camera-mount"  # a2plus constraint (typed FeaturePython)
  Object1 = b_FDM_0015_down_light_mount_001_
  Object2 = b_FDM_0014_down_camera_mount_001_
  ParentTreeObject = -> b_FDM_0015_down_light_mount_001_
  SubElement1 = Edge43
  SubElement2 = Edge146
  Suppressed = false
  Type = circularEdge
  directionConstraint = 0
  lockRotation = false
  offset = 0
FEATURE [App::FeaturePython] circularEdge_009_mirror  label="circularEdge_009__top-light-mount"  # a2plus constraint (typed FeaturePython)
  Object1 = b_FDM_0015_down_light_mount_001_
  Object2 = b_FDM_0014_down_camera_mount_001_
  ParentTreeObject = -> b_FDM_0014_down_camera_mount_001_
  SubElement1 = Edge43
  SubElement2 = Edge146
  Suppressed = false
  Type = circularEdge
  directionConstraint = 0
  lockRotation = false
  offset = 0
FEATURE [Part::FeaturePython] b_Nema_17_42A02C_v21_001_003  label="NEMA17-stepper004"  # a2plus imported part (geometry in sourceFile) (typed FeaturePython)
  Placement = pos=(590.08,546.54,90.25) rot=(0,0,1;0rad)
  Visibility1 = true
  a2p_Version = V0.1
  fixedPosition = false
  objectType = a2pPart
  sourceFile = ./MISC/NEMA17-stepper.step 
  sourcePart = NEMA17-stepper
  subassemblyImport = false
  timeLastImport = 1.64563e+09
  updateColors = true
FEATURE [Part::FeaturePython] b_back_leg_cleaned_001_  label="back-leg"  # a2plus imported part (geometry in sourceFile) (typed FeaturePython)
  Placement = pos=(590,500.06,-49.9) rot=(0.57735,-0.57735,-0.57735;2.0944rad)
  a2p_Version = V0.1
  fixedPosition = false
  objectType = a2pPart
  sourceFile = ./FDM/back-leg.FCStd
  subassemblyImport = false
  timeLastImport = 1.66336e+09
  updateColors = true
FEATURE [App::DocumentObjectGroup] Group007  label="Back-Right-Leg"
  Group = -> [b_Gates_2GT_20T_Toothed_Pulley1_001_003,Screw096,Screw093,Screw094,Screw095,b_Nema_17_42A02C_v21_001_003,Screw032,Screw033,Screw034,b_M5_tslot_nut1_001_007,b_M5_tslot_nut1_001_006,b_M5_tslot_nut1_001_005,b_back_leg_cleaned_001_]
FEATURE [App::DocumentObjectGroup] Y_Gantry_Right  label="Y-Gantry-Right"
  Group = -> [Extrusion001,Group007,Group005,Y_Gantry_Slider_Right]
FEATURE [App::FeaturePython] planeCoincident_001  label="planeCoincident_001__MGN12H"  # a2plus constraint (typed FeaturePython)
  Object1 = b_OTS_0009_20x20_v_slot_600mm1_001_002
  Object2 = Compound
  ParentTreeObject = -> b_OTS_0009_20x20_v_slot_600mm1_001_002
  SubElement1 = Face28
  SubElement2 = Face32
  Suppressed = false
  Type = plane
  directionConstraint = 1
  offset = 0
FEATURE [App::FeaturePython] planeCoincident_001_mirror  label="planeCoincident_001__vslot-extrusion-20mmx20mmx600mm"  # a2plus constraint (typed FeaturePython)
  Object1 = b_OTS_0009_20x20_v_slot_600mm1_001_002
  Object2 = Compound
  ParentTreeObject = -> Compound
  SubElement1 = Face28
  SubElement2 = Face32
  Suppressed = false
  Type = plane
  directionConstraint = 1
  offset = 0
FEATURE [App::FeaturePython] circularEdge_003  label="circularEdge_003__y-gantry_002"  # a2plus constraint (typed FeaturePython)
  Object1 = Compound
  Object2 = b_y_gantry_001_001
  ParentTreeObject = -> Compound
  SubElement1 = Edge336
  SubElement2 = Edge89
  Suppressed = false
  Type = circularEdge
  directionConstraint = 1
  lockRotation = false
  offset = 0
FEATURE [App::FeaturePython] circularEdge_003_mirror  label="circularEdge_003__MGN12H"  # a2plus constraint (typed FeaturePython)
  Object1 = Compound
  Object2 = b_y_gantry_001_001
  ParentTreeObject = -> b_y_gantry_001_001
  SubElement1 = Edge336
  SubElement2 = Edge89
  Suppressed = false
  Type = circularEdge
  directionConstraint = 1
  lockRotation = false
  offset = 0
FEATURE [App::FeaturePython] circularEdge_004  label="circularEdge_004__y-gantry_002"  # a2plus constraint (typed FeaturePython)
  Object1 = b_x_motor_mount_001_
  Object2 = b_y_gantry_001_001
  ParentTreeObject = -> b_x_motor_mount_001_
  SubElement1 = Edge86
  SubElement2 = Edge246
  Suppressed = false
  Type = circularEdge
  directionConstraint = 0
  lockRotation = false
  offset = 0
FEATURE [App::FeaturePython] circularEdge_004_mirror001  label="circularEdge_004__x-motor-mount"  # a2plus constraint (typed FeaturePython)
  Object1 = b_x_motor_mount_001_
  Object2 = b_y_gantry_001_001
  ParentTreeObject = -> b_y_gantry_001_001
  SubElement1 = Edge86
  SubElement2 = Edge246
  Suppressed = false
  Type = circularEdge
  directionConstraint = 0
  lockRotation = false
  offset = 0
FEATURE [App::FeaturePython] circularEdge_005  label="circularEdge_005__y-gantry_002"  # a2plus constraint (typed FeaturePython)
  Object1 = b_FDM_0027_belt_clamp_001_
  Object2 = b_y_gantry_001_001
  ParentTreeObject = -> b_FDM_0027_belt_clamp_001_
  SubElement1 = Edge18
  SubElement2 = Edge242
  Suppressed = false
  Type = circularEdge
  directionConstraint = 1
  lockRotation = false
  offset = 0
FEATURE [App::FeaturePython] circularEdge_005_mirror  label="circularEdge_005__belt-clamp001"  # a2plus constraint (typed FeaturePython)
  Object1 = b_FDM_0027_belt_clamp_001_
  Object2 = b_y_gantry_001_001
  ParentTreeObject = -> b_y_gantry_001_001
  SubElement1 = Edge18
  SubElement2 = Edge242
  Suppressed = false
  Type = circularEdge
  directionConstraint = 1
  lockRotation = false
  offset = 0
FEATURE [App::FeaturePython] circularEdge_006  label="circularEdge_006__y-gantry_002"  # a2plus constraint (typed FeaturePython)
  Object1 = b_FDM_0027_belt_clamp_001_001
  Object2 = b_y_gantry_001_001
  ParentTreeObject = -> b_FDM_0027_belt_clamp_001_001
  SubElement1 = Edge18
  SubElement2 = Edge244
  Suppressed = false
  Type = circularEdge
  directionConstraint = 1
  lockRotation = false
  offset = 0
FEATURE [App::FeaturePython] circularEdge_006_mirror  label="circularEdge_006__belt-clamp002"  # a2plus constraint (typed FeaturePython)
  Object1 = b_FDM_0027_belt_clamp_001_001
  Object2 = b_y_gantry_001_001
  ParentTreeObject = -> b_y_gantry_001_001
  SubElement1 = Edge18
  SubElement2 = Edge244
  Suppressed = false
  Type = circularEdge
  directionConstraint = 1
  lockRotation = false
  offset = 0
FEATURE [App::FeaturePython] circularEdge_007  label="circularEdge_007__x-motor-mount"  # a2plus constraint (typed FeaturePython)
  Object1 = Nut124
  Object2 = b_x_motor_mount_001_
  ParentTreeObject = -> Nut124
  SubElement1 = Edge2
  SubElement2 = Edge183
  Suppressed = false
  Type = circularEdge
  directionConstraint = 0
  lockRotation = false
  offset = 0
FEATURE [App::FeaturePython] circularEdge_007_mirror001  label="circularEdge_007__M5-Nut"  # a2plus constraint (typed FeaturePython)
  Object1 = Nut124
  Object2 = b_x_motor_mount_001_
  ParentTreeObject = -> b_x_motor_mount_001_
  SubElement1 = Edge2
  SubElement2 = Edge183
  Suppressed = false
  Type = circularEdge
  directionConstraint = 0
  lockRotation = false
  offset = 0
FEATURE [App::FeaturePython] circularEdge_012  label="circularEdge_012__x-motor-mount"  # a2plus constraint (typed FeaturePython)
  Object1 = Nut125
  Object2 = b_x_motor_mount_001_
  ParentTreeObject = -> Nut125
  SubElement1 = Edge2
  SubElement2 = Edge185
  Suppressed = false
  Type = circularEdge
  directionConstraint = 0
  lockRotation = false
  offset = 0
FEATURE [App::FeaturePython] circularEdge_012_mirror  label="circularEdge_012__M5-Nut768"  # a2plus constraint (typed FeaturePython)
  Object1 = Nut125
  Object2 = b_x_motor_mount_001_
  ParentTreeObject = -> b_x_motor_mount_001_
  SubElement1 = Edge2
  SubElement2 = Edge185
  Suppressed = false
  Type = circularEdge
  directionConstraint = 0
  lockRotation = false
  offset = 0
FEATURE [App::FeaturePython] circularEdge_013  label="circularEdge_013__x-motor-mount"  # a2plus constraint (typed FeaturePython)
  Object1 = b_x_motor_cable_guide_001_
  Object2 = b_x_motor_mount_001_
  ParentTreeObject = -> b_x_motor_cable_guide_001_
  SubElement1 = Edge40
  SubElement2 = Edge100
  Suppressed = false
  Type = circularEdge
  directionConstraint = 0
  lockRotation = false
  offset = 0
FEATURE [App::FeaturePython] circularEdge_013_mirror  label="circularEdge_013__x-motor-cable-guide"  # a2plus constraint (typed FeaturePython)
  Object1 = b_x_motor_cable_guide_001_
  Object2 = b_x_motor_mount_001_
  ParentTreeObject = -> b_x_motor_mount_001_
  SubElement1 = Edge40
  SubElement2 = Edge100
  Suppressed = false
  Type = circularEdge
  directionConstraint = 0
  lockRotation = false
  offset = 0
FEATURE [App::FeaturePython] circularEdge_014  label="circularEdge_014__x-motor-cable-guide"  # a2plus constraint (typed FeaturePython)
  Object1 = Screw254
  Object2 = b_x_motor_cable_guide_001_
  ParentTreeObject = -> Screw254
  SubElement1 = Edge7
  SubElement2 = Edge79
  Suppressed = false
  Type = circularEdge
  directionConstraint = 0
  lockRotation = false
  offset = 0
FEATURE [App::FeaturePython] circularEdge_014_mirror  label="circularEdge_014__M5x16-Screw008"  # a2plus constraint (typed FeaturePython)
  Object1 = Screw254
  Object2 = b_x_motor_cable_guide_001_
  ParentTreeObject = -> b_x_motor_cable_guide_001_
  SubElement1 = Edge7
  SubElement2 = Edge79
  Suppressed = false
  Type = circularEdge
  directionConstraint = 0
  lockRotation = false
  offset = 0
FEATURE [App::FeaturePython] circularEdge_015  label="circularEdge_015__x-motor-cable-guide"  # a2plus constraint (typed FeaturePython)
  Object1 = Screw253
  Object2 = b_x_motor_cable_guide_001_
  ParentTreeObject = -> Screw253
  SubElement1 = Edge7
  SubElement2 = Edge80
  Suppressed = false
  Type = circularEdge
  directionConstraint = 0
  lockRotation = false
  offset = 0
FEATURE [App::FeaturePython] circularEdge_015_mirror  label="circularEdge_015__M5x16-Screw007"  # a2plus constraint (typed FeaturePython)
  Object1 = Screw253
  Object2 = b_x_motor_cable_guide_001_
  ParentTreeObject = -> b_x_motor_cable_guide_001_
  SubElement1 = Edge7
  SubElement2 = Edge80
  Suppressed = false
  Type = circularEdge
  directionConstraint = 0
  lockRotation = false
  offset = 0
FEATURE [App::FeaturePython] circularEdge_016  label="circularEdge_016__x-motor-mount"  # a2plus constraint (typed FeaturePython)
  Object1 = b_Nema_17_42A02C_v21_001_001
  Object2 = b_x_motor_mount_001_
  ParentTreeObject = -> b_Nema_17_42A02C_v21_001_001
  SubElement1 = Edge95
  SubElement2 = Edge181
  Suppressed = false
  Type = circularEdge
  directionConstraint = 1
  lockRotation = false
  offset = 0
FEATURE [App::FeaturePython] circularEdge_016_mirror  label="circularEdge_016__NEMA17-stepper"  # a2plus constraint (typed FeaturePython)
  Object1 = b_Nema_17_42A02C_v21_001_001
  Object2 = b_x_motor_mount_001_
  ParentTreeObject = -> b_x_motor_mount_001_
  SubElement1 = Edge95
  SubElement2 = Edge181
  Suppressed = false
  Type = circularEdge
  directionConstraint = 1
  lockRotation = false
  offset = 0
FEATURE [App::FeaturePython] circularEdge_017  label="circularEdge_017__NEMA17-stepper"  # a2plus constraint (typed FeaturePython)
  Object1 = b_Gates_2GT_20T_Toothed_Pulley1_001_001
  Object2 = b_Nema_17_42A02C_v21_001_001
  ParentTreeObject = -> b_Gates_2GT_20T_Toothed_Pulley1_001_001
  SubElement1 = Edge465
  SubElement2 = Edge36
  Suppressed = false
  Type = circularEdge
  directionConstraint = 0
  lockRotation = false
  offset = -15
FEATURE [App::FeaturePython] circularEdge_017_mirror  label="circularEdge_017__GT2-pulley"  # a2plus constraint (typed FeaturePython)
  Object1 = b_Gates_2GT_20T_Toothed_Pulley1_001_001
  Object2 = b_Nema_17_42A02C_v21_001_001
  ParentTreeObject = -> b_Nema_17_42A02C_v21_001_001
  SubElement1 = Edge465
  SubElement2 = Edge36
  Suppressed = false
  Type = circularEdge
  directionConstraint = 0
  lockRotation = false
  offset = -15
FEATURE [App::FeaturePython] circularEdge_018  label="circularEdge_018__x-motor-mount"  # a2plus constraint (typed FeaturePython)
  Object1 = Screw099
  Object2 = b_x_motor_mount_001_
  ParentTreeObject = -> Screw099
  SubElement1 = Edge2
  SubElement2 = Edge234
  Suppressed = false
  Type = circularEdge
  directionConstraint = 1
  lockRotation = false
  offset = 0
FEATURE [App::FeaturePython] circularEdge_018_mirror  label="circularEdge_018__M3x8-Screw540"  # a2plus constraint (typed FeaturePython)
  Object1 = Screw099
  Object2 = b_x_motor_mount_001_
  ParentTreeObject = -> b_x_motor_mount_001_
  SubElement1 = Edge2
  SubElement2 = Edge234
  Suppressed = false
  Type = circularEdge
  directionConstraint = 1
  lockRotation = false
  offset = 0
FEATURE [App::FeaturePython] circularEdge_019  label="circularEdge_019__M3x8-Screw539"  # a2plus constraint (typed FeaturePython)
  Object1 = b_x_motor_mount_001_
  Object2 = Screw100
  ParentTreeObject = -> b_x_motor_mount_001_
  SubElement1 = Edge198
  SubElement2 = Edge2
  Suppressed = false
  Type = circularEdge
  directionConstraint = 1
  lockRotation = false
  offset = 0
FEATURE [App::FeaturePython] circularEdge_019_mirror  label="circularEdge_019__x-motor-mount"  # a2plus constraint (typed FeaturePython)
  Object1 = b_x_motor_mount_001_
  Object2 = Screw100
  ParentTreeObject = -> Screw100
  SubElement1 = Edge198
  SubElement2 = Edge2
  Suppressed = false
  Type = circularEdge
  directionConstraint = 1
  lockRotation = false
  offset = 0
FEATURE [App::FeaturePython] circularEdge_020  label="circularEdge_020__x-motor-mount"  # a2plus constraint (typed FeaturePython)
  Object1 = Screw098
  Object2 = b_x_motor_mount_001_
  ParentTreeObject = -> Screw098
  SubElement1 = Edge2
  SubElement2 = Edge197
  Suppressed = false
  Type = circularEdge
  directionConstraint = 1
  lockRotation = false
  offset = 0
FEATURE [App::FeaturePython] circularEdge_020_mirror  label="circularEdge_020__M3x8-Screw542"  # a2plus constraint (typed FeaturePython)
  Object1 = Screw098
  Object2 = b_x_motor_mount_001_
  ParentTreeObject = -> b_x_motor_mount_001_
  SubElement1 = Edge2
  SubElement2 = Edge197
  Suppressed = false
  Type = circularEdge
  directionConstraint = 1
  lockRotation = false
  offset = 0
FEATURE [App::FeaturePython] circularEdge_021  label="circularEdge_021__M3x8-Screw541"  # a2plus constraint (typed FeaturePython)
  Object1 = b_x_motor_mount_001_
  Object2 = Screw097
  ParentTreeObject = -> b_x_motor_mount_001_
  SubElement1 = Edge233
  SubElement2 = Edge2
  Suppressed = false
  Type = circularEdge
  directionConstraint = 1
  lockRotation = false
  offset = 0
FEATURE [App::FeaturePython] circularEdge_021_mirror  label="circularEdge_021__x-motor-mount"  # a2plus constraint (typed FeaturePython)
  Object1 = b_x_motor_mount_001_
  Object2 = Screw097
  ParentTreeObject = -> Screw097
  SubElement1 = Edge233
  SubElement2 = Edge2
  Suppressed = false
  Type = circularEdge
  directionConstraint = 1
  lockRotation = false
  offset = 0
FEATURE [App::FeaturePython] circularEdge_022  label="circularEdge_022__x-motor-mount"  # a2plus constraint (typed FeaturePython)
  Object1 = Screw221
  Object2 = b_x_motor_mount_001_
  ParentTreeObject = -> Screw221
  SubElement1 = Edge7
  SubElement2 = Edge293
  Suppressed = false
  Type = circularEdge
  directionConstraint = 0
  lockRotation = false
  offset = 0
FEATURE [App::FeaturePython] circularEdge_022_mirror  label="circularEdge_022__M5x10-Screw367"  # a2plus constraint (typed FeaturePython)
  Object1 = Screw221
  Object2 = b_x_motor_mount_001_
  ParentTreeObject = -> b_x_motor_mount_001_
  SubElement1 = Edge7
  SubElement2 = Edge293
  Suppressed = false
  Type = circularEdge
  directionConstraint = 0
  lockRotation = false
  offset = 0
FEATURE [App::FeaturePython] circularEdge_023  label="circularEdge_023__M5x10-Screw"  # a2plus constraint (typed FeaturePython)
  Object1 = b_x_motor_mount_001_
  Object2 = Screw022
  ParentTreeObject = -> b_x_motor_mount_001_
  SubElement1 = Edge291
  SubElement2 = Edge7
  Suppressed = false
  Type = circularEdge
  directionConstraint = 0
  lockRotation = false
  offset = 0
FEATURE [App::FeaturePython] circularEdge_023_mirror  label="circularEdge_023__x-motor-mount"  # a2plus constraint (typed FeaturePython)
  Object1 = b_x_motor_mount_001_
  Object2 = Screw022
  ParentTreeObject = -> Screw022
  SubElement1 = Edge291
  SubElement2 = Edge7
  Suppressed = false
  Type = circularEdge
  directionConstraint = 0
  lockRotation = false
  offset = 0
FEATURE [Part::FeaturePython] Screw260  label="M5x12-Screw"  # Fasteners workbench fastener (typed FeaturePython)
  Placement = pos=(-14.975,236.125,107.268) rot=(0,-1,0;1.5708rad)
  baseObject = -> b_FDM_0027_belt_clamp_001_ [Edge63]
  diameter = 6
  invert = true
  leftHanded = false
  length = 2
  lengthCustom = 12
  matchOuter = false
  offset = 0
  thread = false
  type = 36
FEATURE [Part::FeaturePython] Screw261  label="M5x12-Screw001"  # Fasteners workbench fastener (typed FeaturePython)
  Placement = pos=(-14.975,236.125,92.2676) rot=(0,-1,0;1.5708rad)
  baseObject = -> b_FDM_0027_belt_clamp_001_ [Edge145]
  diameter = 6
  invert = true
  leftHanded = false
  length = 2
  lengthCustom = 12
  matchOuter = false
  offset = 0
  thread = false
  type = 36
FEATURE [Part::FeaturePython] Screw262  label="M5x10-Screw370"  # Fasteners workbench fastener (typed FeaturePython)
  Placement = pos=(-14.975,182.125,107.268) rot=(0,-1,0;1.5708rad)
  baseObject = -> b_FDM_0027_belt_clamp_001_001 [Edge63]
  diameter = 6
  invert = true
  leftHanded = false
  length = 1
  lengthCustom = 10
  matchOuter = false
  offset = 0
  thread = false
  type = 36
FEATURE [Part::FeaturePython] Screw263  label="M5x10-Screw371"  # Fasteners workbench fastener (typed FeaturePython)
  Placement = pos=(-14.975,182.125,92.2676) rot=(0,-1,0;1.5708rad)
  baseObject = -> b_FDM_0027_belt_clamp_001_001 [Edge145]
  diameter = 6
  invert = true
  leftHanded = false
  length = 1
  lengthCustom = 10
  matchOuter = false
  offset = 0
  thread = false
  type = 36
FEATURE [Part::FeaturePython] Nut128  label="M5-Nut769"  # Fasteners workbench fastener (typed FeaturePython)
  Placement = pos=(-4.26575,182.125,107.268) rot=(0,-1,0;1.5708rad)
  diameter = 7
  invert = false
  leftHanded = false
  matchOuter = true
  offset = 0
  thread = false
  type = 9
FEATURE [Part::FeaturePython] Nut130  label="M5-Nut770"  # Fasteners workbench fastener (typed FeaturePython)
  Placement = pos=(-5.46575,182.125,92.2676) rot=(0,-1,0;1.5708rad)
  baseObject = -> Screw263 [Edge12]
  diameter = 7
  invert = false
  leftHanded = false
  matchOuter = true
  offset = 0
  thread = false
  type = 9
FEATURE [Part::FeaturePython] Nut131  label="M5-Nut771"  # Fasteners workbench fastener (typed FeaturePython)
  Placement = pos=(-3.46575,236.125,107.268) rot=(0,-1,0;1.5708rad)
  baseObject = -> Screw260 [Edge12]
  diameter = 7
  invert = false
  leftHanded = false
  matchOuter = true
  offset = 0
  thread = false
  type = 9
FEATURE [Part::FeaturePython] Nut132  label="M5-Nut772"  # Fasteners workbench fastener (typed FeaturePython)
  Placement = pos=(-3.46575,236.125,92.2676) rot=(0,-1,0;1.5708rad)
  baseObject = -> Screw261 [Edge12]
  diameter = 7
  invert = false
  leftHanded = false
  matchOuter = true
  offset = 0
  thread = false
  type = 9
FEATURE [App::DocumentObjectGroup] Y_Gantry_Slider_Left  label="Y-Gantry-Slider-Left"
  Group = -> [b_FDM_0027_belt_clamp_001_001,Screw260,Screw261,b_y_gantry_001_001,Screw262,Screw263,Nut128,Nut130,Nut131,Nut132]
FEATURE [App::DocumentObjectGroup] Y_Gantry_Left  label="Y-Gantry-Left"
  Group = -> [Extrusion,Group006,Group004,Y_Gantry_Slider_Left]
FEATURE [Part::FeaturePython] Screw264  label="M5x20-Screw001"  # Fasteners workbench fastener (typed FeaturePython)
  Placement = pos=(-24.975,209.125,122.768) rot=(0,-1,0;1.5708rad)
  baseObject = -> b_x_motor_mount_001_ [Edge245]
  diameter = 6
  invert = false
  leftHanded = false
  length = 5
  lengthCustom = 20
  matchOuter = true
  offset = 0
  thread = false
  type = 36
FEATURE [Part::FeaturePython] Screw265  label="M5x20-Screw"  # Fasteners workbench fastener (typed FeaturePython)
  Placement = pos=(-24.975,209.125,98.7676) rot=(0,-1,0;1.5708rad)
  baseObject = -> b_x_motor_mount_001_ [Edge237]
  diameter = 6
  invert = false
  leftHanded = false
  length = 5
  lengthCustom = 20
  matchOuter = true
  offset = 0
  thread = false
  type = 36
FEATURE [Part::FeaturePython] Nut133  label="M5-Nut775"  # Fasteners workbench fastener (typed FeaturePython)
  Placement = pos=(-5.46575,209.125,122.768) rot=(0,-1,0;1.5708rad)
  baseObject = -> Screw264 [Edge12]
  diameter = 7
  invert = false
  leftHanded = false
  matchOuter = true
  offset = 0
  thread = false
  type = 9
FEATURE [Part::FeaturePython] Nut134  label="M5-Nut774"  # Fasteners workbench fastener (typed FeaturePython)
  Placement = pos=(-5.46575,209.125,98.7676) rot=(0,-1,0;1.5708rad)
  baseObject = -> Screw265 [Edge12]
  diameter = 7
  invert = false
  leftHanded = false
  matchOuter = true
  offset = 0
  thread = false
  type = 9
FEATURE [App::DocumentObjectGroup] X_Gantry_Removable_Subassembly  label="X-Gantry001"
  Group = -> [Screw013,Screw221,Screw220,b_x_motor_mount_001_,b_x_idler_mount_001_,b_M5_tslot_nut1_001_034,Screw012,b_M5_tslot_nut1_001_035,X_Motor,Screw059,Screw060,b_M5_tslot_nut1_001_001,Screw022,b_Gates_2GT_20T_Toothed_Idler1_001_002,Screw021,Nut042,Nut044,Nut043,b_OTS_0009_20x20_v_slot_600mm1_001_003,b_M5_tslot_nut1_001_,Screw023,b_FST_0017_M3_cap_nut1_001_001,b_belt_tension_arm_001_,+10 more]
FEATURE [Part::FeaturePython] Screw  label="M5x12-Screw005"  # Fasteners workbench fastener (typed FeaturePython)
  Placement = pos=(474.775,189.2,164.9) rot=(1,0,0;1.5708rad)
  baseObject = -> b_FDM_0011_x_gantry_front_001_ [Edge609]
  diameter = 6
  invert = true
  leftHanded = false
  length = 2
  lengthCustom = 12
  matchOuter = true
  offset = 0
  thread = false
  type = 36
FEATURE [Part::FeaturePython] Screw266  label="M5x12-Screw006"  # Fasteners workbench fastener (typed FeaturePython)
  Placement = pos=(412.775,189.2,164.9) rot=(1,0,0;1.5708rad)
  baseObject = -> b_FDM_0011_x_gantry_front_001_ [Edge584]
  diameter = 6
  invert = true
  leftHanded = false
  length = 2
  lengthCustom = 12
  matchOuter = true
  offset = 0
  thread = false
  type = 36
FEATURE [Part::FeaturePython] Screw267  label="M5x12-Screw003"  # Fasteners workbench fastener (typed FeaturePython)
  Placement = pos=(412.775,229.4,164.9) rot=(-1,0,0;1.5708rad)
  baseObject = -> b_x_gantry_back_001_001 [Edge340]
  diameter = 6
  invert = false
  leftHanded = false
  length = 2
  lengthCustom = 12
  matchOuter = true
  offset = 0
  thread = false
  type = 36
FEATURE [Part::FeaturePython] Screw268  label="M5x12-Screw004"  # Fasteners workbench fastener (typed FeaturePython)
  Placement = pos=(474.775,229.4,164.9) rot=(-1,0,0;1.5708rad)
  baseObject = -> b_x_gantry_back_001_001 [Edge293]
  diameter = 6
  invert = false
  leftHanded = false
  length = 2
  lengthCustom = 12
  matchOuter = true
  offset = 0
  thread = false
  type = 36
FEATURE [Part::FeaturePython] Screw269  label="M5x12-Screw007"  # Fasteners workbench fastener (typed FeaturePython)
  Placement = pos=(474.775,229.4,123.4) rot=(-1,0,0;1.5708rad)
  baseObject = -> b_x_gantry_back_001_001 [Edge208]
  diameter = 6
  invert = false
  leftHanded = false
  length = 2
  lengthCustom = 12
  matchOuter = true
  offset = 0
  thread = false
  type = 36
FEATURE [Part::FeaturePython] Screw270  label="M5x12-Screw008"  # Fasteners workbench fastener (typed FeaturePython)
  Placement = pos=(412.775,229.4,123.4) rot=(-1,0,0;1.5708rad)
  baseObject = -> b_x_gantry_back_001_001 [Edge238]
  diameter = 6
  invert = false
  leftHanded = false
  length = 2
  lengthCustom = 12
  matchOuter = true
  offset = 0
  thread = false
  type = 36
FEATURE [App::FeaturePython] circularEdge_024  label="circularEdge_024__x-gantry-back"  # a2plus constraint (typed FeaturePython)
  Object1 = Nut024
  Object2 = b_x_gantry_back_001_001
  ParentTreeObject = -> Nut024
  SubElement1 = Edge2
  SubElement2 = Edge398
  Suppressed = false
  Type = circularEdge
  directionConstraint = 0
  lockRotation = false
  offset = 0
FEATURE [App::FeaturePython] circularEdge_024_mirror  label="circularEdge_024__M5-Nut649"  # a2plus constraint (typed FeaturePython)
  Object1 = Nut024
  Object2 = b_x_gantry_back_001_001
  ParentTreeObject = -> b_x_gantry_back_001_001
  SubElement1 = Edge2
  SubElement2 = Edge398
  Suppressed = false
  Type = circularEdge
  directionConstraint = 0
  lockRotation = false
  offset = 0
FEATURE [App::FeaturePython] circularEdge_025  label="circularEdge_025__M5-Nut646"  # a2plus constraint (typed FeaturePython)
  Object1 = b_x_gantry_back_001_001
  Object2 = Nut021
  ParentTreeObject = -> b_x_gantry_back_001_001
  SubElement1 = Edge392
  SubElement2 = Edge2
  Suppressed = false
  Type = circularEdge
  directionConstraint = 0
  lockRotation = false
  offset = 0
FEATURE [App::FeaturePython] circularEdge_025_mirror  label="circularEdge_025__x-gantry-back"  # a2plus constraint (typed FeaturePython)
  Object1 = b_x_gantry_back_001_001
  Object2 = Nut021
  ParentTreeObject = -> Nut021
  SubElement1 = Edge392
  SubElement2 = Edge2
  Suppressed = false
  Type = circularEdge
  directionConstraint = 0
  lockRotation = false
  offset = 0
FEATURE [App::FeaturePython] circularEdge_026  label="circularEdge_026__x-gantry-back"  # a2plus constraint (typed FeaturePython)
  Object1 = Nut023
  Object2 = b_x_gantry_back_001_001
  ParentTreeObject = -> Nut023
  SubElement1 = Edge1
  SubElement2 = Edge390
  Suppressed = false
  Type = circularEdge
  directionConstraint = 0
  lockRotation = false
  offset = 0
FEATURE [App::FeaturePython] circularEdge_026_mirror  label="circularEdge_026__M5-Nut648"  # a2plus constraint (typed FeaturePython)
  Object1 = Nut023
  Object2 = b_x_gantry_back_001_001
  ParentTreeObject = -> b_x_gantry_back_001_001
  SubElement1 = Edge1
  SubElement2 = Edge390
  Suppressed = false
  Type = circularEdge
  directionConstraint = 0
  lockRotation = false
  offset = 0
FEATURE [App::FeaturePython] circularEdge_027  label="circularEdge_027__x-gantry-back"  # a2plus constraint (typed FeaturePython)
  Object1 = Nut022
  Object2 = b_x_gantry_back_001_001
  ParentTreeObject = -> Nut022
  SubElement1 = Edge2
  SubElement2 = Edge386
  Suppressed = false
  Type = circularEdge
  directionConstraint = 0
  lockRotation = false
  offset = 0
FEATURE [App::FeaturePython] circularEdge_027_mirror  label="circularEdge_027__M5-Nut647"  # a2plus constraint (typed FeaturePython)
  Object1 = Nut022
  Object2 = b_x_gantry_back_001_001
  ParentTreeObject = -> b_x_gantry_back_001_001
  SubElement1 = Edge2
  SubElement2 = Edge386
  Suppressed = false
  Type = circularEdge
  directionConstraint = 0
  lockRotation = false
  offset = 0
FEATURE [App::FeaturePython] circularEdge_028  label="circularEdge_028__x-gantry-back"  # a2plus constraint (typed FeaturePython)
  Object1 = b_FDM_0027_belt_clamp_001_002
  Object2 = b_x_gantry_back_001_001
  ParentTreeObject = -> b_FDM_0027_belt_clamp_001_002
  SubElement1 = Edge83
  SubElement2 = Edge169
  Suppressed = false
  Type = circularEdge
  directionConstraint = 1
  lockRotation = false
  offset = 0
FEATURE [App::FeaturePython] circularEdge_028_mirror  label="circularEdge_028__belt-clamp005"  # a2plus constraint (typed FeaturePython)
  Object1 = b_FDM_0027_belt_clamp_001_002
  Object2 = b_x_gantry_back_001_001
  ParentTreeObject = -> b_x_gantry_back_001_001
  SubElement1 = Edge83
  SubElement2 = Edge169
  Suppressed = false
  Type = circularEdge
  directionConstraint = 1
  lockRotation = false
  offset = 0
FEATURE [App::FeaturePython] circularEdge_029  label="circularEdge_029__belt-clamp006"  # a2plus constraint (typed FeaturePython)
  Object1 = b_x_gantry_back_001_001
  Object2 = b_FDM_0027_belt_clamp_001_003
  ParentTreeObject = -> b_x_gantry_back_001_001
  SubElement1 = Edge159
  SubElement2 = Edge18
  Suppressed = false
  Type = circularEdge
  directionConstraint = 1
  lockRotation = false
  offset = 0
FEATURE [App::FeaturePython] circularEdge_029_mirror  label="circularEdge_029__x-gantry-back"  # a2plus constraint (typed FeaturePython)
  Object1 = b_x_gantry_back_001_001
  Object2 = b_FDM_0027_belt_clamp_001_003
  ParentTreeObject = -> b_FDM_0027_belt_clamp_001_003
  SubElement1 = Edge159
  SubElement2 = Edge18
  Suppressed = false
  Type = circularEdge
  directionConstraint = 1
  lockRotation = false
  offset = 0
FEATURE [App::FeaturePython] circularEdge_030  label="circularEdge_030__belt-clamp006"  # a2plus constraint (typed FeaturePython)
  Object1 = Screw039
  Object2 = b_FDM_0027_belt_clamp_001_003
  ParentTreeObject = -> Screw039
  SubElement1 = Edge7
  SubElement2 = Edge63
  Suppressed = false
  Type = circularEdge
  directionConstraint = 1
  lockRotation = false
  offset = 0
FEATURE [App::FeaturePython] circularEdge_030_mirror  label="circularEdge_030__M5x10-Screw357"  # a2plus constraint (typed FeaturePython)
  Object1 = Screw039
  Object2 = b_FDM_0027_belt_clamp_001_003
  ParentTreeObject = -> b_FDM_0027_belt_clamp_001_003
  SubElement1 = Edge7
  SubElement2 = Edge63
  Suppressed = false
  Type = circularEdge
  directionConstraint = 1
  lockRotation = false
  offset = 0
FEATURE [App::FeaturePython] circularEdge_031  label="circularEdge_031__M5x10-Screw356"  # a2plus constraint (typed FeaturePython)
  Object1 = b_FDM_0027_belt_clamp_001_003
  Object2 = Screw038
  ParentTreeObject = -> b_FDM_0027_belt_clamp_001_003
  SubElement1 = Edge145
  SubElement2 = Edge7
  Suppressed = false
  Type = circularEdge
  directionConstraint = 1
  lockRotation = false
  offset = 0
FEATURE [App::FeaturePython] circularEdge_031_mirror  label="circularEdge_031__belt-clamp006"  # a2plus constraint (typed FeaturePython)
  Object1 = b_FDM_0027_belt_clamp_001_003
  Object2 = Screw038
  ParentTreeObject = -> Screw038
  SubElement1 = Edge145
  SubElement2 = Edge7
  Suppressed = false
  Type = circularEdge
  directionConstraint = 1
  lockRotation = false
  offset = 0
FEATURE [App::FeaturePython] circularEdge_032  label="circularEdge_032__M5x10-Screw358"  # a2plus constraint (typed FeaturePython)
  Object1 = b_FDM_0027_belt_clamp_001_002
  Object2 = Screw040
  ParentTreeObject = -> b_FDM_0027_belt_clamp_001_002
  SubElement1 = Edge145
  SubElement2 = Edge7
  Suppressed = false
  Type = circularEdge
  directionConstraint = 1
  lockRotation = false
  offset = 0
FEATURE [App::FeaturePython] circularEdge_032_mirror  label="circularEdge_032__belt-clamp005"  # a2plus constraint (typed FeaturePython)
  Object1 = b_FDM_0027_belt_clamp_001_002
  Object2 = Screw040
  ParentTreeObject = -> Screw040
  SubElement1 = Edge145
  SubElement2 = Edge7
  Suppressed = false
  Type = circularEdge
  directionConstraint = 1
  lockRotation = false
  offset = 0
FEATURE [App::FeaturePython] circularEdge_033  label="circularEdge_033__belt-clamp005"  # a2plus constraint (typed FeaturePython)
  Object1 = Screw041
  Object2 = b_FDM_0027_belt_clamp_001_002
  ParentTreeObject = -> Screw041
  SubElement1 = Edge7
  SubElement2 = Edge63
  Suppressed = false
  Type = circularEdge
  directionConstraint = 1
  lockRotation = false
  offset = 0
FEATURE [App::FeaturePython] circularEdge_033_mirror  label="circularEdge_033__M5x10-Screw359"  # a2plus constraint (typed FeaturePython)
  Object1 = Screw041
  Object2 = b_FDM_0027_belt_clamp_001_002
  ParentTreeObject = -> b_FDM_0027_belt_clamp_001_002
  SubElement1 = Edge7
  SubElement2 = Edge63
  Suppressed = false
  Type = circularEdge
  directionConstraint = 1
  lockRotation = false
  offset = 0
FEATURE [App::FeaturePython] circularEdge_034  label="circularEdge_034__x-gantry-back"  # a2plus constraint (typed FeaturePython)
  Object1 = Nut077
  Object2 = b_x_gantry_back_001_001
  ParentTreeObject = -> Nut077
  SubElement1 = Edge2
  SubElement2 = Edge388
  Suppressed = false
  Type = circularEdge
  directionConstraint = 0
  lockRotation = false
  offset = 0
FEATURE [App::FeaturePython] circularEdge_034_mirror  label="circularEdge_034__M3-Nut530"  # a2plus constraint (typed FeaturePython)
  Object1 = Nut077
  Object2 = b_x_gantry_back_001_001
  ParentTreeObject = -> b_x_gantry_back_001_001
  SubElement1 = Edge2
  SubElement2 = Edge388
  Suppressed = false
  Type = circularEdge
  directionConstraint = 0
  lockRotation = false
  offset = 0
FEATURE [App::FeaturePython] circularEdge_035  label="circularEdge_035__x-gantry-back"  # a2plus constraint (typed FeaturePython)
  Object1 = Nut079
  Object2 = b_x_gantry_back_001_001
  ParentTreeObject = -> Nut079
  SubElement1 = Edge2
  SubElement2 = Edge384
  Suppressed = false
  Type = circularEdge
  directionConstraint = 0
  lockRotation = false
  offset = 0
FEATURE [App::FeaturePython] circularEdge_035_mirror  label="circularEdge_035__M3-Nut531"  # a2plus constraint (typed FeaturePython)
  Object1 = Nut079
  Object2 = b_x_gantry_back_001_001
  ParentTreeObject = -> b_x_gantry_back_001_001
  SubElement1 = Edge2
  SubElement2 = Edge384
  Suppressed = false
  Type = circularEdge
  directionConstraint = 0
  lockRotation = false
  offset = 0
FEATURE [App::FeaturePython] circularEdge_038  label="circularEdge_038__x-gantry-back"  # a2plus constraint (typed FeaturePython)
  Object1 = Screw222
  Object2 = b_x_gantry_back_001_001
  ParentTreeObject = -> Screw222
  SubElement1 = Edge7
  SubElement2 = Edge17
  Suppressed = false
  Type = circularEdge
  directionConstraint = 0
  lockRotation = false
  offset = 0
FEATURE [App::FeaturePython] circularEdge_038_mirror  label="circularEdge_038__M5x16-Screw006"  # a2plus constraint (typed FeaturePython)
  Object1 = Screw222
  Object2 = b_x_gantry_back_001_001
  ParentTreeObject = -> b_x_gantry_back_001_001
  SubElement1 = Edge7
  SubElement2 = Edge17
  Suppressed = false
  Type = circularEdge
  directionConstraint = 0
  lockRotation = false
  offset = 0
FEATURE [App::FeaturePython] circularEdge_039  label="circularEdge_039__M5x16-Screw005"  # a2plus constraint (typed FeaturePython)
  Object1 = b_x_gantry_back_001_001
  Object2 = Screw223
  ParentTreeObject = -> b_x_gantry_back_001_001
  SubElement1 = Edge16
  SubElement2 = Edge7
  Suppressed = false
  Type = circularEdge
  directionConstraint = 0
  lockRotation = false
  offset = 0
FEATURE [App::FeaturePython] circularEdge_039_mirror  label="circularEdge_039__x-gantry-back"  # a2plus constraint (typed FeaturePython)
  Object1 = b_x_gantry_back_001_001
  Object2 = Screw223
  ParentTreeObject = -> Screw223
  SubElement1 = Edge16
  SubElement2 = Edge7
  Suppressed = false
  Type = circularEdge
  directionConstraint = 0
  lockRotation = false
  offset = 0
FEATURE [App::FeaturePython] circularEdge_040  label="circularEdge_040__M5x16-Screw006"  # a2plus constraint (typed FeaturePython)
  Object1 = Nut108
  Object2 = Screw222
  ParentTreeObject = -> Nut108
  SubElement1 = Edge4
  SubElement2 = Edge12
  Suppressed = false
  Type = circularEdge
  directionConstraint = 0
  lockRotation = false
  offset = 0
FEATURE [App::FeaturePython] circularEdge_040_mirror  label="circularEdge_040__M5-Nut655"  # a2plus constraint (typed FeaturePython)
  Object1 = Nut108
  Object2 = Screw222
  ParentTreeObject = -> Screw222
  SubElement1 = Edge4
  SubElement2 = Edge12
  Suppressed = false
  Type = circularEdge
  directionConstraint = 0
  lockRotation = false
  offset = 0
FEATURE [App::FeaturePython] circularEdge_041  label="circularEdge_041__M5-Nut656"  # a2plus constraint (typed FeaturePython)
  Object1 = Screw223
  Object2 = Nut107
  ParentTreeObject = -> Screw223
  SubElement1 = Edge12
  SubElement2 = Edge4
  Suppressed = false
  Type = circularEdge
  directionConstraint = 0
  lockRotation = false
  offset = 0
FEATURE [App::FeaturePython] circularEdge_041_mirror  label="circularEdge_041__M5x16-Screw005"  # a2plus constraint (typed FeaturePython)
  Object1 = Screw223
  Object2 = Nut107
  ParentTreeObject = -> Nut107
  SubElement1 = Edge12
  SubElement2 = Edge4
  Suppressed = false
  Type = circularEdge
  directionConstraint = 0
  lockRotation = false
  offset = 0
FEATURE [Part::FeaturePython] Screw273  label="M3x8-Screw654"  # Fasteners workbench fastener (typed FeaturePython)
  Placement = pos=(433.775,199.2,173.9) rot=(0,0,1;0rad)
  baseObject = -> b_x_gantry_block_mount_001_ [Edge6]
  diameter = 4
  invert = true
  leftHanded = false
  length = 2
  lengthCustom = 8
  matchOuter = true
  offset = 0
  thread = false
  type = 36
FEATURE [Part::FeaturePython] Screw274  label="M3x8-Screw655"  # Fasteners workbench fastener (typed FeaturePython)
  Placement = pos=(453.775,199.2,173.9) rot=(0,0,1;0rad)
  baseObject = -> b_x_gantry_block_mount_001_ [Edge5]
  diameter = 4
  invert = true
  leftHanded = false
  length = 2
  lengthCustom = 8
  matchOuter = true
  offset = 0
  thread = false
  type = 36
FEATURE [Part::FeaturePython] Screw275  label="M3x8-Screw656"  # Fasteners workbench fastener (typed FeaturePython)
  Placement = pos=(453.775,219.2,173.9) rot=(0,0,1;0rad)
  baseObject = -> b_x_gantry_block_mount_001_ [Edge7]
  diameter = 4
  invert = true
  leftHanded = false
  length = 2
  lengthCustom = 8
  matchOuter = true
  offset = 0
  thread = false
  type = 36
FEATURE [Part::FeaturePython] Screw276  label="M3x8-Screw657"  # Fasteners workbench fastener (typed FeaturePython)
  Placement = pos=(433.775,219.2,173.9) rot=(0,0,1;0rad)
  baseObject = -> b_x_gantry_block_mount_001_ [Edge8]
  diameter = 4
  invert = true
  leftHanded = false
  length = 2
  lengthCustom = 8
  matchOuter = true
  offset = 0
  thread = false
  type = 36
FEATURE [Part::FeaturePython] Screw277  label="M3x8-Screw599"  # Fasteners workbench fastener (typed FeaturePython)
  Placement = pos=(19.9,219.125,128.518) rot=(0,0,1;0rad)
  baseObject = -> b_y_gantry_001_001 [Edge223]
  diameter = 4
  invert = false
  leftHanded = false
  length = 2
  lengthCustom = 8
  matchOuter = true
  offset = 0
  thread = false
  type = 36
FEATURE [Part::FeaturePython] Screw278  label="M3x8-Screw600"  # Fasteners workbench fastener (typed FeaturePython)
  Placement = pos=(19.9,199.125,128.518) rot=(0,0,1;0rad)
  baseObject = -> b_y_gantry_001_001 [Edge219]
  diameter = 4
  invert = false
  leftHanded = false
  length = 2
  lengthCustom = 8
  matchOuter = true
  offset = 0
  thread = false
  type = 36
FEATURE [Part::FeaturePython] Screw279  label="M3x8-Screw601"  # Fasteners workbench fastener (typed FeaturePython)
  Placement = pos=(-0.1,199.125,128.518) rot=(0,0,1;0rad)
  baseObject = -> b_y_gantry_001_001 [Edge217]
  diameter = 4
  invert = false
  leftHanded = false
  length = 2
  lengthCustom = 8
  matchOuter = true
  offset = 0
  thread = false
  type = 36
FEATURE [App::DocumentObjectGroup] Y_Gantry_Legs  label="Y-Gantry"
  Group = -> [Y_Gantry_Right,Y_Gantry_Left,b_FDM_0027_belt_clamp_001_,Screw277,Screw278,Screw279,Compound]
FEATURE [Part::FeaturePython] b_x_gantry_block_mount_001_001  label="x-gantry-block-mount_002"  # a2plus imported part (geometry in sourceFile) (typed FeaturePython)
  Placement = pos=(443.775,209.2,125.4) rot=(0,0.707107,0.707107;3.14159rad)
  a2p_Version = V0.1
  fixedPosition = false
  objectType = a2pPart
  sourceFile = ./x-gantry-block-mount.FCStd
  subassemblyImport = false
  timeLastImport = 1.66362e+09
  updateColors = true
FEATURE [App::DocumentObjectGroup] Group015  label="Toolhead-Base"
  Group = -> [Nut,b_FDM_0011_x_gantry_front_001_,b_Gates_2GT_20T_Toothed_Idler1_001_,b_x_gantry_back_001_001,Nut027,Nut029,Nut030,Nut031,Nut079,Nut077,Nut032,Nut028,Screw223,Screw222,Nut108,Nut107,b_x_gantry_block_mount_001_,Screw273,Screw274,Screw275,Screw276,b_x_gantry_block_mount_001_001,Screw044,Screw,Screw266,Screw267,Screw268,Screw270,Screw269,MGN12H001_001]
FEATURE [App::DocumentObjectGroup] Group002  label="Toolhead"
  Group = -> [Group015,Group009,Group010,Group012,Group014,Group013]
FEATURE [App::DocumentObjectGroup] SDfsdf  label="X-Gantry"
  Group = -> [Group002,X_Gantry_Removable_Subassembly]
FEATURE [App::FeaturePython] circularEdge_001  label="circularEdge_001__x-gantry-block-mount_001"  # a2plus constraint (typed FeaturePython)
  Object1 = MGN12H001_001
  Object2 = b_x_gantry_block_mount_001_
  ParentTreeObject = -> MGN12H001_001
  SubElement1 = Edge157
  SubElement2 = Edge108
  Suppressed = false
  Type = circularEdge
  directionConstraint = 0
  lockRotation = false
  offset = 0
FEATURE [App::FeaturePython] circularEdge_001_mirror  label="circularEdge_001__MGN12H001_001"  # a2plus constraint (typed FeaturePython)
  Object1 = MGN12H001_001
  Object2 = b_x_gantry_block_mount_001_
  ParentTreeObject = -> b_x_gantry_block_mount_001_
  SubElement1 = Edge157
  SubElement2 = Edge108
  Suppressed = false
  Type = circularEdge
  directionConstraint = 0
  lockRotation = false
  offset = 0
FEATURE [App::FeaturePython] circularEdge_002  label="circularEdge_002__x-gantry-back"  # a2plus constraint (typed FeaturePython)
  Object1 = b_x_gantry_block_mount_001_001
  Object2 = b_x_gantry_back_001_001
  ParentTreeObject = -> b_x_gantry_block_mount_001_001
  SubElement1 = Edge55
  SubElement2 = Edge69
  Suppressed = false
  Type = circularEdge
  directionConstraint = 1
  lockRotation = false
  offset = 0
FEATURE [App::FeaturePython] circularEdge_002_mirror  label="circularEdge_002__x-gantry-block-mount_002"  # a2plus constraint (typed FeaturePython)
  Object1 = b_x_gantry_block_mount_001_001
  Object2 = b_x_gantry_back_001_001
  ParentTreeObject = -> b_x_gantry_back_001_001
  SubElement1 = Edge55
  SubElement2 = Edge69
  Suppressed = false
  Type = circularEdge
  directionConstraint = 1
  lockRotation = false
  offset = 0
FEATURE [App::FeaturePython] circularEdge_010  label="circularEdge_010__x-gantry-back"  # a2plus constraint (typed FeaturePython)
  Object1 = b_x_gantry_block_mount_001_
  Object2 = b_x_gantry_back_001_001
  ParentTreeObject = -> b_x_gantry_block_mount_001_
  SubElement1 = Edge55
  SubElement2 = Edge109
  Suppressed = false
  Type = circularEdge
  directionConstraint = 1
  lockRotation = false
  offset = 0
FEATURE [App::FeaturePython] circularEdge_010_mirror  label="circularEdge_010__x-gantry-block-mount_001"  # a2plus constraint (typed FeaturePython)
  Object1 = b_x_gantry_block_mount_001_
  Object2 = b_x_gantry_back_001_001
  ParentTreeObject = -> b_x_gantry_back_001_001
  SubElement1 = Edge55
  SubElement2 = Edge109
  Suppressed = false
  Type = circularEdge
  directionConstraint = 1
  lockRotation = false
  offset = 0
FEATURE [Part::FeaturePython] Nut135  label="M4-Nut"  # Fasteners workbench fastener (typed FeaturePython)
  Placement = pos=(474.775,220.3,164.9) rot=(1,0,0;1.5708rad)
  baseObject = -> b_x_gantry_block_mount_001_ [Edge60]
  diameter = 6
  invert = false
  leftHanded = false
  matchOuter = true
  offset = 0
  thread = false
  type = 9
FEATURE [Part::FeaturePython] Nut136  label="M4-Nut001"  # Fasteners workbench fastener (typed FeaturePython)
  Placement = pos=(474.775,198.1,164.9) rot=(-1,0,0;1.5708rad)
  baseObject = -> b_x_gantry_block_mount_001_ [Edge105]
  diameter = 6
  invert = true
  leftHanded = false
  matchOuter = true
  offset = 0
  thread = false
  type = 9
FEATURE [Part::FeaturePython] Nut137  label="M4-Nut002"  # Fasteners workbench fastener (typed FeaturePython)
  Placement = pos=(412.775,198.1,164.9) rot=(-1,0,0;1.5708rad)
  baseObject = -> b_x_gantry_block_mount_001_ [Edge113]
  diameter = 6
  invert = true
  leftHanded = false
  matchOuter = true
  offset = 0
  thread = false
  type = 9
FEATURE [Part::FeaturePython] Nut138  label="M4-Nut003"  # Fasteners workbench fastener (typed FeaturePython)
  Placement = pos=(412.775,220.3,164.9) rot=(1,0,0;1.5708rad)
  baseObject = -> b_x_gantry_block_mount_001_ [Edge87]
  diameter = 6
  invert = false
  leftHanded = false
  matchOuter = true
  offset = 0
  thread = false
  type = 9
